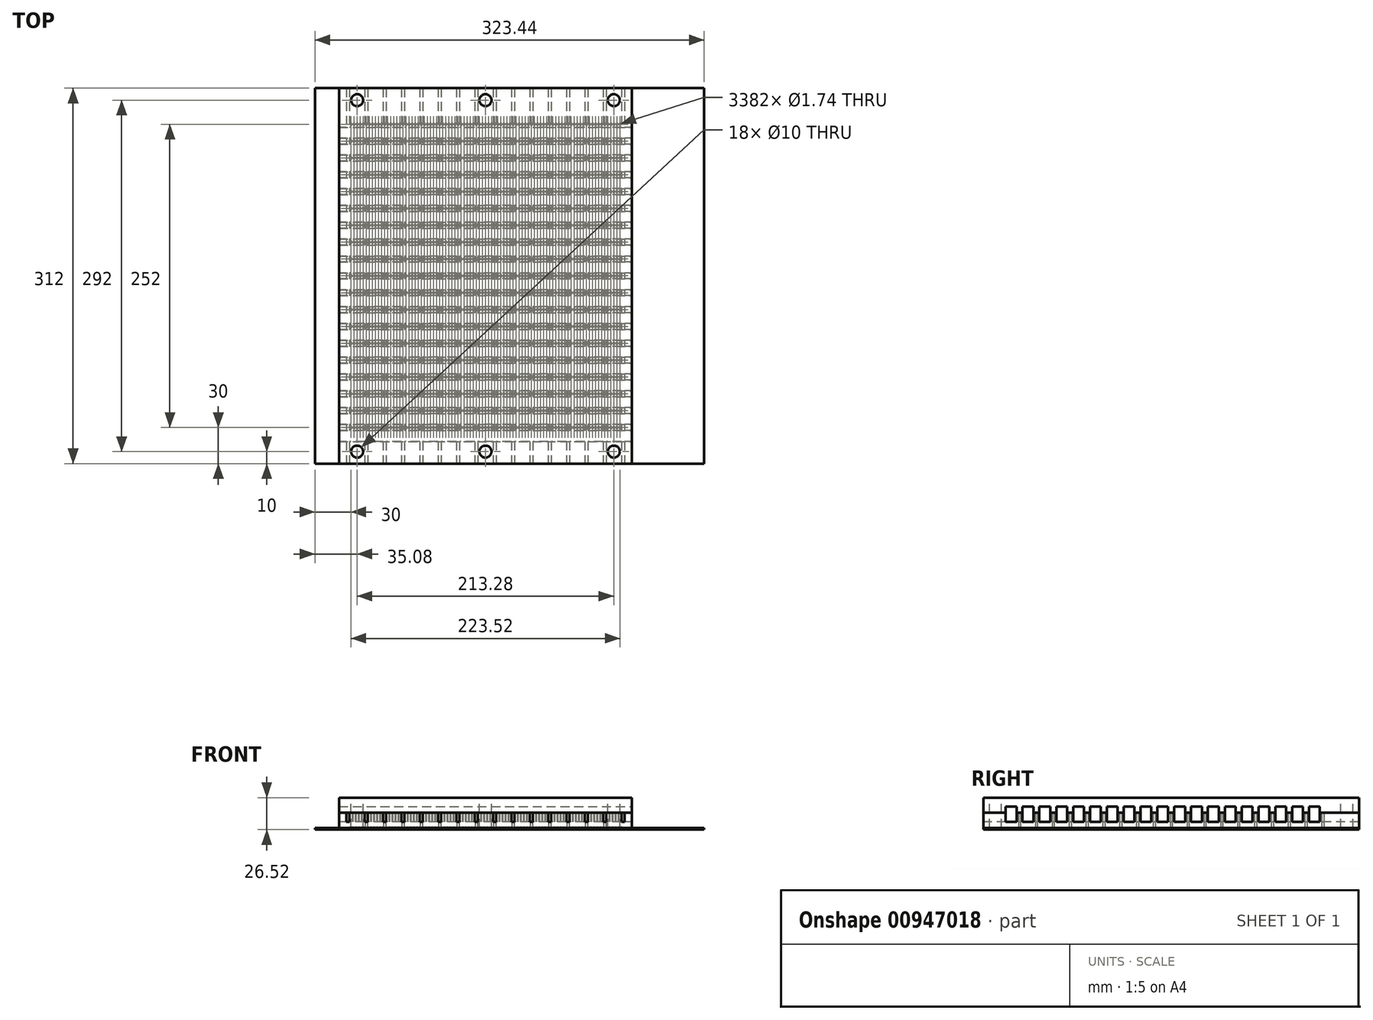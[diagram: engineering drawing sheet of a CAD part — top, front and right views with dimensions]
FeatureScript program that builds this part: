
annotation { "Feature Type Name" : "Feature", "Feature Type Description" : "" }
export const myFeature = defineFeature(function(context is Context, id is Id, definition is map)
    precondition{}
    {
        {
            var Q0;
            Q0=qCreatedBy(makeId("Top.planeOp"),FACE);
            var sketch = newSketch(context, id + "F0", { "sketchPlane" : qUnion([Q0])});
            skCircle(sketch, "E0", {"center": v(0, 0) * mm, "radius": 0.87 * mm});
            skCircle(sketch, "E1.0.1.0", {"center": v(0, -14) * mm, "radius": 0.87 * mm});
            skCircle(sketch, "E1.0.2.0", {"center": v(0, -28) * mm, "radius": 0.87 * mm});
            skCircle(sketch, "E1.0.3.0", {"center": v(0, -42) * mm, "radius": 0.87 * mm});
            skCircle(sketch, "E1.0.4.0", {"center": v(0, -56) * mm, "radius": 0.87 * mm});
            skCircle(sketch, "E1.0.5.0", {"center": v(0, -70) * mm, "radius": 0.87 * mm});
            skCircle(sketch, "E1.0.6.0", {"center": v(0, -84) * mm, "radius": 0.87 * mm});
            skCircle(sketch, "E1.0.7.0", {"center": v(0, -98) * mm, "radius": 0.87 * mm});
            skCircle(sketch, "E1.0.8.0", {"center": v(0, -112) * mm, "radius": 0.87 * mm});
            skCircle(sketch, "E1.0.9.0", {"center": v(0, -126) * mm, "radius": 0.87 * mm});
            skCircle(sketch, "E1.0.10.0", {"center": v(0, -140) * mm, "radius": 0.87 * mm});
            skCircle(sketch, "E1.0.11.0", {"center": v(0, -154) * mm, "radius": 0.87 * mm});
            skCircle(sketch, "E1.0.12.0", {"center": v(0, -168) * mm, "radius": 0.87 * mm});
            skCircle(sketch, "E1.0.13.0", {"center": v(0, -182) * mm, "radius": 0.87 * mm});
            skCircle(sketch, "E1.0.14.0", {"center": v(0, -196) * mm, "radius": 0.87 * mm});
            skCircle(sketch, "E1.0.15.0", {"center": v(0, -210) * mm, "radius": 0.87 * mm});
            skCircle(sketch, "E1.0.16.0", {"center": v(0, -224) * mm, "radius": 0.87 * mm});
            skCircle(sketch, "E1.0.17.0", {"center": v(0, -238) * mm, "radius": 0.87 * mm});
            skCircle(sketch, "E1.0.18.0", {"center": v(0, -252) * mm, "radius": 0.87 * mm});
            skCircle(sketch, "E1.1.0.0", {"center": v(2.54, 0) * mm, "radius": 0.87 * mm});
            skCircle(sketch, "E1.1.1.0", {"center": v(2.54, -14) * mm, "radius": 0.87 * mm});
            skCircle(sketch, "E1.1.2.0", {"center": v(2.54, -28) * mm, "radius": 0.87 * mm});
            skCircle(sketch, "E1.1.3.0", {"center": v(2.54, -42) * mm, "radius": 0.87 * mm});
            skCircle(sketch, "E1.1.4.0", {"center": v(2.54, -56) * mm, "radius": 0.87 * mm});
            skCircle(sketch, "E1.1.5.0", {"center": v(2.54, -70) * mm, "radius": 0.87 * mm});
            skCircle(sketch, "E1.1.6.0", {"center": v(2.54, -84) * mm, "radius": 0.87 * mm});
            skCircle(sketch, "E1.1.7.0", {"center": v(2.54, -98) * mm, "radius": 0.87 * mm});
            skCircle(sketch, "E1.1.8.0", {"center": v(2.54, -112) * mm, "radius": 0.87 * mm});
            skCircle(sketch, "E1.1.9.0", {"center": v(2.54, -126) * mm, "radius": 0.87 * mm});
            skCircle(sketch, "E1.1.10.0", {"center": v(2.54, -140) * mm, "radius": 0.87 * mm});
            skCircle(sketch, "E1.1.11.0", {"center": v(2.54, -154) * mm, "radius": 0.87 * mm});
            skCircle(sketch, "E1.1.12.0", {"center": v(2.54, -168) * mm, "radius": 0.87 * mm});
            skCircle(sketch, "E1.1.13.0", {"center": v(2.54, -182) * mm, "radius": 0.87 * mm});
            skCircle(sketch, "E1.1.14.0", {"center": v(2.54, -196) * mm, "radius": 0.87 * mm});
            skCircle(sketch, "E1.1.15.0", {"center": v(2.54, -210) * mm, "radius": 0.87 * mm});
            skCircle(sketch, "E1.1.16.0", {"center": v(2.54, -224) * mm, "radius": 0.87 * mm});
            skCircle(sketch, "E1.1.17.0", {"center": v(2.54, -238) * mm, "radius": 0.87 * mm});
            skCircle(sketch, "E1.1.18.0", {"center": v(2.54, -252) * mm, "radius": 0.87 * mm});
            skCircle(sketch, "E1.2.0.0", {"center": v(5.08, 0) * mm, "radius": 0.87 * mm});
            skCircle(sketch, "E1.2.1.0", {"center": v(5.08, -14) * mm, "radius": 0.87 * mm});
            skCircle(sketch, "E1.2.2.0", {"center": v(5.08, -28) * mm, "radius": 0.87 * mm});
            skCircle(sketch, "E1.2.3.0", {"center": v(5.08, -42) * mm, "radius": 0.87 * mm});
            skCircle(sketch, "E1.2.4.0", {"center": v(5.08, -56) * mm, "radius": 0.87 * mm});
            skCircle(sketch, "E1.2.5.0", {"center": v(5.08, -70) * mm, "radius": 0.87 * mm});
            skCircle(sketch, "E1.2.6.0", {"center": v(5.08, -84) * mm, "radius": 0.87 * mm});
            skCircle(sketch, "E1.2.7.0", {"center": v(5.08, -98) * mm, "radius": 0.87 * mm});
            skCircle(sketch, "E1.2.8.0", {"center": v(5.08, -112) * mm, "radius": 0.87 * mm});
            skCircle(sketch, "E1.2.9.0", {"center": v(5.08, -126) * mm, "radius": 0.87 * mm});
            skCircle(sketch, "E1.2.10.0", {"center": v(5.08, -140) * mm, "radius": 0.87 * mm});
            skCircle(sketch, "E1.2.11.0", {"center": v(5.08, -154) * mm, "radius": 0.87 * mm});
            skCircle(sketch, "E1.2.12.0", {"center": v(5.08, -168) * mm, "radius": 0.87 * mm});
            skCircle(sketch, "E1.2.13.0", {"center": v(5.08, -182) * mm, "radius": 0.87 * mm});
            skCircle(sketch, "E1.2.14.0", {"center": v(5.08, -196) * mm, "radius": 0.87 * mm});
            skCircle(sketch, "E1.2.15.0", {"center": v(5.08, -210) * mm, "radius": 0.87 * mm});
            skCircle(sketch, "E1.2.16.0", {"center": v(5.08, -224) * mm, "radius": 0.87 * mm});
            skCircle(sketch, "E1.2.17.0", {"center": v(5.08, -238) * mm, "radius": 0.87 * mm});
            skCircle(sketch, "E1.2.18.0", {"center": v(5.08, -252) * mm, "radius": 0.87 * mm});
            skCircle(sketch, "E1.3.0.0", {"center": v(7.62, 0) * mm, "radius": 0.87 * mm});
            skCircle(sketch, "E1.3.1.0", {"center": v(7.62, -14) * mm, "radius": 0.87 * mm});
            skCircle(sketch, "E1.3.2.0", {"center": v(7.62, -28) * mm, "radius": 0.87 * mm});
            skCircle(sketch, "E1.3.3.0", {"center": v(7.62, -42) * mm, "radius": 0.87 * mm});
            skCircle(sketch, "E1.3.4.0", {"center": v(7.62, -56) * mm, "radius": 0.87 * mm});
            skCircle(sketch, "E1.3.5.0", {"center": v(7.62, -70) * mm, "radius": 0.87 * mm});
            skCircle(sketch, "E1.3.6.0", {"center": v(7.62, -84) * mm, "radius": 0.87 * mm});
            skCircle(sketch, "E1.3.7.0", {"center": v(7.62, -98) * mm, "radius": 0.87 * mm});
            skCircle(sketch, "E1.3.8.0", {"center": v(7.62, -112) * mm, "radius": 0.87 * mm});
            skCircle(sketch, "E1.3.9.0", {"center": v(7.62, -126) * mm, "radius": 0.87 * mm});
            skCircle(sketch, "E1.3.10.0", {"center": v(7.62, -140) * mm, "radius": 0.87 * mm});
            skCircle(sketch, "E1.3.11.0", {"center": v(7.62, -154) * mm, "radius": 0.87 * mm});
            skCircle(sketch, "E1.3.12.0", {"center": v(7.62, -168) * mm, "radius": 0.87 * mm});
            skCircle(sketch, "E1.3.13.0", {"center": v(7.62, -182) * mm, "radius": 0.87 * mm});
            skCircle(sketch, "E1.3.14.0", {"center": v(7.62, -196) * mm, "radius": 0.87 * mm});
            skCircle(sketch, "E1.3.15.0", {"center": v(7.62, -210) * mm, "radius": 0.87 * mm});
            skCircle(sketch, "E1.3.16.0", {"center": v(7.62, -224) * mm, "radius": 0.87 * mm});
            skCircle(sketch, "E1.3.17.0", {"center": v(7.62, -238) * mm, "radius": 0.87 * mm});
            skCircle(sketch, "E1.3.18.0", {"center": v(7.62, -252) * mm, "radius": 0.87 * mm});
            skCircle(sketch, "E1.4.0.0", {"center": v(10.16, 0) * mm, "radius": 0.87 * mm});
            skCircle(sketch, "E1.4.1.0", {"center": v(10.16, -14) * mm, "radius": 0.87 * mm});
            skCircle(sketch, "E1.4.2.0", {"center": v(10.16, -28) * mm, "radius": 0.87 * mm});
            skCircle(sketch, "E1.4.3.0", {"center": v(10.16, -42) * mm, "radius": 0.87 * mm});
            skCircle(sketch, "E1.4.4.0", {"center": v(10.16, -56) * mm, "radius": 0.87 * mm});
            skCircle(sketch, "E1.4.5.0", {"center": v(10.16, -70) * mm, "radius": 0.87 * mm});
            skCircle(sketch, "E1.4.6.0", {"center": v(10.16, -84) * mm, "radius": 0.87 * mm});
            skCircle(sketch, "E1.4.7.0", {"center": v(10.16, -98) * mm, "radius": 0.87 * mm});
            skCircle(sketch, "E1.4.8.0", {"center": v(10.16, -112) * mm, "radius": 0.87 * mm});
            skCircle(sketch, "E1.4.9.0", {"center": v(10.16, -126) * mm, "radius": 0.87 * mm});
            skCircle(sketch, "E1.4.10.0", {"center": v(10.16, -140) * mm, "radius": 0.87 * mm});
            skCircle(sketch, "E1.4.11.0", {"center": v(10.16, -154) * mm, "radius": 0.87 * mm});
            skCircle(sketch, "E1.4.12.0", {"center": v(10.16, -168) * mm, "radius": 0.87 * mm});
            skCircle(sketch, "E1.4.13.0", {"center": v(10.16, -182) * mm, "radius": 0.87 * mm});
            skCircle(sketch, "E1.4.14.0", {"center": v(10.16, -196) * mm, "radius": 0.87 * mm});
            skCircle(sketch, "E1.4.15.0", {"center": v(10.16, -210) * mm, "radius": 0.87 * mm});
            skCircle(sketch, "E1.4.16.0", {"center": v(10.16, -224) * mm, "radius": 0.87 * mm});
            skCircle(sketch, "E1.4.17.0", {"center": v(10.16, -238) * mm, "radius": 0.87 * mm});
            skCircle(sketch, "E1.4.18.0", {"center": v(10.16, -252) * mm, "radius": 0.87 * mm});
            skCircle(sketch, "E1.5.0.0", {"center": v(12.7, 0) * mm, "radius": 0.87 * mm});
            skCircle(sketch, "E1.5.1.0", {"center": v(12.7, -14) * mm, "radius": 0.87 * mm});
            skCircle(sketch, "E1.5.2.0", {"center": v(12.7, -28) * mm, "radius": 0.87 * mm});
            skCircle(sketch, "E1.5.3.0", {"center": v(12.7, -42) * mm, "radius": 0.87 * mm});
            skCircle(sketch, "E1.5.4.0", {"center": v(12.7, -56) * mm, "radius": 0.87 * mm});
            skCircle(sketch, "E1.5.5.0", {"center": v(12.7, -70) * mm, "radius": 0.87 * mm});
            skCircle(sketch, "E1.5.6.0", {"center": v(12.7, -84) * mm, "radius": 0.87 * mm});
            skCircle(sketch, "E1.5.7.0", {"center": v(12.7, -98) * mm, "radius": 0.87 * mm});
            skCircle(sketch, "E1.5.8.0", {"center": v(12.7, -112) * mm, "radius": 0.87 * mm});
            skCircle(sketch, "E1.5.9.0", {"center": v(12.7, -126) * mm, "radius": 0.87 * mm});
            skCircle(sketch, "E1.5.10.0", {"center": v(12.7, -140) * mm, "radius": 0.87 * mm});
            skCircle(sketch, "E1.5.11.0", {"center": v(12.7, -154) * mm, "radius": 0.87 * mm});
            skCircle(sketch, "E1.5.12.0", {"center": v(12.7, -168) * mm, "radius": 0.87 * mm});
            skCircle(sketch, "E1.5.13.0", {"center": v(12.7, -182) * mm, "radius": 0.87 * mm});
            skCircle(sketch, "E1.5.14.0", {"center": v(12.7, -196) * mm, "radius": 0.87 * mm});
            skCircle(sketch, "E1.5.15.0", {"center": v(12.7, -210) * mm, "radius": 0.87 * mm});
            skCircle(sketch, "E1.5.16.0", {"center": v(12.7, -224) * mm, "radius": 0.87 * mm});
            skCircle(sketch, "E1.5.17.0", {"center": v(12.7, -238) * mm, "radius": 0.87 * mm});
            skCircle(sketch, "E1.5.18.0", {"center": v(12.7, -252) * mm, "radius": 0.87 * mm});
            skCircle(sketch, "E1.6.0.0", {"center": v(15.24, 0) * mm, "radius": 0.87 * mm});
            skCircle(sketch, "E1.6.1.0", {"center": v(15.24, -14) * mm, "radius": 0.87 * mm});
            skCircle(sketch, "E1.6.2.0", {"center": v(15.24, -28) * mm, "radius": 0.87 * mm});
            skCircle(sketch, "E1.6.3.0", {"center": v(15.24, -42) * mm, "radius": 0.87 * mm});
            skCircle(sketch, "E1.6.4.0", {"center": v(15.24, -56) * mm, "radius": 0.87 * mm});
            skCircle(sketch, "E1.6.5.0", {"center": v(15.24, -70) * mm, "radius": 0.87 * mm});
            skCircle(sketch, "E1.6.6.0", {"center": v(15.24, -84) * mm, "radius": 0.87 * mm});
            skCircle(sketch, "E1.6.7.0", {"center": v(15.24, -98) * mm, "radius": 0.87 * mm});
            skCircle(sketch, "E1.6.8.0", {"center": v(15.24, -112) * mm, "radius": 0.87 * mm});
            skCircle(sketch, "E1.6.9.0", {"center": v(15.24, -126) * mm, "radius": 0.87 * mm});
            skCircle(sketch, "E1.6.10.0", {"center": v(15.24, -140) * mm, "radius": 0.87 * mm});
            skCircle(sketch, "E1.6.11.0", {"center": v(15.24, -154) * mm, "radius": 0.87 * mm});
            skCircle(sketch, "E1.6.12.0", {"center": v(15.24, -168) * mm, "radius": 0.87 * mm});
            skCircle(sketch, "E1.6.13.0", {"center": v(15.24, -182) * mm, "radius": 0.87 * mm});
            skCircle(sketch, "E1.6.14.0", {"center": v(15.24, -196) * mm, "radius": 0.87 * mm});
            skCircle(sketch, "E1.6.15.0", {"center": v(15.24, -210) * mm, "radius": 0.87 * mm});
            skCircle(sketch, "E1.6.16.0", {"center": v(15.24, -224) * mm, "radius": 0.87 * mm});
            skCircle(sketch, "E1.6.17.0", {"center": v(15.24, -238) * mm, "radius": 0.87 * mm});
            skCircle(sketch, "E1.6.18.0", {"center": v(15.24, -252) * mm, "radius": 0.87 * mm});
            skCircle(sketch, "E1.7.0.0", {"center": v(17.78, 0) * mm, "radius": 0.87 * mm});
            skCircle(sketch, "E1.7.1.0", {"center": v(17.78, -14) * mm, "radius": 0.87 * mm});
            skCircle(sketch, "E1.7.2.0", {"center": v(17.78, -28) * mm, "radius": 0.87 * mm});
            skCircle(sketch, "E1.7.3.0", {"center": v(17.78, -42) * mm, "radius": 0.87 * mm});
            skCircle(sketch, "E1.7.4.0", {"center": v(17.78, -56) * mm, "radius": 0.87 * mm});
            skCircle(sketch, "E1.7.5.0", {"center": v(17.78, -70) * mm, "radius": 0.87 * mm});
            skCircle(sketch, "E1.7.6.0", {"center": v(17.78, -84) * mm, "radius": 0.87 * mm});
            skCircle(sketch, "E1.7.7.0", {"center": v(17.78, -98) * mm, "radius": 0.87 * mm});
            skCircle(sketch, "E1.7.8.0", {"center": v(17.78, -112) * mm, "radius": 0.87 * mm});
            skCircle(sketch, "E1.7.9.0", {"center": v(17.78, -126) * mm, "radius": 0.87 * mm});
            skCircle(sketch, "E1.7.10.0", {"center": v(17.78, -140) * mm, "radius": 0.87 * mm});
            skCircle(sketch, "E1.7.11.0", {"center": v(17.78, -154) * mm, "radius": 0.87 * mm});
            skCircle(sketch, "E1.7.12.0", {"center": v(17.78, -168) * mm, "radius": 0.87 * mm});
            skCircle(sketch, "E1.7.13.0", {"center": v(17.78, -182) * mm, "radius": 0.87 * mm});
            skCircle(sketch, "E1.7.14.0", {"center": v(17.78, -196) * mm, "radius": 0.87 * mm});
            skCircle(sketch, "E1.7.15.0", {"center": v(17.78, -210) * mm, "radius": 0.87 * mm});
            skCircle(sketch, "E1.7.16.0", {"center": v(17.78, -224) * mm, "radius": 0.87 * mm});
            skCircle(sketch, "E1.7.17.0", {"center": v(17.78, -238) * mm, "radius": 0.87 * mm});
            skCircle(sketch, "E1.7.18.0", {"center": v(17.78, -252) * mm, "radius": 0.87 * mm});
            skCircle(sketch, "E1.8.0.0", {"center": v(20.32, 0) * mm, "radius": 0.87 * mm});
            skCircle(sketch, "E1.8.1.0", {"center": v(20.32, -14) * mm, "radius": 0.87 * mm});
            skCircle(sketch, "E1.8.2.0", {"center": v(20.32, -28) * mm, "radius": 0.87 * mm});
            skCircle(sketch, "E1.8.3.0", {"center": v(20.32, -42) * mm, "radius": 0.87 * mm});
            skCircle(sketch, "E1.8.4.0", {"center": v(20.32, -56) * mm, "radius": 0.87 * mm});
            skCircle(sketch, "E1.8.5.0", {"center": v(20.32, -70) * mm, "radius": 0.87 * mm});
            skCircle(sketch, "E1.8.6.0", {"center": v(20.32, -84) * mm, "radius": 0.87 * mm});
            skCircle(sketch, "E1.8.7.0", {"center": v(20.32, -98) * mm, "radius": 0.87 * mm});
            skCircle(sketch, "E1.8.8.0", {"center": v(20.32, -112) * mm, "radius": 0.87 * mm});
            skCircle(sketch, "E1.8.9.0", {"center": v(20.32, -126) * mm, "radius": 0.87 * mm});
            skCircle(sketch, "E1.8.10.0", {"center": v(20.32, -140) * mm, "radius": 0.87 * mm});
            skCircle(sketch, "E1.8.11.0", {"center": v(20.32, -154) * mm, "radius": 0.87 * mm});
            skCircle(sketch, "E1.8.12.0", {"center": v(20.32, -168) * mm, "radius": 0.87 * mm});
            skCircle(sketch, "E1.8.13.0", {"center": v(20.32, -182) * mm, "radius": 0.87 * mm});
            skCircle(sketch, "E1.8.14.0", {"center": v(20.32, -196) * mm, "radius": 0.87 * mm});
            skCircle(sketch, "E1.8.15.0", {"center": v(20.32, -210) * mm, "radius": 0.87 * mm});
            skCircle(sketch, "E1.8.16.0", {"center": v(20.32, -224) * mm, "radius": 0.87 * mm});
            skCircle(sketch, "E1.8.17.0", {"center": v(20.32, -238) * mm, "radius": 0.87 * mm});
            skCircle(sketch, "E1.8.18.0", {"center": v(20.32, -252) * mm, "radius": 0.87 * mm});
            skCircle(sketch, "E1.9.0.0", {"center": v(22.86, 0) * mm, "radius": 0.87 * mm});
            skCircle(sketch, "E1.9.1.0", {"center": v(22.86, -14) * mm, "radius": 0.87 * mm});
            skCircle(sketch, "E1.9.2.0", {"center": v(22.86, -28) * mm, "radius": 0.87 * mm});
            skCircle(sketch, "E1.9.3.0", {"center": v(22.86, -42) * mm, "radius": 0.87 * mm});
            skCircle(sketch, "E1.9.4.0", {"center": v(22.86, -56) * mm, "radius": 0.87 * mm});
            skCircle(sketch, "E1.9.5.0", {"center": v(22.86, -70) * mm, "radius": 0.87 * mm});
            skCircle(sketch, "E1.9.6.0", {"center": v(22.86, -84) * mm, "radius": 0.87 * mm});
            skCircle(sketch, "E1.9.7.0", {"center": v(22.86, -98) * mm, "radius": 0.87 * mm});
            skCircle(sketch, "E1.9.8.0", {"center": v(22.86, -112) * mm, "radius": 0.87 * mm});
            skCircle(sketch, "E1.9.9.0", {"center": v(22.86, -126) * mm, "radius": 0.87 * mm});
            skCircle(sketch, "E1.9.10.0", {"center": v(22.86, -140) * mm, "radius": 0.87 * mm});
            skCircle(sketch, "E1.9.11.0", {"center": v(22.86, -154) * mm, "radius": 0.87 * mm});
            skCircle(sketch, "E1.9.12.0", {"center": v(22.86, -168) * mm, "radius": 0.87 * mm});
            skCircle(sketch, "E1.9.13.0", {"center": v(22.86, -182) * mm, "radius": 0.87 * mm});
            skCircle(sketch, "E1.9.14.0", {"center": v(22.86, -196) * mm, "radius": 0.87 * mm});
            skCircle(sketch, "E1.9.15.0", {"center": v(22.86, -210) * mm, "radius": 0.87 * mm});
            skCircle(sketch, "E1.9.16.0", {"center": v(22.86, -224) * mm, "radius": 0.87 * mm});
            skCircle(sketch, "E1.9.17.0", {"center": v(22.86, -238) * mm, "radius": 0.87 * mm});
            skCircle(sketch, "E1.9.18.0", {"center": v(22.86, -252) * mm, "radius": 0.87 * mm});
            skCircle(sketch, "E1.10.0.0", {"center": v(25.4, 0) * mm, "radius": 0.87 * mm});
            skCircle(sketch, "E1.10.1.0", {"center": v(25.4, -14) * mm, "radius": 0.87 * mm});
            skCircle(sketch, "E1.10.2.0", {"center": v(25.4, -28) * mm, "radius": 0.87 * mm});
            skCircle(sketch, "E1.10.3.0", {"center": v(25.4, -42) * mm, "radius": 0.87 * mm});
            skCircle(sketch, "E1.10.4.0", {"center": v(25.4, -56) * mm, "radius": 0.87 * mm});
            skCircle(sketch, "E1.10.5.0", {"center": v(25.4, -70) * mm, "radius": 0.87 * mm});
            skCircle(sketch, "E1.10.6.0", {"center": v(25.4, -84) * mm, "radius": 0.87 * mm});
            skCircle(sketch, "E1.10.7.0", {"center": v(25.4, -98) * mm, "radius": 0.87 * mm});
            skCircle(sketch, "E1.10.8.0", {"center": v(25.4, -112) * mm, "radius": 0.87 * mm});
            skCircle(sketch, "E1.10.9.0", {"center": v(25.4, -126) * mm, "radius": 0.87 * mm});
            skCircle(sketch, "E1.10.10.0", {"center": v(25.4, -140) * mm, "radius": 0.87 * mm});
            skCircle(sketch, "E1.10.11.0", {"center": v(25.4, -154) * mm, "radius": 0.87 * mm});
            skCircle(sketch, "E1.10.12.0", {"center": v(25.4, -168) * mm, "radius": 0.87 * mm});
            skCircle(sketch, "E1.10.13.0", {"center": v(25.4, -182) * mm, "radius": 0.87 * mm});
            skCircle(sketch, "E1.10.14.0", {"center": v(25.4, -196) * mm, "radius": 0.87 * mm});
            skCircle(sketch, "E1.10.15.0", {"center": v(25.4, -210) * mm, "radius": 0.87 * mm});
            skCircle(sketch, "E1.10.16.0", {"center": v(25.4, -224) * mm, "radius": 0.87 * mm});
            skCircle(sketch, "E1.10.17.0", {"center": v(25.4, -238) * mm, "radius": 0.87 * mm});
            skCircle(sketch, "E1.10.18.0", {"center": v(25.4, -252) * mm, "radius": 0.87 * mm});
            skCircle(sketch, "E1.11.0.0", {"center": v(27.94, 0) * mm, "radius": 0.87 * mm});
            skCircle(sketch, "E1.11.1.0", {"center": v(27.94, -14) * mm, "radius": 0.87 * mm});
            skCircle(sketch, "E1.11.2.0", {"center": v(27.94, -28) * mm, "radius": 0.87 * mm});
            skCircle(sketch, "E1.11.3.0", {"center": v(27.94, -42) * mm, "radius": 0.87 * mm});
            skCircle(sketch, "E1.11.4.0", {"center": v(27.94, -56) * mm, "radius": 0.87 * mm});
            skCircle(sketch, "E1.11.5.0", {"center": v(27.94, -70) * mm, "radius": 0.87 * mm});
            skCircle(sketch, "E1.11.6.0", {"center": v(27.94, -84) * mm, "radius": 0.87 * mm});
            skCircle(sketch, "E1.11.7.0", {"center": v(27.94, -98) * mm, "radius": 0.87 * mm});
            skCircle(sketch, "E1.11.8.0", {"center": v(27.94, -112) * mm, "radius": 0.87 * mm});
            skCircle(sketch, "E1.11.9.0", {"center": v(27.94, -126) * mm, "radius": 0.87 * mm});
            skCircle(sketch, "E1.11.10.0", {"center": v(27.94, -140) * mm, "radius": 0.87 * mm});
            skCircle(sketch, "E1.11.11.0", {"center": v(27.94, -154) * mm, "radius": 0.87 * mm});
            skCircle(sketch, "E1.11.12.0", {"center": v(27.94, -168) * mm, "radius": 0.87 * mm});
            skCircle(sketch, "E1.11.13.0", {"center": v(27.94, -182) * mm, "radius": 0.87 * mm});
            skCircle(sketch, "E1.11.14.0", {"center": v(27.94, -196) * mm, "radius": 0.87 * mm});
            skCircle(sketch, "E1.11.15.0", {"center": v(27.94, -210) * mm, "radius": 0.87 * mm});
            skCircle(sketch, "E1.11.16.0", {"center": v(27.94, -224) * mm, "radius": 0.87 * mm});
            skCircle(sketch, "E1.11.17.0", {"center": v(27.94, -238) * mm, "radius": 0.87 * mm});
            skCircle(sketch, "E1.11.18.0", {"center": v(27.94, -252) * mm, "radius": 0.87 * mm});
            skCircle(sketch, "E1.12.0.0", {"center": v(30.48, 0) * mm, "radius": 0.87 * mm});
            skCircle(sketch, "E1.12.1.0", {"center": v(30.48, -14) * mm, "radius": 0.87 * mm});
            skCircle(sketch, "E1.12.2.0", {"center": v(30.48, -28) * mm, "radius": 0.87 * mm});
            skCircle(sketch, "E1.12.3.0", {"center": v(30.48, -42) * mm, "radius": 0.87 * mm});
            skCircle(sketch, "E1.12.4.0", {"center": v(30.48, -56) * mm, "radius": 0.87 * mm});
            skCircle(sketch, "E1.12.5.0", {"center": v(30.48, -70) * mm, "radius": 0.87 * mm});
            skCircle(sketch, "E1.12.6.0", {"center": v(30.48, -84) * mm, "radius": 0.87 * mm});
            skCircle(sketch, "E1.12.7.0", {"center": v(30.48, -98) * mm, "radius": 0.87 * mm});
            skCircle(sketch, "E1.12.8.0", {"center": v(30.48, -112) * mm, "radius": 0.87 * mm});
            skCircle(sketch, "E1.12.9.0", {"center": v(30.48, -126) * mm, "radius": 0.87 * mm});
            skCircle(sketch, "E1.12.10.0", {"center": v(30.48, -140) * mm, "radius": 0.87 * mm});
            skCircle(sketch, "E1.12.11.0", {"center": v(30.48, -154) * mm, "radius": 0.87 * mm});
            skCircle(sketch, "E1.12.12.0", {"center": v(30.48, -168) * mm, "radius": 0.87 * mm});
            skCircle(sketch, "E1.12.13.0", {"center": v(30.48, -182) * mm, "radius": 0.87 * mm});
            skCircle(sketch, "E1.12.14.0", {"center": v(30.48, -196) * mm, "radius": 0.87 * mm});
            skCircle(sketch, "E1.12.15.0", {"center": v(30.48, -210) * mm, "radius": 0.87 * mm});
            skCircle(sketch, "E1.12.16.0", {"center": v(30.48, -224) * mm, "radius": 0.87 * mm});
            skCircle(sketch, "E1.12.17.0", {"center": v(30.48, -238) * mm, "radius": 0.87 * mm});
            skCircle(sketch, "E1.12.18.0", {"center": v(30.48, -252) * mm, "radius": 0.87 * mm});
            skCircle(sketch, "E1.13.0.0", {"center": v(33.02, 0) * mm, "radius": 0.87 * mm});
            skCircle(sketch, "E1.13.1.0", {"center": v(33.02, -14) * mm, "radius": 0.87 * mm});
            skCircle(sketch, "E1.13.2.0", {"center": v(33.02, -28) * mm, "radius": 0.87 * mm});
            skCircle(sketch, "E1.13.3.0", {"center": v(33.02, -42) * mm, "radius": 0.87 * mm});
            skCircle(sketch, "E1.13.4.0", {"center": v(33.02, -56) * mm, "radius": 0.87 * mm});
            skCircle(sketch, "E1.13.5.0", {"center": v(33.02, -70) * mm, "radius": 0.87 * mm});
            skCircle(sketch, "E1.13.6.0", {"center": v(33.02, -84) * mm, "radius": 0.87 * mm});
            skCircle(sketch, "E1.13.7.0", {"center": v(33.02, -98) * mm, "radius": 0.87 * mm});
            skCircle(sketch, "E1.13.8.0", {"center": v(33.02, -112) * mm, "radius": 0.87 * mm});
            skCircle(sketch, "E1.13.9.0", {"center": v(33.02, -126) * mm, "radius": 0.87 * mm});
            skCircle(sketch, "E1.13.10.0", {"center": v(33.02, -140) * mm, "radius": 0.87 * mm});
            skCircle(sketch, "E1.13.11.0", {"center": v(33.02, -154) * mm, "radius": 0.87 * mm});
            skCircle(sketch, "E1.13.12.0", {"center": v(33.02, -168) * mm, "radius": 0.87 * mm});
            skCircle(sketch, "E1.13.13.0", {"center": v(33.02, -182) * mm, "radius": 0.87 * mm});
            skCircle(sketch, "E1.13.14.0", {"center": v(33.02, -196) * mm, "radius": 0.87 * mm});
            skCircle(sketch, "E1.13.15.0", {"center": v(33.02, -210) * mm, "radius": 0.87 * mm});
            skCircle(sketch, "E1.13.16.0", {"center": v(33.02, -224) * mm, "radius": 0.87 * mm});
            skCircle(sketch, "E1.13.17.0", {"center": v(33.02, -238) * mm, "radius": 0.87 * mm});
            skCircle(sketch, "E1.13.18.0", {"center": v(33.02, -252) * mm, "radius": 0.87 * mm});
            skCircle(sketch, "E1.14.0.0", {"center": v(35.56, 0) * mm, "radius": 0.87 * mm});
            skCircle(sketch, "E1.14.1.0", {"center": v(35.56, -14) * mm, "radius": 0.87 * mm});
            skCircle(sketch, "E1.14.2.0", {"center": v(35.56, -28) * mm, "radius": 0.87 * mm});
            skCircle(sketch, "E1.14.3.0", {"center": v(35.56, -42) * mm, "radius": 0.87 * mm});
            skCircle(sketch, "E1.14.4.0", {"center": v(35.56, -56) * mm, "radius": 0.87 * mm});
            skCircle(sketch, "E1.14.5.0", {"center": v(35.56, -70) * mm, "radius": 0.87 * mm});
            skCircle(sketch, "E1.14.6.0", {"center": v(35.56, -84) * mm, "radius": 0.87 * mm});
            skCircle(sketch, "E1.14.7.0", {"center": v(35.56, -98) * mm, "radius": 0.87 * mm});
            skCircle(sketch, "E1.14.8.0", {"center": v(35.56, -112) * mm, "radius": 0.87 * mm});
            skCircle(sketch, "E1.14.9.0", {"center": v(35.56, -126) * mm, "radius": 0.87 * mm});
            skCircle(sketch, "E1.14.10.0", {"center": v(35.56, -140) * mm, "radius": 0.87 * mm});
            skCircle(sketch, "E1.14.11.0", {"center": v(35.56, -154) * mm, "radius": 0.87 * mm});
            skCircle(sketch, "E1.14.12.0", {"center": v(35.56, -168) * mm, "radius": 0.87 * mm});
            skCircle(sketch, "E1.14.13.0", {"center": v(35.56, -182) * mm, "radius": 0.87 * mm});
            skCircle(sketch, "E1.14.14.0", {"center": v(35.56, -196) * mm, "radius": 0.87 * mm});
            skCircle(sketch, "E1.14.15.0", {"center": v(35.56, -210) * mm, "radius": 0.87 * mm});
            skCircle(sketch, "E1.14.16.0", {"center": v(35.56, -224) * mm, "radius": 0.87 * mm});
            skCircle(sketch, "E1.14.17.0", {"center": v(35.56, -238) * mm, "radius": 0.87 * mm});
            skCircle(sketch, "E1.14.18.0", {"center": v(35.56, -252) * mm, "radius": 0.87 * mm});
            skCircle(sketch, "E1.15.0.0", {"center": v(38.1, 0) * mm, "radius": 0.87 * mm});
            skCircle(sketch, "E1.15.1.0", {"center": v(38.1, -14) * mm, "radius": 0.87 * mm});
            skCircle(sketch, "E1.15.2.0", {"center": v(38.1, -28) * mm, "radius": 0.87 * mm});
            skCircle(sketch, "E1.15.3.0", {"center": v(38.1, -42) * mm, "radius": 0.87 * mm});
            skCircle(sketch, "E1.15.4.0", {"center": v(38.1, -56) * mm, "radius": 0.87 * mm});
            skCircle(sketch, "E1.15.5.0", {"center": v(38.1, -70) * mm, "radius": 0.87 * mm});
            skCircle(sketch, "E1.15.6.0", {"center": v(38.1, -84) * mm, "radius": 0.87 * mm});
            skCircle(sketch, "E1.15.7.0", {"center": v(38.1, -98) * mm, "radius": 0.87 * mm});
            skCircle(sketch, "E1.15.8.0", {"center": v(38.1, -112) * mm, "radius": 0.87 * mm});
            skCircle(sketch, "E1.15.9.0", {"center": v(38.1, -126) * mm, "radius": 0.87 * mm});
            skCircle(sketch, "E1.15.10.0", {"center": v(38.1, -140) * mm, "radius": 0.87 * mm});
            skCircle(sketch, "E1.15.11.0", {"center": v(38.1, -154) * mm, "radius": 0.87 * mm});
            skCircle(sketch, "E1.15.12.0", {"center": v(38.1, -168) * mm, "radius": 0.87 * mm});
            skCircle(sketch, "E1.15.13.0", {"center": v(38.1, -182) * mm, "radius": 0.87 * mm});
            skCircle(sketch, "E1.15.14.0", {"center": v(38.1, -196) * mm, "radius": 0.87 * mm});
            skCircle(sketch, "E1.15.15.0", {"center": v(38.1, -210) * mm, "radius": 0.87 * mm});
            skCircle(sketch, "E1.15.16.0", {"center": v(38.1, -224) * mm, "radius": 0.87 * mm});
            skCircle(sketch, "E1.15.17.0", {"center": v(38.1, -238) * mm, "radius": 0.87 * mm});
            skCircle(sketch, "E1.15.18.0", {"center": v(38.1, -252) * mm, "radius": 0.87 * mm});
            skCircle(sketch, "E1.16.0.0", {"center": v(40.64, 0) * mm, "radius": 0.87 * mm});
            skCircle(sketch, "E1.16.1.0", {"center": v(40.64, -14) * mm, "radius": 0.87 * mm});
            skCircle(sketch, "E1.16.2.0", {"center": v(40.64, -28) * mm, "radius": 0.87 * mm});
            skCircle(sketch, "E1.16.3.0", {"center": v(40.64, -42) * mm, "radius": 0.87 * mm});
            skCircle(sketch, "E1.16.4.0", {"center": v(40.64, -56) * mm, "radius": 0.87 * mm});
            skCircle(sketch, "E1.16.5.0", {"center": v(40.64, -70) * mm, "radius": 0.87 * mm});
            skCircle(sketch, "E1.16.6.0", {"center": v(40.64, -84) * mm, "radius": 0.87 * mm});
            skCircle(sketch, "E1.16.7.0", {"center": v(40.64, -98) * mm, "radius": 0.87 * mm});
            skCircle(sketch, "E1.16.8.0", {"center": v(40.64, -112) * mm, "radius": 0.87 * mm});
            skCircle(sketch, "E1.16.9.0", {"center": v(40.64, -126) * mm, "radius": 0.87 * mm});
            skCircle(sketch, "E1.16.10.0", {"center": v(40.64, -140) * mm, "radius": 0.87 * mm});
            skCircle(sketch, "E1.16.11.0", {"center": v(40.64, -154) * mm, "radius": 0.87 * mm});
            skCircle(sketch, "E1.16.12.0", {"center": v(40.64, -168) * mm, "radius": 0.87 * mm});
            skCircle(sketch, "E1.16.13.0", {"center": v(40.64, -182) * mm, "radius": 0.87 * mm});
            skCircle(sketch, "E1.16.14.0", {"center": v(40.64, -196) * mm, "radius": 0.87 * mm});
            skCircle(sketch, "E1.16.15.0", {"center": v(40.64, -210) * mm, "radius": 0.87 * mm});
            skCircle(sketch, "E1.16.16.0", {"center": v(40.64, -224) * mm, "radius": 0.87 * mm});
            skCircle(sketch, "E1.16.17.0", {"center": v(40.64, -238) * mm, "radius": 0.87 * mm});
            skCircle(sketch, "E1.16.18.0", {"center": v(40.64, -252) * mm, "radius": 0.87 * mm});
            skCircle(sketch, "E1.17.0.0", {"center": v(43.18, 0) * mm, "radius": 0.87 * mm});
            skCircle(sketch, "E1.17.1.0", {"center": v(43.18, -14) * mm, "radius": 0.87 * mm});
            skCircle(sketch, "E1.17.2.0", {"center": v(43.18, -28) * mm, "radius": 0.87 * mm});
            skCircle(sketch, "E1.17.3.0", {"center": v(43.18, -42) * mm, "radius": 0.87 * mm});
            skCircle(sketch, "E1.17.4.0", {"center": v(43.18, -56) * mm, "radius": 0.87 * mm});
            skCircle(sketch, "E1.17.5.0", {"center": v(43.18, -70) * mm, "radius": 0.87 * mm});
            skCircle(sketch, "E1.17.6.0", {"center": v(43.18, -84) * mm, "radius": 0.87 * mm});
            skCircle(sketch, "E1.17.7.0", {"center": v(43.18, -98) * mm, "radius": 0.87 * mm});
            skCircle(sketch, "E1.17.8.0", {"center": v(43.18, -112) * mm, "radius": 0.87 * mm});
            skCircle(sketch, "E1.17.9.0", {"center": v(43.18, -126) * mm, "radius": 0.87 * mm});
            skCircle(sketch, "E1.17.10.0", {"center": v(43.18, -140) * mm, "radius": 0.87 * mm});
            skCircle(sketch, "E1.17.11.0", {"center": v(43.18, -154) * mm, "radius": 0.87 * mm});
            skCircle(sketch, "E1.17.12.0", {"center": v(43.18, -168) * mm, "radius": 0.87 * mm});
            skCircle(sketch, "E1.17.13.0", {"center": v(43.18, -182) * mm, "radius": 0.87 * mm});
            skCircle(sketch, "E1.17.14.0", {"center": v(43.18, -196) * mm, "radius": 0.87 * mm});
            skCircle(sketch, "E1.17.15.0", {"center": v(43.18, -210) * mm, "radius": 0.87 * mm});
            skCircle(sketch, "E1.17.16.0", {"center": v(43.18, -224) * mm, "radius": 0.87 * mm});
            skCircle(sketch, "E1.17.17.0", {"center": v(43.18, -238) * mm, "radius": 0.87 * mm});
            skCircle(sketch, "E1.17.18.0", {"center": v(43.18, -252) * mm, "radius": 0.87 * mm});
            skCircle(sketch, "E1.18.0.0", {"center": v(45.72, 0) * mm, "radius": 0.87 * mm});
            skCircle(sketch, "E1.18.1.0", {"center": v(45.72, -14) * mm, "radius": 0.87 * mm});
            skCircle(sketch, "E1.18.2.0", {"center": v(45.72, -28) * mm, "radius": 0.87 * mm});
            skCircle(sketch, "E1.18.3.0", {"center": v(45.72, -42) * mm, "radius": 0.87 * mm});
            skCircle(sketch, "E1.18.4.0", {"center": v(45.72, -56) * mm, "radius": 0.87 * mm});
            skCircle(sketch, "E1.18.5.0", {"center": v(45.72, -70) * mm, "radius": 0.87 * mm});
            skCircle(sketch, "E1.18.6.0", {"center": v(45.72, -84) * mm, "radius": 0.87 * mm});
            skCircle(sketch, "E1.18.7.0", {"center": v(45.72, -98) * mm, "radius": 0.87 * mm});
            skCircle(sketch, "E1.18.8.0", {"center": v(45.72, -112) * mm, "radius": 0.87 * mm});
            skCircle(sketch, "E1.18.9.0", {"center": v(45.72, -126) * mm, "radius": 0.87 * mm});
            skCircle(sketch, "E1.18.10.0", {"center": v(45.72, -140) * mm, "radius": 0.87 * mm});
            skCircle(sketch, "E1.18.11.0", {"center": v(45.72, -154) * mm, "radius": 0.87 * mm});
            skCircle(sketch, "E1.18.12.0", {"center": v(45.72, -168) * mm, "radius": 0.87 * mm});
            skCircle(sketch, "E1.18.13.0", {"center": v(45.72, -182) * mm, "radius": 0.87 * mm});
            skCircle(sketch, "E1.18.14.0", {"center": v(45.72, -196) * mm, "radius": 0.87 * mm});
            skCircle(sketch, "E1.18.15.0", {"center": v(45.72, -210) * mm, "radius": 0.87 * mm});
            skCircle(sketch, "E1.18.16.0", {"center": v(45.72, -224) * mm, "radius": 0.87 * mm});
            skCircle(sketch, "E1.18.17.0", {"center": v(45.72, -238) * mm, "radius": 0.87 * mm});
            skCircle(sketch, "E1.18.18.0", {"center": v(45.72, -252) * mm, "radius": 0.87 * mm});
            skCircle(sketch, "E1.19.0.0", {"center": v(48.26, 0) * mm, "radius": 0.87 * mm});
            skCircle(sketch, "E1.19.1.0", {"center": v(48.26, -14) * mm, "radius": 0.87 * mm});
            skCircle(sketch, "E1.19.2.0", {"center": v(48.26, -28) * mm, "radius": 0.87 * mm});
            skCircle(sketch, "E1.19.3.0", {"center": v(48.26, -42) * mm, "radius": 0.87 * mm});
            skCircle(sketch, "E1.19.4.0", {"center": v(48.26, -56) * mm, "radius": 0.87 * mm});
            skCircle(sketch, "E1.19.5.0", {"center": v(48.26, -70) * mm, "radius": 0.87 * mm});
            skCircle(sketch, "E1.19.6.0", {"center": v(48.26, -84) * mm, "radius": 0.87 * mm});
            skCircle(sketch, "E1.19.7.0", {"center": v(48.26, -98) * mm, "radius": 0.87 * mm});
            skCircle(sketch, "E1.19.8.0", {"center": v(48.26, -112) * mm, "radius": 0.87 * mm});
            skCircle(sketch, "E1.19.9.0", {"center": v(48.26, -126) * mm, "radius": 0.87 * mm});
            skCircle(sketch, "E1.19.10.0", {"center": v(48.26, -140) * mm, "radius": 0.87 * mm});
            skCircle(sketch, "E1.19.11.0", {"center": v(48.26, -154) * mm, "radius": 0.87 * mm});
            skCircle(sketch, "E1.19.12.0", {"center": v(48.26, -168) * mm, "radius": 0.87 * mm});
            skCircle(sketch, "E1.19.13.0", {"center": v(48.26, -182) * mm, "radius": 0.87 * mm});
            skCircle(sketch, "E1.19.14.0", {"center": v(48.26, -196) * mm, "radius": 0.87 * mm});
            skCircle(sketch, "E1.19.15.0", {"center": v(48.26, -210) * mm, "radius": 0.87 * mm});
            skCircle(sketch, "E1.19.16.0", {"center": v(48.26, -224) * mm, "radius": 0.87 * mm});
            skCircle(sketch, "E1.19.17.0", {"center": v(48.26, -238) * mm, "radius": 0.87 * mm});
            skCircle(sketch, "E1.19.18.0", {"center": v(48.26, -252) * mm, "radius": 0.87 * mm});
            skCircle(sketch, "E1.20.0.0", {"center": v(50.8, 0) * mm, "radius": 0.87 * mm});
            skCircle(sketch, "E1.20.1.0", {"center": v(50.8, -14) * mm, "radius": 0.87 * mm});
            skCircle(sketch, "E1.20.2.0", {"center": v(50.8, -28) * mm, "radius": 0.87 * mm});
            skCircle(sketch, "E1.20.3.0", {"center": v(50.8, -42) * mm, "radius": 0.87 * mm});
            skCircle(sketch, "E1.20.4.0", {"center": v(50.8, -56) * mm, "radius": 0.87 * mm});
            skCircle(sketch, "E1.20.5.0", {"center": v(50.8, -70) * mm, "radius": 0.87 * mm});
            skCircle(sketch, "E1.20.6.0", {"center": v(50.8, -84) * mm, "radius": 0.87 * mm});
            skCircle(sketch, "E1.20.7.0", {"center": v(50.8, -98) * mm, "radius": 0.87 * mm});
            skCircle(sketch, "E1.20.8.0", {"center": v(50.8, -112) * mm, "radius": 0.87 * mm});
            skCircle(sketch, "E1.20.9.0", {"center": v(50.8, -126) * mm, "radius": 0.87 * mm});
            skCircle(sketch, "E1.20.10.0", {"center": v(50.8, -140) * mm, "radius": 0.87 * mm});
            skCircle(sketch, "E1.20.11.0", {"center": v(50.8, -154) * mm, "radius": 0.87 * mm});
            skCircle(sketch, "E1.20.12.0", {"center": v(50.8, -168) * mm, "radius": 0.87 * mm});
            skCircle(sketch, "E1.20.13.0", {"center": v(50.8, -182) * mm, "radius": 0.87 * mm});
            skCircle(sketch, "E1.20.14.0", {"center": v(50.8, -196) * mm, "radius": 0.87 * mm});
            skCircle(sketch, "E1.20.15.0", {"center": v(50.8, -210) * mm, "radius": 0.87 * mm});
            skCircle(sketch, "E1.20.16.0", {"center": v(50.8, -224) * mm, "radius": 0.87 * mm});
            skCircle(sketch, "E1.20.17.0", {"center": v(50.8, -238) * mm, "radius": 0.87 * mm});
            skCircle(sketch, "E1.20.18.0", {"center": v(50.8, -252) * mm, "radius": 0.87 * mm});
            skCircle(sketch, "E1.21.0.0", {"center": v(53.34, 0) * mm, "radius": 0.87 * mm});
            skCircle(sketch, "E1.21.1.0", {"center": v(53.34, -14) * mm, "radius": 0.87 * mm});
            skCircle(sketch, "E1.21.2.0", {"center": v(53.34, -28) * mm, "radius": 0.87 * mm});
            skCircle(sketch, "E1.21.3.0", {"center": v(53.34, -42) * mm, "radius": 0.87 * mm});
            skCircle(sketch, "E1.21.4.0", {"center": v(53.34, -56) * mm, "radius": 0.87 * mm});
            skCircle(sketch, "E1.21.5.0", {"center": v(53.34, -70) * mm, "radius": 0.87 * mm});
            skCircle(sketch, "E1.21.6.0", {"center": v(53.34, -84) * mm, "radius": 0.87 * mm});
            skCircle(sketch, "E1.21.7.0", {"center": v(53.34, -98) * mm, "radius": 0.87 * mm});
            skCircle(sketch, "E1.21.8.0", {"center": v(53.34, -112) * mm, "radius": 0.87 * mm});
            skCircle(sketch, "E1.21.9.0", {"center": v(53.34, -126) * mm, "radius": 0.87 * mm});
            skCircle(sketch, "E1.21.10.0", {"center": v(53.34, -140) * mm, "radius": 0.87 * mm});
            skCircle(sketch, "E1.21.11.0", {"center": v(53.34, -154) * mm, "radius": 0.87 * mm});
            skCircle(sketch, "E1.21.12.0", {"center": v(53.34, -168) * mm, "radius": 0.87 * mm});
            skCircle(sketch, "E1.21.13.0", {"center": v(53.34, -182) * mm, "radius": 0.87 * mm});
            skCircle(sketch, "E1.21.14.0", {"center": v(53.34, -196) * mm, "radius": 0.87 * mm});
            skCircle(sketch, "E1.21.15.0", {"center": v(53.34, -210) * mm, "radius": 0.87 * mm});
            skCircle(sketch, "E1.21.16.0", {"center": v(53.34, -224) * mm, "radius": 0.87 * mm});
            skCircle(sketch, "E1.21.17.0", {"center": v(53.34, -238) * mm, "radius": 0.87 * mm});
            skCircle(sketch, "E1.21.18.0", {"center": v(53.34, -252) * mm, "radius": 0.87 * mm});
            skCircle(sketch, "E1.22.0.0", {"center": v(55.88, 0) * mm, "radius": 0.87 * mm});
            skCircle(sketch, "E1.22.1.0", {"center": v(55.88, -14) * mm, "radius": 0.87 * mm});
            skCircle(sketch, "E1.22.2.0", {"center": v(55.88, -28) * mm, "radius": 0.87 * mm});
            skCircle(sketch, "E1.22.3.0", {"center": v(55.88, -42) * mm, "radius": 0.87 * mm});
            skCircle(sketch, "E1.22.4.0", {"center": v(55.88, -56) * mm, "radius": 0.87 * mm});
            skCircle(sketch, "E1.22.5.0", {"center": v(55.88, -70) * mm, "radius": 0.87 * mm});
            skCircle(sketch, "E1.22.6.0", {"center": v(55.88, -84) * mm, "radius": 0.87 * mm});
            skCircle(sketch, "E1.22.7.0", {"center": v(55.88, -98) * mm, "radius": 0.87 * mm});
            skCircle(sketch, "E1.22.8.0", {"center": v(55.88, -112) * mm, "radius": 0.87 * mm});
            skCircle(sketch, "E1.22.9.0", {"center": v(55.88, -126) * mm, "radius": 0.87 * mm});
            skCircle(sketch, "E1.22.10.0", {"center": v(55.88, -140) * mm, "radius": 0.87 * mm});
            skCircle(sketch, "E1.22.11.0", {"center": v(55.88, -154) * mm, "radius": 0.87 * mm});
            skCircle(sketch, "E1.22.12.0", {"center": v(55.88, -168) * mm, "radius": 0.87 * mm});
            skCircle(sketch, "E1.22.13.0", {"center": v(55.88, -182) * mm, "radius": 0.87 * mm});
            skCircle(sketch, "E1.22.14.0", {"center": v(55.88, -196) * mm, "radius": 0.87 * mm});
            skCircle(sketch, "E1.22.15.0", {"center": v(55.88, -210) * mm, "radius": 0.87 * mm});
            skCircle(sketch, "E1.22.16.0", {"center": v(55.88, -224) * mm, "radius": 0.87 * mm});
            skCircle(sketch, "E1.22.17.0", {"center": v(55.88, -238) * mm, "radius": 0.87 * mm});
            skCircle(sketch, "E1.22.18.0", {"center": v(55.88, -252) * mm, "radius": 0.87 * mm});
            skCircle(sketch, "E1.23.0.0", {"center": v(58.42, 0) * mm, "radius": 0.87 * mm});
            skCircle(sketch, "E1.23.1.0", {"center": v(58.42, -14) * mm, "radius": 0.87 * mm});
            skCircle(sketch, "E1.23.2.0", {"center": v(58.42, -28) * mm, "radius": 0.87 * mm});
            skCircle(sketch, "E1.23.3.0", {"center": v(58.42, -42) * mm, "radius": 0.87 * mm});
            skCircle(sketch, "E1.23.4.0", {"center": v(58.42, -56) * mm, "radius": 0.87 * mm});
            skCircle(sketch, "E1.23.5.0", {"center": v(58.42, -70) * mm, "radius": 0.87 * mm});
            skCircle(sketch, "E1.23.6.0", {"center": v(58.42, -84) * mm, "radius": 0.87 * mm});
            skCircle(sketch, "E1.23.7.0", {"center": v(58.42, -98) * mm, "radius": 0.87 * mm});
            skCircle(sketch, "E1.23.8.0", {"center": v(58.42, -112) * mm, "radius": 0.87 * mm});
            skCircle(sketch, "E1.23.9.0", {"center": v(58.42, -126) * mm, "radius": 0.87 * mm});
            skCircle(sketch, "E1.23.10.0", {"center": v(58.42, -140) * mm, "radius": 0.87 * mm});
            skCircle(sketch, "E1.23.11.0", {"center": v(58.42, -154) * mm, "radius": 0.87 * mm});
            skCircle(sketch, "E1.23.12.0", {"center": v(58.42, -168) * mm, "radius": 0.87 * mm});
            skCircle(sketch, "E1.23.13.0", {"center": v(58.42, -182) * mm, "radius": 0.87 * mm});
            skCircle(sketch, "E1.23.14.0", {"center": v(58.42, -196) * mm, "radius": 0.87 * mm});
            skCircle(sketch, "E1.23.15.0", {"center": v(58.42, -210) * mm, "radius": 0.87 * mm});
            skCircle(sketch, "E1.23.16.0", {"center": v(58.42, -224) * mm, "radius": 0.87 * mm});
            skCircle(sketch, "E1.23.17.0", {"center": v(58.42, -238) * mm, "radius": 0.87 * mm});
            skCircle(sketch, "E1.23.18.0", {"center": v(58.42, -252) * mm, "radius": 0.87 * mm});
            skCircle(sketch, "E1.24.0.0", {"center": v(60.96, 0) * mm, "radius": 0.87 * mm});
            skCircle(sketch, "E1.24.1.0", {"center": v(60.96, -14) * mm, "radius": 0.87 * mm});
            skCircle(sketch, "E1.24.2.0", {"center": v(60.96, -28) * mm, "radius": 0.87 * mm});
            skCircle(sketch, "E1.24.3.0", {"center": v(60.96, -42) * mm, "radius": 0.87 * mm});
            skCircle(sketch, "E1.24.4.0", {"center": v(60.96, -56) * mm, "radius": 0.87 * mm});
            skCircle(sketch, "E1.24.5.0", {"center": v(60.96, -70) * mm, "radius": 0.87 * mm});
            skCircle(sketch, "E1.24.6.0", {"center": v(60.96, -84) * mm, "radius": 0.87 * mm});
            skCircle(sketch, "E1.24.7.0", {"center": v(60.96, -98) * mm, "radius": 0.87 * mm});
            skCircle(sketch, "E1.24.8.0", {"center": v(60.96, -112) * mm, "radius": 0.87 * mm});
            skCircle(sketch, "E1.24.9.0", {"center": v(60.96, -126) * mm, "radius": 0.87 * mm});
            skCircle(sketch, "E1.24.10.0", {"center": v(60.96, -140) * mm, "radius": 0.87 * mm});
            skCircle(sketch, "E1.24.11.0", {"center": v(60.96, -154) * mm, "radius": 0.87 * mm});
            skCircle(sketch, "E1.24.12.0", {"center": v(60.96, -168) * mm, "radius": 0.87 * mm});
            skCircle(sketch, "E1.24.13.0", {"center": v(60.96, -182) * mm, "radius": 0.87 * mm});
            skCircle(sketch, "E1.24.14.0", {"center": v(60.96, -196) * mm, "radius": 0.87 * mm});
            skCircle(sketch, "E1.24.15.0", {"center": v(60.96, -210) * mm, "radius": 0.87 * mm});
            skCircle(sketch, "E1.24.16.0", {"center": v(60.96, -224) * mm, "radius": 0.87 * mm});
            skCircle(sketch, "E1.24.17.0", {"center": v(60.96, -238) * mm, "radius": 0.87 * mm});
            skCircle(sketch, "E1.24.18.0", {"center": v(60.96, -252) * mm, "radius": 0.87 * mm});
            skCircle(sketch, "E1.25.0.0", {"center": v(63.5, 0) * mm, "radius": 0.87 * mm});
            skCircle(sketch, "E1.25.1.0", {"center": v(63.5, -14) * mm, "radius": 0.87 * mm});
            skCircle(sketch, "E1.25.2.0", {"center": v(63.5, -28) * mm, "radius": 0.87 * mm});
            skCircle(sketch, "E1.25.3.0", {"center": v(63.5, -42) * mm, "radius": 0.87 * mm});
            skCircle(sketch, "E1.25.4.0", {"center": v(63.5, -56) * mm, "radius": 0.87 * mm});
            skCircle(sketch, "E1.25.5.0", {"center": v(63.5, -70) * mm, "radius": 0.87 * mm});
            skCircle(sketch, "E1.25.6.0", {"center": v(63.5, -84) * mm, "radius": 0.87 * mm});
            skCircle(sketch, "E1.25.7.0", {"center": v(63.5, -98) * mm, "radius": 0.87 * mm});
            skCircle(sketch, "E1.25.8.0", {"center": v(63.5, -112) * mm, "radius": 0.87 * mm});
            skCircle(sketch, "E1.25.9.0", {"center": v(63.5, -126) * mm, "radius": 0.87 * mm});
            skCircle(sketch, "E1.25.10.0", {"center": v(63.5, -140) * mm, "radius": 0.87 * mm});
            skCircle(sketch, "E1.25.11.0", {"center": v(63.5, -154) * mm, "radius": 0.87 * mm});
            skCircle(sketch, "E1.25.12.0", {"center": v(63.5, -168) * mm, "radius": 0.87 * mm});
            skCircle(sketch, "E1.25.13.0", {"center": v(63.5, -182) * mm, "radius": 0.87 * mm});
            skCircle(sketch, "E1.25.14.0", {"center": v(63.5, -196) * mm, "radius": 0.87 * mm});
            skCircle(sketch, "E1.25.15.0", {"center": v(63.5, -210) * mm, "radius": 0.87 * mm});
            skCircle(sketch, "E1.25.16.0", {"center": v(63.5, -224) * mm, "radius": 0.87 * mm});
            skCircle(sketch, "E1.25.17.0", {"center": v(63.5, -238) * mm, "radius": 0.87 * mm});
            skCircle(sketch, "E1.25.18.0", {"center": v(63.5, -252) * mm, "radius": 0.87 * mm});
            skCircle(sketch, "E1.26.0.0", {"center": v(66.04, 0) * mm, "radius": 0.87 * mm});
            skCircle(sketch, "E1.26.1.0", {"center": v(66.04, -14) * mm, "radius": 0.87 * mm});
            skCircle(sketch, "E1.26.2.0", {"center": v(66.04, -28) * mm, "radius": 0.87 * mm});
            skCircle(sketch, "E1.26.3.0", {"center": v(66.04, -42) * mm, "radius": 0.87 * mm});
            skCircle(sketch, "E1.26.4.0", {"center": v(66.04, -56) * mm, "radius": 0.87 * mm});
            skCircle(sketch, "E1.26.5.0", {"center": v(66.04, -70) * mm, "radius": 0.87 * mm});
            skCircle(sketch, "E1.26.6.0", {"center": v(66.04, -84) * mm, "radius": 0.87 * mm});
            skCircle(sketch, "E1.26.7.0", {"center": v(66.04, -98) * mm, "radius": 0.87 * mm});
            skCircle(sketch, "E1.26.8.0", {"center": v(66.04, -112) * mm, "radius": 0.87 * mm});
            skCircle(sketch, "E1.26.9.0", {"center": v(66.04, -126) * mm, "radius": 0.87 * mm});
            skCircle(sketch, "E1.26.10.0", {"center": v(66.04, -140) * mm, "radius": 0.87 * mm});
            skCircle(sketch, "E1.26.11.0", {"center": v(66.04, -154) * mm, "radius": 0.87 * mm});
            skCircle(sketch, "E1.26.12.0", {"center": v(66.04, -168) * mm, "radius": 0.87 * mm});
            skCircle(sketch, "E1.26.13.0", {"center": v(66.04, -182) * mm, "radius": 0.87 * mm});
            skCircle(sketch, "E1.26.14.0", {"center": v(66.04, -196) * mm, "radius": 0.87 * mm});
            skCircle(sketch, "E1.26.15.0", {"center": v(66.04, -210) * mm, "radius": 0.87 * mm});
            skCircle(sketch, "E1.26.16.0", {"center": v(66.04, -224) * mm, "radius": 0.87 * mm});
            skCircle(sketch, "E1.26.17.0", {"center": v(66.04, -238) * mm, "radius": 0.87 * mm});
            skCircle(sketch, "E1.26.18.0", {"center": v(66.04, -252) * mm, "radius": 0.87 * mm});
            skCircle(sketch, "E1.27.0.0", {"center": v(68.58, 0) * mm, "radius": 0.87 * mm});
            skCircle(sketch, "E1.27.1.0", {"center": v(68.58, -14) * mm, "radius": 0.87 * mm});
            skCircle(sketch, "E1.27.2.0", {"center": v(68.58, -28) * mm, "radius": 0.87 * mm});
            skCircle(sketch, "E1.27.3.0", {"center": v(68.58, -42) * mm, "radius": 0.87 * mm});
            skCircle(sketch, "E1.27.4.0", {"center": v(68.58, -56) * mm, "radius": 0.87 * mm});
            skCircle(sketch, "E1.27.5.0", {"center": v(68.58, -70) * mm, "radius": 0.87 * mm});
            skCircle(sketch, "E1.27.6.0", {"center": v(68.58, -84) * mm, "radius": 0.87 * mm});
            skCircle(sketch, "E1.27.7.0", {"center": v(68.58, -98) * mm, "radius": 0.87 * mm});
            skCircle(sketch, "E1.27.8.0", {"center": v(68.58, -112) * mm, "radius": 0.87 * mm});
            skCircle(sketch, "E1.27.9.0", {"center": v(68.58, -126) * mm, "radius": 0.87 * mm});
            skCircle(sketch, "E1.27.10.0", {"center": v(68.58, -140) * mm, "radius": 0.87 * mm});
            skCircle(sketch, "E1.27.11.0", {"center": v(68.58, -154) * mm, "radius": 0.87 * mm});
            skCircle(sketch, "E1.27.12.0", {"center": v(68.58, -168) * mm, "radius": 0.87 * mm});
            skCircle(sketch, "E1.27.13.0", {"center": v(68.58, -182) * mm, "radius": 0.87 * mm});
            skCircle(sketch, "E1.27.14.0", {"center": v(68.58, -196) * mm, "radius": 0.87 * mm});
            skCircle(sketch, "E1.27.15.0", {"center": v(68.58, -210) * mm, "radius": 0.87 * mm});
            skCircle(sketch, "E1.27.16.0", {"center": v(68.58, -224) * mm, "radius": 0.87 * mm});
            skCircle(sketch, "E1.27.17.0", {"center": v(68.58, -238) * mm, "radius": 0.87 * mm});
            skCircle(sketch, "E1.27.18.0", {"center": v(68.58, -252) * mm, "radius": 0.87 * mm});
            skCircle(sketch, "E1.28.0.0", {"center": v(71.12, 0) * mm, "radius": 0.87 * mm});
            skCircle(sketch, "E1.28.1.0", {"center": v(71.12, -14) * mm, "radius": 0.87 * mm});
            skCircle(sketch, "E1.28.2.0", {"center": v(71.12, -28) * mm, "radius": 0.87 * mm});
            skCircle(sketch, "E1.28.3.0", {"center": v(71.12, -42) * mm, "radius": 0.87 * mm});
            skCircle(sketch, "E1.28.4.0", {"center": v(71.12, -56) * mm, "radius": 0.87 * mm});
            skCircle(sketch, "E1.28.5.0", {"center": v(71.12, -70) * mm, "radius": 0.87 * mm});
            skCircle(sketch, "E1.28.6.0", {"center": v(71.12, -84) * mm, "radius": 0.87 * mm});
            skCircle(sketch, "E1.28.7.0", {"center": v(71.12, -98) * mm, "radius": 0.87 * mm});
            skCircle(sketch, "E1.28.8.0", {"center": v(71.12, -112) * mm, "radius": 0.87 * mm});
            skCircle(sketch, "E1.28.9.0", {"center": v(71.12, -126) * mm, "radius": 0.87 * mm});
            skCircle(sketch, "E1.28.10.0", {"center": v(71.12, -140) * mm, "radius": 0.87 * mm});
            skCircle(sketch, "E1.28.11.0", {"center": v(71.12, -154) * mm, "radius": 0.87 * mm});
            skCircle(sketch, "E1.28.12.0", {"center": v(71.12, -168) * mm, "radius": 0.87 * mm});
            skCircle(sketch, "E1.28.13.0", {"center": v(71.12, -182) * mm, "radius": 0.87 * mm});
            skCircle(sketch, "E1.28.14.0", {"center": v(71.12, -196) * mm, "radius": 0.87 * mm});
            skCircle(sketch, "E1.28.15.0", {"center": v(71.12, -210) * mm, "radius": 0.87 * mm});
            skCircle(sketch, "E1.28.16.0", {"center": v(71.12, -224) * mm, "radius": 0.87 * mm});
            skCircle(sketch, "E1.28.17.0", {"center": v(71.12, -238) * mm, "radius": 0.87 * mm});
            skCircle(sketch, "E1.28.18.0", {"center": v(71.12, -252) * mm, "radius": 0.87 * mm});
            skCircle(sketch, "E1.29.0.0", {"center": v(73.66, 0) * mm, "radius": 0.87 * mm});
            skCircle(sketch, "E1.29.1.0", {"center": v(73.66, -14) * mm, "radius": 0.87 * mm});
            skCircle(sketch, "E1.29.2.0", {"center": v(73.66, -28) * mm, "radius": 0.87 * mm});
            skCircle(sketch, "E1.29.3.0", {"center": v(73.66, -42) * mm, "radius": 0.87 * mm});
            skCircle(sketch, "E1.29.4.0", {"center": v(73.66, -56) * mm, "radius": 0.87 * mm});
            skCircle(sketch, "E1.29.5.0", {"center": v(73.66, -70) * mm, "radius": 0.87 * mm});
            skCircle(sketch, "E1.29.6.0", {"center": v(73.66, -84) * mm, "radius": 0.87 * mm});
            skCircle(sketch, "E1.29.7.0", {"center": v(73.66, -98) * mm, "radius": 0.87 * mm});
            skCircle(sketch, "E1.29.8.0", {"center": v(73.66, -112) * mm, "radius": 0.87 * mm});
            skCircle(sketch, "E1.29.9.0", {"center": v(73.66, -126) * mm, "radius": 0.87 * mm});
            skCircle(sketch, "E1.29.10.0", {"center": v(73.66, -140) * mm, "radius": 0.87 * mm});
            skCircle(sketch, "E1.29.11.0", {"center": v(73.66, -154) * mm, "radius": 0.87 * mm});
            skCircle(sketch, "E1.29.12.0", {"center": v(73.66, -168) * mm, "radius": 0.87 * mm});
            skCircle(sketch, "E1.29.13.0", {"center": v(73.66, -182) * mm, "radius": 0.87 * mm});
            skCircle(sketch, "E1.29.14.0", {"center": v(73.66, -196) * mm, "radius": 0.87 * mm});
            skCircle(sketch, "E1.29.15.0", {"center": v(73.66, -210) * mm, "radius": 0.87 * mm});
            skCircle(sketch, "E1.29.16.0", {"center": v(73.66, -224) * mm, "radius": 0.87 * mm});
            skCircle(sketch, "E1.29.17.0", {"center": v(73.66, -238) * mm, "radius": 0.87 * mm});
            skCircle(sketch, "E1.29.18.0", {"center": v(73.66, -252) * mm, "radius": 0.87 * mm});
            skCircle(sketch, "E1.30.0.0", {"center": v(76.2, 0) * mm, "radius": 0.87 * mm});
            skCircle(sketch, "E1.30.1.0", {"center": v(76.2, -14) * mm, "radius": 0.87 * mm});
            skCircle(sketch, "E1.30.2.0", {"center": v(76.2, -28) * mm, "radius": 0.87 * mm});
            skCircle(sketch, "E1.30.3.0", {"center": v(76.2, -42) * mm, "radius": 0.87 * mm});
            skCircle(sketch, "E1.30.4.0", {"center": v(76.2, -56) * mm, "radius": 0.87 * mm});
            skCircle(sketch, "E1.30.5.0", {"center": v(76.2, -70) * mm, "radius": 0.87 * mm});
            skCircle(sketch, "E1.30.6.0", {"center": v(76.2, -84) * mm, "radius": 0.87 * mm});
            skCircle(sketch, "E1.30.7.0", {"center": v(76.2, -98) * mm, "radius": 0.87 * mm});
            skCircle(sketch, "E1.30.8.0", {"center": v(76.2, -112) * mm, "radius": 0.87 * mm});
            skCircle(sketch, "E1.30.9.0", {"center": v(76.2, -126) * mm, "radius": 0.87 * mm});
            skCircle(sketch, "E1.30.10.0", {"center": v(76.2, -140) * mm, "radius": 0.87 * mm});
            skCircle(sketch, "E1.30.11.0", {"center": v(76.2, -154) * mm, "radius": 0.87 * mm});
            skCircle(sketch, "E1.30.12.0", {"center": v(76.2, -168) * mm, "radius": 0.87 * mm});
            skCircle(sketch, "E1.30.13.0", {"center": v(76.2, -182) * mm, "radius": 0.87 * mm});
            skCircle(sketch, "E1.30.14.0", {"center": v(76.2, -196) * mm, "radius": 0.87 * mm});
            skCircle(sketch, "E1.30.15.0", {"center": v(76.2, -210) * mm, "radius": 0.87 * mm});
            skCircle(sketch, "E1.30.16.0", {"center": v(76.2, -224) * mm, "radius": 0.87 * mm});
            skCircle(sketch, "E1.30.17.0", {"center": v(76.2, -238) * mm, "radius": 0.87 * mm});
            skCircle(sketch, "E1.30.18.0", {"center": v(76.2, -252) * mm, "radius": 0.87 * mm});
            skCircle(sketch, "E1.31.0.0", {"center": v(78.74, 0) * mm, "radius": 0.87 * mm});
            skCircle(sketch, "E1.31.1.0", {"center": v(78.74, -14) * mm, "radius": 0.87 * mm});
            skCircle(sketch, "E1.31.2.0", {"center": v(78.74, -28) * mm, "radius": 0.87 * mm});
            skCircle(sketch, "E1.31.3.0", {"center": v(78.74, -42) * mm, "radius": 0.87 * mm});
            skCircle(sketch, "E1.31.4.0", {"center": v(78.74, -56) * mm, "radius": 0.87 * mm});
            skCircle(sketch, "E1.31.5.0", {"center": v(78.74, -70) * mm, "radius": 0.87 * mm});
            skCircle(sketch, "E1.31.6.0", {"center": v(78.74, -84) * mm, "radius": 0.87 * mm});
            skCircle(sketch, "E1.31.7.0", {"center": v(78.74, -98) * mm, "radius": 0.87 * mm});
            skCircle(sketch, "E1.31.8.0", {"center": v(78.74, -112) * mm, "radius": 0.87 * mm});
            skCircle(sketch, "E1.31.9.0", {"center": v(78.74, -126) * mm, "radius": 0.87 * mm});
            skCircle(sketch, "E1.31.10.0", {"center": v(78.74, -140) * mm, "radius": 0.87 * mm});
            skCircle(sketch, "E1.31.11.0", {"center": v(78.74, -154) * mm, "radius": 0.87 * mm});
            skCircle(sketch, "E1.31.12.0", {"center": v(78.74, -168) * mm, "radius": 0.87 * mm});
            skCircle(sketch, "E1.31.13.0", {"center": v(78.74, -182) * mm, "radius": 0.87 * mm});
            skCircle(sketch, "E1.31.14.0", {"center": v(78.74, -196) * mm, "radius": 0.87 * mm});
            skCircle(sketch, "E1.31.15.0", {"center": v(78.74, -210) * mm, "radius": 0.87 * mm});
            skCircle(sketch, "E1.31.16.0", {"center": v(78.74, -224) * mm, "radius": 0.87 * mm});
            skCircle(sketch, "E1.31.17.0", {"center": v(78.74, -238) * mm, "radius": 0.87 * mm});
            skCircle(sketch, "E1.31.18.0", {"center": v(78.74, -252) * mm, "radius": 0.87 * mm});
            skCircle(sketch, "E1.32.0.0", {"center": v(81.28, 0) * mm, "radius": 0.87 * mm});
            skCircle(sketch, "E1.32.1.0", {"center": v(81.28, -14) * mm, "radius": 0.87 * mm});
            skCircle(sketch, "E1.32.2.0", {"center": v(81.28, -28) * mm, "radius": 0.87 * mm});
            skCircle(sketch, "E1.32.3.0", {"center": v(81.28, -42) * mm, "radius": 0.87 * mm});
            skCircle(sketch, "E1.32.4.0", {"center": v(81.28, -56) * mm, "radius": 0.87 * mm});
            skCircle(sketch, "E1.32.5.0", {"center": v(81.28, -70) * mm, "radius": 0.87 * mm});
            skCircle(sketch, "E1.32.6.0", {"center": v(81.28, -84) * mm, "radius": 0.87 * mm});
            skCircle(sketch, "E1.32.7.0", {"center": v(81.28, -98) * mm, "radius": 0.87 * mm});
            skCircle(sketch, "E1.32.8.0", {"center": v(81.28, -112) * mm, "radius": 0.87 * mm});
            skCircle(sketch, "E1.32.9.0", {"center": v(81.28, -126) * mm, "radius": 0.87 * mm});
            skCircle(sketch, "E1.32.10.0", {"center": v(81.28, -140) * mm, "radius": 0.87 * mm});
            skCircle(sketch, "E1.32.11.0", {"center": v(81.28, -154) * mm, "radius": 0.87 * mm});
            skCircle(sketch, "E1.32.12.0", {"center": v(81.28, -168) * mm, "radius": 0.87 * mm});
            skCircle(sketch, "E1.32.13.0", {"center": v(81.28, -182) * mm, "radius": 0.87 * mm});
            skCircle(sketch, "E1.32.14.0", {"center": v(81.28, -196) * mm, "radius": 0.87 * mm});
            skCircle(sketch, "E1.32.15.0", {"center": v(81.28, -210) * mm, "radius": 0.87 * mm});
            skCircle(sketch, "E1.32.16.0", {"center": v(81.28, -224) * mm, "radius": 0.87 * mm});
            skCircle(sketch, "E1.32.17.0", {"center": v(81.28, -238) * mm, "radius": 0.87 * mm});
            skCircle(sketch, "E1.32.18.0", {"center": v(81.28, -252) * mm, "radius": 0.87 * mm});
            skCircle(sketch, "E1.33.0.0", {"center": v(83.82, 0) * mm, "radius": 0.87 * mm});
            skCircle(sketch, "E1.33.1.0", {"center": v(83.82, -14) * mm, "radius": 0.87 * mm});
            skCircle(sketch, "E1.33.2.0", {"center": v(83.82, -28) * mm, "radius": 0.87 * mm});
            skCircle(sketch, "E1.33.3.0", {"center": v(83.82, -42) * mm, "radius": 0.87 * mm});
            skCircle(sketch, "E1.33.4.0", {"center": v(83.82, -56) * mm, "radius": 0.87 * mm});
            skCircle(sketch, "E1.33.5.0", {"center": v(83.82, -70) * mm, "radius": 0.87 * mm});
            skCircle(sketch, "E1.33.6.0", {"center": v(83.82, -84) * mm, "radius": 0.87 * mm});
            skCircle(sketch, "E1.33.7.0", {"center": v(83.82, -98) * mm, "radius": 0.87 * mm});
            skCircle(sketch, "E1.33.8.0", {"center": v(83.82, -112) * mm, "radius": 0.87 * mm});
            skCircle(sketch, "E1.33.9.0", {"center": v(83.82, -126) * mm, "radius": 0.87 * mm});
            skCircle(sketch, "E1.33.10.0", {"center": v(83.82, -140) * mm, "radius": 0.87 * mm});
            skCircle(sketch, "E1.33.11.0", {"center": v(83.82, -154) * mm, "radius": 0.87 * mm});
            skCircle(sketch, "E1.33.12.0", {"center": v(83.82, -168) * mm, "radius": 0.87 * mm});
            skCircle(sketch, "E1.33.13.0", {"center": v(83.82, -182) * mm, "radius": 0.87 * mm});
            skCircle(sketch, "E1.33.14.0", {"center": v(83.82, -196) * mm, "radius": 0.87 * mm});
            skCircle(sketch, "E1.33.15.0", {"center": v(83.82, -210) * mm, "radius": 0.87 * mm});
            skCircle(sketch, "E1.33.16.0", {"center": v(83.82, -224) * mm, "radius": 0.87 * mm});
            skCircle(sketch, "E1.33.17.0", {"center": v(83.82, -238) * mm, "radius": 0.87 * mm});
            skCircle(sketch, "E1.33.18.0", {"center": v(83.82, -252) * mm, "radius": 0.87 * mm});
            skCircle(sketch, "E1.34.0.0", {"center": v(86.36, 0) * mm, "radius": 0.87 * mm});
            skCircle(sketch, "E1.34.1.0", {"center": v(86.36, -14) * mm, "radius": 0.87 * mm});
            skCircle(sketch, "E1.34.2.0", {"center": v(86.36, -28) * mm, "radius": 0.87 * mm});
            skCircle(sketch, "E1.34.3.0", {"center": v(86.36, -42) * mm, "radius": 0.87 * mm});
            skCircle(sketch, "E1.34.4.0", {"center": v(86.36, -56) * mm, "radius": 0.87 * mm});
            skCircle(sketch, "E1.34.5.0", {"center": v(86.36, -70) * mm, "radius": 0.87 * mm});
            skCircle(sketch, "E1.34.6.0", {"center": v(86.36, -84) * mm, "radius": 0.87 * mm});
            skCircle(sketch, "E1.34.7.0", {"center": v(86.36, -98) * mm, "radius": 0.87 * mm});
            skCircle(sketch, "E1.34.8.0", {"center": v(86.36, -112) * mm, "radius": 0.87 * mm});
            skCircle(sketch, "E1.34.9.0", {"center": v(86.36, -126) * mm, "radius": 0.87 * mm});
            skCircle(sketch, "E1.34.10.0", {"center": v(86.36, -140) * mm, "radius": 0.87 * mm});
            skCircle(sketch, "E1.34.11.0", {"center": v(86.36, -154) * mm, "radius": 0.87 * mm});
            skCircle(sketch, "E1.34.12.0", {"center": v(86.36, -168) * mm, "radius": 0.87 * mm});
            skCircle(sketch, "E1.34.13.0", {"center": v(86.36, -182) * mm, "radius": 0.87 * mm});
            skCircle(sketch, "E1.34.14.0", {"center": v(86.36, -196) * mm, "radius": 0.87 * mm});
            skCircle(sketch, "E1.34.15.0", {"center": v(86.36, -210) * mm, "radius": 0.87 * mm});
            skCircle(sketch, "E1.34.16.0", {"center": v(86.36, -224) * mm, "radius": 0.87 * mm});
            skCircle(sketch, "E1.34.17.0", {"center": v(86.36, -238) * mm, "radius": 0.87 * mm});
            skCircle(sketch, "E1.34.18.0", {"center": v(86.36, -252) * mm, "radius": 0.87 * mm});
            skCircle(sketch, "E1.35.0.0", {"center": v(88.9, 0) * mm, "radius": 0.87 * mm});
            skCircle(sketch, "E1.35.1.0", {"center": v(88.9, -14) * mm, "radius": 0.87 * mm});
            skCircle(sketch, "E1.35.2.0", {"center": v(88.9, -28) * mm, "radius": 0.87 * mm});
            skCircle(sketch, "E1.35.3.0", {"center": v(88.9, -42) * mm, "radius": 0.87 * mm});
            skCircle(sketch, "E1.35.4.0", {"center": v(88.9, -56) * mm, "radius": 0.87 * mm});
            skCircle(sketch, "E1.35.5.0", {"center": v(88.9, -70) * mm, "radius": 0.87 * mm});
            skCircle(sketch, "E1.35.6.0", {"center": v(88.9, -84) * mm, "radius": 0.87 * mm});
            skCircle(sketch, "E1.35.7.0", {"center": v(88.9, -98) * mm, "radius": 0.87 * mm});
            skCircle(sketch, "E1.35.8.0", {"center": v(88.9, -112) * mm, "radius": 0.87 * mm});
            skCircle(sketch, "E1.35.9.0", {"center": v(88.9, -126) * mm, "radius": 0.87 * mm});
            skCircle(sketch, "E1.35.10.0", {"center": v(88.9, -140) * mm, "radius": 0.87 * mm});
            skCircle(sketch, "E1.35.11.0", {"center": v(88.9, -154) * mm, "radius": 0.87 * mm});
            skCircle(sketch, "E1.35.12.0", {"center": v(88.9, -168) * mm, "radius": 0.87 * mm});
            skCircle(sketch, "E1.35.13.0", {"center": v(88.9, -182) * mm, "radius": 0.87 * mm});
            skCircle(sketch, "E1.35.14.0", {"center": v(88.9, -196) * mm, "radius": 0.87 * mm});
            skCircle(sketch, "E1.35.15.0", {"center": v(88.9, -210) * mm, "radius": 0.87 * mm});
            skCircle(sketch, "E1.35.16.0", {"center": v(88.9, -224) * mm, "radius": 0.87 * mm});
            skCircle(sketch, "E1.35.17.0", {"center": v(88.9, -238) * mm, "radius": 0.87 * mm});
            skCircle(sketch, "E1.35.18.0", {"center": v(88.9, -252) * mm, "radius": 0.87 * mm});
            skCircle(sketch, "E1.36.0.0", {"center": v(91.44, 0) * mm, "radius": 0.87 * mm});
            skCircle(sketch, "E1.36.1.0", {"center": v(91.44, -14) * mm, "radius": 0.87 * mm});
            skCircle(sketch, "E1.36.2.0", {"center": v(91.44, -28) * mm, "radius": 0.87 * mm});
            skCircle(sketch, "E1.36.3.0", {"center": v(91.44, -42) * mm, "radius": 0.87 * mm});
            skCircle(sketch, "E1.36.4.0", {"center": v(91.44, -56) * mm, "radius": 0.87 * mm});
            skCircle(sketch, "E1.36.5.0", {"center": v(91.44, -70) * mm, "radius": 0.87 * mm});
            skCircle(sketch, "E1.36.6.0", {"center": v(91.44, -84) * mm, "radius": 0.87 * mm});
            skCircle(sketch, "E1.36.7.0", {"center": v(91.44, -98) * mm, "radius": 0.87 * mm});
            skCircle(sketch, "E1.36.8.0", {"center": v(91.44, -112) * mm, "radius": 0.87 * mm});
            skCircle(sketch, "E1.36.9.0", {"center": v(91.44, -126) * mm, "radius": 0.87 * mm});
            skCircle(sketch, "E1.36.10.0", {"center": v(91.44, -140) * mm, "radius": 0.87 * mm});
            skCircle(sketch, "E1.36.11.0", {"center": v(91.44, -154) * mm, "radius": 0.87 * mm});
            skCircle(sketch, "E1.36.12.0", {"center": v(91.44, -168) * mm, "radius": 0.87 * mm});
            skCircle(sketch, "E1.36.13.0", {"center": v(91.44, -182) * mm, "radius": 0.87 * mm});
            skCircle(sketch, "E1.36.14.0", {"center": v(91.44, -196) * mm, "radius": 0.87 * mm});
            skCircle(sketch, "E1.36.15.0", {"center": v(91.44, -210) * mm, "radius": 0.87 * mm});
            skCircle(sketch, "E1.36.16.0", {"center": v(91.44, -224) * mm, "radius": 0.87 * mm});
            skCircle(sketch, "E1.36.17.0", {"center": v(91.44, -238) * mm, "radius": 0.87 * mm});
            skCircle(sketch, "E1.36.18.0", {"center": v(91.44, -252) * mm, "radius": 0.87 * mm});
            skCircle(sketch, "E1.37.0.0", {"center": v(93.98, 0) * mm, "radius": 0.87 * mm});
            skCircle(sketch, "E1.37.1.0", {"center": v(93.98, -14) * mm, "radius": 0.87 * mm});
            skCircle(sketch, "E1.37.2.0", {"center": v(93.98, -28) * mm, "radius": 0.87 * mm});
            skCircle(sketch, "E1.37.3.0", {"center": v(93.98, -42) * mm, "radius": 0.87 * mm});
            skCircle(sketch, "E1.37.4.0", {"center": v(93.98, -56) * mm, "radius": 0.87 * mm});
            skCircle(sketch, "E1.37.5.0", {"center": v(93.98, -70) * mm, "radius": 0.87 * mm});
            skCircle(sketch, "E1.37.6.0", {"center": v(93.98, -84) * mm, "radius": 0.87 * mm});
            skCircle(sketch, "E1.37.7.0", {"center": v(93.98, -98) * mm, "radius": 0.87 * mm});
            skCircle(sketch, "E1.37.8.0", {"center": v(93.98, -112) * mm, "radius": 0.87 * mm});
            skCircle(sketch, "E1.37.9.0", {"center": v(93.98, -126) * mm, "radius": 0.87 * mm});
            skCircle(sketch, "E1.37.10.0", {"center": v(93.98, -140) * mm, "radius": 0.87 * mm});
            skCircle(sketch, "E1.37.11.0", {"center": v(93.98, -154) * mm, "radius": 0.87 * mm});
            skCircle(sketch, "E1.37.12.0", {"center": v(93.98, -168) * mm, "radius": 0.87 * mm});
            skCircle(sketch, "E1.37.13.0", {"center": v(93.98, -182) * mm, "radius": 0.87 * mm});
            skCircle(sketch, "E1.37.14.0", {"center": v(93.98, -196) * mm, "radius": 0.87 * mm});
            skCircle(sketch, "E1.37.15.0", {"center": v(93.98, -210) * mm, "radius": 0.87 * mm});
            skCircle(sketch, "E1.37.16.0", {"center": v(93.98, -224) * mm, "radius": 0.87 * mm});
            skCircle(sketch, "E1.37.17.0", {"center": v(93.98, -238) * mm, "radius": 0.87 * mm});
            skCircle(sketch, "E1.37.18.0", {"center": v(93.98, -252) * mm, "radius": 0.87 * mm});
            skCircle(sketch, "E1.38.0.0", {"center": v(96.52, 0) * mm, "radius": 0.87 * mm});
            skCircle(sketch, "E1.38.1.0", {"center": v(96.52, -14) * mm, "radius": 0.87 * mm});
            skCircle(sketch, "E1.38.2.0", {"center": v(96.52, -28) * mm, "radius": 0.87 * mm});
            skCircle(sketch, "E1.38.3.0", {"center": v(96.52, -42) * mm, "radius": 0.87 * mm});
            skCircle(sketch, "E1.38.4.0", {"center": v(96.52, -56) * mm, "radius": 0.87 * mm});
            skCircle(sketch, "E1.38.5.0", {"center": v(96.52, -70) * mm, "radius": 0.87 * mm});
            skCircle(sketch, "E1.38.6.0", {"center": v(96.52, -84) * mm, "radius": 0.87 * mm});
            skCircle(sketch, "E1.38.7.0", {"center": v(96.52, -98) * mm, "radius": 0.87 * mm});
            skCircle(sketch, "E1.38.8.0", {"center": v(96.52, -112) * mm, "radius": 0.87 * mm});
            skCircle(sketch, "E1.38.9.0", {"center": v(96.52, -126) * mm, "radius": 0.87 * mm});
            skCircle(sketch, "E1.38.10.0", {"center": v(96.52, -140) * mm, "radius": 0.87 * mm});
            skCircle(sketch, "E1.38.11.0", {"center": v(96.52, -154) * mm, "radius": 0.87 * mm});
            skCircle(sketch, "E1.38.12.0", {"center": v(96.52, -168) * mm, "radius": 0.87 * mm});
            skCircle(sketch, "E1.38.13.0", {"center": v(96.52, -182) * mm, "radius": 0.87 * mm});
            skCircle(sketch, "E1.38.14.0", {"center": v(96.52, -196) * mm, "radius": 0.87 * mm});
            skCircle(sketch, "E1.38.15.0", {"center": v(96.52, -210) * mm, "radius": 0.87 * mm});
            skCircle(sketch, "E1.38.16.0", {"center": v(96.52, -224) * mm, "radius": 0.87 * mm});
            skCircle(sketch, "E1.38.17.0", {"center": v(96.52, -238) * mm, "radius": 0.87 * mm});
            skCircle(sketch, "E1.38.18.0", {"center": v(96.52, -252) * mm, "radius": 0.87 * mm});
            skCircle(sketch, "E1.39.0.0", {"center": v(99.06, 0) * mm, "radius": 0.87 * mm});
            skCircle(sketch, "E1.39.1.0", {"center": v(99.06, -14) * mm, "radius": 0.87 * mm});
            skCircle(sketch, "E1.39.2.0", {"center": v(99.06, -28) * mm, "radius": 0.87 * mm});
            skCircle(sketch, "E1.39.3.0", {"center": v(99.06, -42) * mm, "radius": 0.87 * mm});
            skCircle(sketch, "E1.39.4.0", {"center": v(99.06, -56) * mm, "radius": 0.87 * mm});
            skCircle(sketch, "E1.39.5.0", {"center": v(99.06, -70) * mm, "radius": 0.87 * mm});
            skCircle(sketch, "E1.39.6.0", {"center": v(99.06, -84) * mm, "radius": 0.87 * mm});
            skCircle(sketch, "E1.39.7.0", {"center": v(99.06, -98) * mm, "radius": 0.87 * mm});
            skCircle(sketch, "E1.39.8.0", {"center": v(99.06, -112) * mm, "radius": 0.87 * mm});
            skCircle(sketch, "E1.39.9.0", {"center": v(99.06, -126) * mm, "radius": 0.87 * mm});
            skCircle(sketch, "E1.39.10.0", {"center": v(99.06, -140) * mm, "radius": 0.87 * mm});
            skCircle(sketch, "E1.39.11.0", {"center": v(99.06, -154) * mm, "radius": 0.87 * mm});
            skCircle(sketch, "E1.39.12.0", {"center": v(99.06, -168) * mm, "radius": 0.87 * mm});
            skCircle(sketch, "E1.39.13.0", {"center": v(99.06, -182) * mm, "radius": 0.87 * mm});
            skCircle(sketch, "E1.39.14.0", {"center": v(99.06, -196) * mm, "radius": 0.87 * mm});
            skCircle(sketch, "E1.39.15.0", {"center": v(99.06, -210) * mm, "radius": 0.87 * mm});
            skCircle(sketch, "E1.39.16.0", {"center": v(99.06, -224) * mm, "radius": 0.87 * mm});
            skCircle(sketch, "E1.39.17.0", {"center": v(99.06, -238) * mm, "radius": 0.87 * mm});
            skCircle(sketch, "E1.39.18.0", {"center": v(99.06, -252) * mm, "radius": 0.87 * mm});
            skCircle(sketch, "E1.40.0.0", {"center": v(101.6, 0) * mm, "radius": 0.87 * mm});
            skCircle(sketch, "E1.40.1.0", {"center": v(101.6, -14) * mm, "radius": 0.87 * mm});
            skCircle(sketch, "E1.40.2.0", {"center": v(101.6, -28) * mm, "radius": 0.87 * mm});
            skCircle(sketch, "E1.40.3.0", {"center": v(101.6, -42) * mm, "radius": 0.87 * mm});
            skCircle(sketch, "E1.40.4.0", {"center": v(101.6, -56) * mm, "radius": 0.87 * mm});
            skCircle(sketch, "E1.40.5.0", {"center": v(101.6, -70) * mm, "radius": 0.87 * mm});
            skCircle(sketch, "E1.40.6.0", {"center": v(101.6, -84) * mm, "radius": 0.87 * mm});
            skCircle(sketch, "E1.40.7.0", {"center": v(101.6, -98) * mm, "radius": 0.87 * mm});
            skCircle(sketch, "E1.40.8.0", {"center": v(101.6, -112) * mm, "radius": 0.87 * mm});
            skCircle(sketch, "E1.40.9.0", {"center": v(101.6, -126) * mm, "radius": 0.87 * mm});
            skCircle(sketch, "E1.40.10.0", {"center": v(101.6, -140) * mm, "radius": 0.87 * mm});
            skCircle(sketch, "E1.40.11.0", {"center": v(101.6, -154) * mm, "radius": 0.87 * mm});
            skCircle(sketch, "E1.40.12.0", {"center": v(101.6, -168) * mm, "radius": 0.87 * mm});
            skCircle(sketch, "E1.40.13.0", {"center": v(101.6, -182) * mm, "radius": 0.87 * mm});
            skCircle(sketch, "E1.40.14.0", {"center": v(101.6, -196) * mm, "radius": 0.87 * mm});
            skCircle(sketch, "E1.40.15.0", {"center": v(101.6, -210) * mm, "radius": 0.87 * mm});
            skCircle(sketch, "E1.40.16.0", {"center": v(101.6, -224) * mm, "radius": 0.87 * mm});
            skCircle(sketch, "E1.40.17.0", {"center": v(101.6, -238) * mm, "radius": 0.87 * mm});
            skCircle(sketch, "E1.40.18.0", {"center": v(101.6, -252) * mm, "radius": 0.87 * mm});
            skCircle(sketch, "E1.41.0.0", {"center": v(104.14, 0) * mm, "radius": 0.87 * mm});
            skCircle(sketch, "E1.41.1.0", {"center": v(104.14, -14) * mm, "radius": 0.87 * mm});
            skCircle(sketch, "E1.41.2.0", {"center": v(104.14, -28) * mm, "radius": 0.87 * mm});
            skCircle(sketch, "E1.41.3.0", {"center": v(104.14, -42) * mm, "radius": 0.87 * mm});
            skCircle(sketch, "E1.41.4.0", {"center": v(104.14, -56) * mm, "radius": 0.87 * mm});
            skCircle(sketch, "E1.41.5.0", {"center": v(104.14, -70) * mm, "radius": 0.87 * mm});
            skCircle(sketch, "E1.41.6.0", {"center": v(104.14, -84) * mm, "radius": 0.87 * mm});
            skCircle(sketch, "E1.41.7.0", {"center": v(104.14, -98) * mm, "radius": 0.87 * mm});
            skCircle(sketch, "E1.41.8.0", {"center": v(104.14, -112) * mm, "radius": 0.87 * mm});
            skCircle(sketch, "E1.41.9.0", {"center": v(104.14, -126) * mm, "radius": 0.87 * mm});
            skCircle(sketch, "E1.41.10.0", {"center": v(104.14, -140) * mm, "radius": 0.87 * mm});
            skCircle(sketch, "E1.41.11.0", {"center": v(104.14, -154) * mm, "radius": 0.87 * mm});
            skCircle(sketch, "E1.41.12.0", {"center": v(104.14, -168) * mm, "radius": 0.87 * mm});
            skCircle(sketch, "E1.41.13.0", {"center": v(104.14, -182) * mm, "radius": 0.87 * mm});
            skCircle(sketch, "E1.41.14.0", {"center": v(104.14, -196) * mm, "radius": 0.87 * mm});
            skCircle(sketch, "E1.41.15.0", {"center": v(104.14, -210) * mm, "radius": 0.87 * mm});
            skCircle(sketch, "E1.41.16.0", {"center": v(104.14, -224) * mm, "radius": 0.87 * mm});
            skCircle(sketch, "E1.41.17.0", {"center": v(104.14, -238) * mm, "radius": 0.87 * mm});
            skCircle(sketch, "E1.41.18.0", {"center": v(104.14, -252) * mm, "radius": 0.87 * mm});
            skCircle(sketch, "E1.42.0.0", {"center": v(106.68, 0) * mm, "radius": 0.87 * mm});
            skCircle(sketch, "E1.42.1.0", {"center": v(106.68, -14) * mm, "radius": 0.87 * mm});
            skCircle(sketch, "E1.42.2.0", {"center": v(106.68, -28) * mm, "radius": 0.87 * mm});
            skCircle(sketch, "E1.42.3.0", {"center": v(106.68, -42) * mm, "radius": 0.87 * mm});
            skCircle(sketch, "E1.42.4.0", {"center": v(106.68, -56) * mm, "radius": 0.87 * mm});
            skCircle(sketch, "E1.42.5.0", {"center": v(106.68, -70) * mm, "radius": 0.87 * mm});
            skCircle(sketch, "E1.42.6.0", {"center": v(106.68, -84) * mm, "radius": 0.87 * mm});
            skCircle(sketch, "E1.42.7.0", {"center": v(106.68, -98) * mm, "radius": 0.87 * mm});
            skCircle(sketch, "E1.42.8.0", {"center": v(106.68, -112) * mm, "radius": 0.87 * mm});
            skCircle(sketch, "E1.42.9.0", {"center": v(106.68, -126) * mm, "radius": 0.87 * mm});
            skCircle(sketch, "E1.42.10.0", {"center": v(106.68, -140) * mm, "radius": 0.87 * mm});
            skCircle(sketch, "E1.42.11.0", {"center": v(106.68, -154) * mm, "radius": 0.87 * mm});
            skCircle(sketch, "E1.42.12.0", {"center": v(106.68, -168) * mm, "radius": 0.87 * mm});
            skCircle(sketch, "E1.42.13.0", {"center": v(106.68, -182) * mm, "radius": 0.87 * mm});
            skCircle(sketch, "E1.42.14.0", {"center": v(106.68, -196) * mm, "radius": 0.87 * mm});
            skCircle(sketch, "E1.42.15.0", {"center": v(106.68, -210) * mm, "radius": 0.87 * mm});
            skCircle(sketch, "E1.42.16.0", {"center": v(106.68, -224) * mm, "radius": 0.87 * mm});
            skCircle(sketch, "E1.42.17.0", {"center": v(106.68, -238) * mm, "radius": 0.87 * mm});
            skCircle(sketch, "E1.42.18.0", {"center": v(106.68, -252) * mm, "radius": 0.87 * mm});
            skCircle(sketch, "E1.43.0.0", {"center": v(109.22, 0) * mm, "radius": 0.87 * mm});
            skCircle(sketch, "E1.43.1.0", {"center": v(109.22, -14) * mm, "radius": 0.87 * mm});
            skCircle(sketch, "E1.43.2.0", {"center": v(109.22, -28) * mm, "radius": 0.87 * mm});
            skCircle(sketch, "E1.43.3.0", {"center": v(109.22, -42) * mm, "radius": 0.87 * mm});
            skCircle(sketch, "E1.43.4.0", {"center": v(109.22, -56) * mm, "radius": 0.87 * mm});
            skCircle(sketch, "E1.43.5.0", {"center": v(109.22, -70) * mm, "radius": 0.87 * mm});
            skCircle(sketch, "E1.43.6.0", {"center": v(109.22, -84) * mm, "radius": 0.87 * mm});
            skCircle(sketch, "E1.43.7.0", {"center": v(109.22, -98) * mm, "radius": 0.87 * mm});
            skCircle(sketch, "E1.43.8.0", {"center": v(109.22, -112) * mm, "radius": 0.87 * mm});
            skCircle(sketch, "E1.43.9.0", {"center": v(109.22, -126) * mm, "radius": 0.87 * mm});
            skCircle(sketch, "E1.43.10.0", {"center": v(109.22, -140) * mm, "radius": 0.87 * mm});
            skCircle(sketch, "E1.43.11.0", {"center": v(109.22, -154) * mm, "radius": 0.87 * mm});
            skCircle(sketch, "E1.43.12.0", {"center": v(109.22, -168) * mm, "radius": 0.87 * mm});
            skCircle(sketch, "E1.43.13.0", {"center": v(109.22, -182) * mm, "radius": 0.87 * mm});
            skCircle(sketch, "E1.43.14.0", {"center": v(109.22, -196) * mm, "radius": 0.87 * mm});
            skCircle(sketch, "E1.43.15.0", {"center": v(109.22, -210) * mm, "radius": 0.87 * mm});
            skCircle(sketch, "E1.43.16.0", {"center": v(109.22, -224) * mm, "radius": 0.87 * mm});
            skCircle(sketch, "E1.43.17.0", {"center": v(109.22, -238) * mm, "radius": 0.87 * mm});
            skCircle(sketch, "E1.43.18.0", {"center": v(109.22, -252) * mm, "radius": 0.87 * mm});
            skCircle(sketch, "E1.44.0.0", {"center": v(111.76, 0) * mm, "radius": 0.87 * mm});
            skCircle(sketch, "E1.44.1.0", {"center": v(111.76, -14) * mm, "radius": 0.87 * mm});
            skCircle(sketch, "E1.44.2.0", {"center": v(111.76, -28) * mm, "radius": 0.87 * mm});
            skCircle(sketch, "E1.44.3.0", {"center": v(111.76, -42) * mm, "radius": 0.87 * mm});
            skCircle(sketch, "E1.44.4.0", {"center": v(111.76, -56) * mm, "radius": 0.87 * mm});
            skCircle(sketch, "E1.44.5.0", {"center": v(111.76, -70) * mm, "radius": 0.87 * mm});
            skCircle(sketch, "E1.44.6.0", {"center": v(111.76, -84) * mm, "radius": 0.87 * mm});
            skCircle(sketch, "E1.44.7.0", {"center": v(111.76, -98) * mm, "radius": 0.87 * mm});
            skCircle(sketch, "E1.44.8.0", {"center": v(111.76, -112) * mm, "radius": 0.87 * mm});
            skCircle(sketch, "E1.44.9.0", {"center": v(111.76, -126) * mm, "radius": 0.87 * mm});
            skCircle(sketch, "E1.44.10.0", {"center": v(111.76, -140) * mm, "radius": 0.87 * mm});
            skCircle(sketch, "E1.44.11.0", {"center": v(111.76, -154) * mm, "radius": 0.87 * mm});
            skCircle(sketch, "E1.44.12.0", {"center": v(111.76, -168) * mm, "radius": 0.87 * mm});
            skCircle(sketch, "E1.44.13.0", {"center": v(111.76, -182) * mm, "radius": 0.87 * mm});
            skCircle(sketch, "E1.44.14.0", {"center": v(111.76, -196) * mm, "radius": 0.87 * mm});
            skCircle(sketch, "E1.44.15.0", {"center": v(111.76, -210) * mm, "radius": 0.87 * mm});
            skCircle(sketch, "E1.44.16.0", {"center": v(111.76, -224) * mm, "radius": 0.87 * mm});
            skCircle(sketch, "E1.44.17.0", {"center": v(111.76, -238) * mm, "radius": 0.87 * mm});
            skCircle(sketch, "E1.44.18.0", {"center": v(111.76, -252) * mm, "radius": 0.87 * mm});
            skCircle(sketch, "E1.45.0.0", {"center": v(114.3, 0) * mm, "radius": 0.87 * mm});
            skCircle(sketch, "E1.45.1.0", {"center": v(114.3, -14) * mm, "radius": 0.87 * mm});
            skCircle(sketch, "E1.45.2.0", {"center": v(114.3, -28) * mm, "radius": 0.87 * mm});
            skCircle(sketch, "E1.45.3.0", {"center": v(114.3, -42) * mm, "radius": 0.87 * mm});
            skCircle(sketch, "E1.45.4.0", {"center": v(114.3, -56) * mm, "radius": 0.87 * mm});
            skCircle(sketch, "E1.45.5.0", {"center": v(114.3, -70) * mm, "radius": 0.87 * mm});
            skCircle(sketch, "E1.45.6.0", {"center": v(114.3, -84) * mm, "radius": 0.87 * mm});
            skCircle(sketch, "E1.45.7.0", {"center": v(114.3, -98) * mm, "radius": 0.87 * mm});
            skCircle(sketch, "E1.45.8.0", {"center": v(114.3, -112) * mm, "radius": 0.87 * mm});
            skCircle(sketch, "E1.45.9.0", {"center": v(114.3, -126) * mm, "radius": 0.87 * mm});
            skCircle(sketch, "E1.45.10.0", {"center": v(114.3, -140) * mm, "radius": 0.87 * mm});
            skCircle(sketch, "E1.45.11.0", {"center": v(114.3, -154) * mm, "radius": 0.87 * mm});
            skCircle(sketch, "E1.45.12.0", {"center": v(114.3, -168) * mm, "radius": 0.87 * mm});
            skCircle(sketch, "E1.45.13.0", {"center": v(114.3, -182) * mm, "radius": 0.87 * mm});
            skCircle(sketch, "E1.45.14.0", {"center": v(114.3, -196) * mm, "radius": 0.87 * mm});
            skCircle(sketch, "E1.45.15.0", {"center": v(114.3, -210) * mm, "radius": 0.87 * mm});
            skCircle(sketch, "E1.45.16.0", {"center": v(114.3, -224) * mm, "radius": 0.87 * mm});
            skCircle(sketch, "E1.45.17.0", {"center": v(114.3, -238) * mm, "radius": 0.87 * mm});
            skCircle(sketch, "E1.45.18.0", {"center": v(114.3, -252) * mm, "radius": 0.87 * mm});
            skCircle(sketch, "E1.46.0.0", {"center": v(116.84, 0) * mm, "radius": 0.87 * mm});
            skCircle(sketch, "E1.46.1.0", {"center": v(116.84, -14) * mm, "radius": 0.87 * mm});
            skCircle(sketch, "E1.46.2.0", {"center": v(116.84, -28) * mm, "radius": 0.87 * mm});
            skCircle(sketch, "E1.46.3.0", {"center": v(116.84, -42) * mm, "radius": 0.87 * mm});
            skCircle(sketch, "E1.46.4.0", {"center": v(116.84, -56) * mm, "radius": 0.87 * mm});
            skCircle(sketch, "E1.46.5.0", {"center": v(116.84, -70) * mm, "radius": 0.87 * mm});
            skCircle(sketch, "E1.46.6.0", {"center": v(116.84, -84) * mm, "radius": 0.87 * mm});
            skCircle(sketch, "E1.46.7.0", {"center": v(116.84, -98) * mm, "radius": 0.87 * mm});
            skCircle(sketch, "E1.46.8.0", {"center": v(116.84, -112) * mm, "radius": 0.87 * mm});
            skCircle(sketch, "E1.46.9.0", {"center": v(116.84, -126) * mm, "radius": 0.87 * mm});
            skCircle(sketch, "E1.46.10.0", {"center": v(116.84, -140) * mm, "radius": 0.87 * mm});
            skCircle(sketch, "E1.46.11.0", {"center": v(116.84, -154) * mm, "radius": 0.87 * mm});
            skCircle(sketch, "E1.46.12.0", {"center": v(116.84, -168) * mm, "radius": 0.87 * mm});
            skCircle(sketch, "E1.46.13.0", {"center": v(116.84, -182) * mm, "radius": 0.87 * mm});
            skCircle(sketch, "E1.46.14.0", {"center": v(116.84, -196) * mm, "radius": 0.87 * mm});
            skCircle(sketch, "E1.46.15.0", {"center": v(116.84, -210) * mm, "radius": 0.87 * mm});
            skCircle(sketch, "E1.46.16.0", {"center": v(116.84, -224) * mm, "radius": 0.87 * mm});
            skCircle(sketch, "E1.46.17.0", {"center": v(116.84, -238) * mm, "radius": 0.87 * mm});
            skCircle(sketch, "E1.46.18.0", {"center": v(116.84, -252) * mm, "radius": 0.87 * mm});
            skCircle(sketch, "E1.47.0.0", {"center": v(119.38, 0) * mm, "radius": 0.87 * mm});
            skCircle(sketch, "E1.47.1.0", {"center": v(119.38, -14) * mm, "radius": 0.87 * mm});
            skCircle(sketch, "E1.47.2.0", {"center": v(119.38, -28) * mm, "radius": 0.87 * mm});
            skCircle(sketch, "E1.47.3.0", {"center": v(119.38, -42) * mm, "radius": 0.87 * mm});
            skCircle(sketch, "E1.47.4.0", {"center": v(119.38, -56) * mm, "radius": 0.87 * mm});
            skCircle(sketch, "E1.47.5.0", {"center": v(119.38, -70) * mm, "radius": 0.87 * mm});
            skCircle(sketch, "E1.47.6.0", {"center": v(119.38, -84) * mm, "radius": 0.87 * mm});
            skCircle(sketch, "E1.47.7.0", {"center": v(119.38, -98) * mm, "radius": 0.87 * mm});
            skCircle(sketch, "E1.47.8.0", {"center": v(119.38, -112) * mm, "radius": 0.87 * mm});
            skCircle(sketch, "E1.47.9.0", {"center": v(119.38, -126) * mm, "radius": 0.87 * mm});
            skCircle(sketch, "E1.47.10.0", {"center": v(119.38, -140) * mm, "radius": 0.87 * mm});
            skCircle(sketch, "E1.47.11.0", {"center": v(119.38, -154) * mm, "radius": 0.87 * mm});
            skCircle(sketch, "E1.47.12.0", {"center": v(119.38, -168) * mm, "radius": 0.87 * mm});
            skCircle(sketch, "E1.47.13.0", {"center": v(119.38, -182) * mm, "radius": 0.87 * mm});
            skCircle(sketch, "E1.47.14.0", {"center": v(119.38, -196) * mm, "radius": 0.87 * mm});
            skCircle(sketch, "E1.47.15.0", {"center": v(119.38, -210) * mm, "radius": 0.87 * mm});
            skCircle(sketch, "E1.47.16.0", {"center": v(119.38, -224) * mm, "radius": 0.87 * mm});
            skCircle(sketch, "E1.47.17.0", {"center": v(119.38, -238) * mm, "radius": 0.87 * mm});
            skCircle(sketch, "E1.47.18.0", {"center": v(119.38, -252) * mm, "radius": 0.87 * mm});
            skCircle(sketch, "E1.48.0.0", {"center": v(121.92, 0) * mm, "radius": 0.87 * mm});
            skCircle(sketch, "E1.48.1.0", {"center": v(121.92, -14) * mm, "radius": 0.87 * mm});
            skCircle(sketch, "E1.48.2.0", {"center": v(121.92, -28) * mm, "radius": 0.87 * mm});
            skCircle(sketch, "E1.48.3.0", {"center": v(121.92, -42) * mm, "radius": 0.87 * mm});
            skCircle(sketch, "E1.48.4.0", {"center": v(121.92, -56) * mm, "radius": 0.87 * mm});
            skCircle(sketch, "E1.48.5.0", {"center": v(121.92, -70) * mm, "radius": 0.87 * mm});
            skCircle(sketch, "E1.48.6.0", {"center": v(121.92, -84) * mm, "radius": 0.87 * mm});
            skCircle(sketch, "E1.48.7.0", {"center": v(121.92, -98) * mm, "radius": 0.87 * mm});
            skCircle(sketch, "E1.48.8.0", {"center": v(121.92, -112) * mm, "radius": 0.87 * mm});
            skCircle(sketch, "E1.48.9.0", {"center": v(121.92, -126) * mm, "radius": 0.87 * mm});
            skCircle(sketch, "E1.48.10.0", {"center": v(121.92, -140) * mm, "radius": 0.87 * mm});
            skCircle(sketch, "E1.48.11.0", {"center": v(121.92, -154) * mm, "radius": 0.87 * mm});
            skCircle(sketch, "E1.48.12.0", {"center": v(121.92, -168) * mm, "radius": 0.87 * mm});
            skCircle(sketch, "E1.48.13.0", {"center": v(121.92, -182) * mm, "radius": 0.87 * mm});
            skCircle(sketch, "E1.48.14.0", {"center": v(121.92, -196) * mm, "radius": 0.87 * mm});
            skCircle(sketch, "E1.48.15.0", {"center": v(121.92, -210) * mm, "radius": 0.87 * mm});
            skCircle(sketch, "E1.48.16.0", {"center": v(121.92, -224) * mm, "radius": 0.87 * mm});
            skCircle(sketch, "E1.48.17.0", {"center": v(121.92, -238) * mm, "radius": 0.87 * mm});
            skCircle(sketch, "E1.48.18.0", {"center": v(121.92, -252) * mm, "radius": 0.87 * mm});
            skCircle(sketch, "E1.49.0.0", {"center": v(124.46, 0) * mm, "radius": 0.87 * mm});
            skCircle(sketch, "E1.49.1.0", {"center": v(124.46, -14) * mm, "radius": 0.87 * mm});
            skCircle(sketch, "E1.49.2.0", {"center": v(124.46, -28) * mm, "radius": 0.87 * mm});
            skCircle(sketch, "E1.49.3.0", {"center": v(124.46, -42) * mm, "radius": 0.87 * mm});
            skCircle(sketch, "E1.49.4.0", {"center": v(124.46, -56) * mm, "radius": 0.87 * mm});
            skCircle(sketch, "E1.49.5.0", {"center": v(124.46, -70) * mm, "radius": 0.87 * mm});
            skCircle(sketch, "E1.49.6.0", {"center": v(124.46, -84) * mm, "radius": 0.87 * mm});
            skCircle(sketch, "E1.49.7.0", {"center": v(124.46, -98) * mm, "radius": 0.87 * mm});
            skCircle(sketch, "E1.49.8.0", {"center": v(124.46, -112) * mm, "radius": 0.87 * mm});
            skCircle(sketch, "E1.49.9.0", {"center": v(124.46, -126) * mm, "radius": 0.87 * mm});
            skCircle(sketch, "E1.49.10.0", {"center": v(124.46, -140) * mm, "radius": 0.87 * mm});
            skCircle(sketch, "E1.49.11.0", {"center": v(124.46, -154) * mm, "radius": 0.87 * mm});
            skCircle(sketch, "E1.49.12.0", {"center": v(124.46, -168) * mm, "radius": 0.87 * mm});
            skCircle(sketch, "E1.49.13.0", {"center": v(124.46, -182) * mm, "radius": 0.87 * mm});
            skCircle(sketch, "E1.49.14.0", {"center": v(124.46, -196) * mm, "radius": 0.87 * mm});
            skCircle(sketch, "E1.49.15.0", {"center": v(124.46, -210) * mm, "radius": 0.87 * mm});
            skCircle(sketch, "E1.49.16.0", {"center": v(124.46, -224) * mm, "radius": 0.87 * mm});
            skCircle(sketch, "E1.49.17.0", {"center": v(124.46, -238) * mm, "radius": 0.87 * mm});
            skCircle(sketch, "E1.49.18.0", {"center": v(124.46, -252) * mm, "radius": 0.87 * mm});
            skCircle(sketch, "E1.50.0.0", {"center": v(127, 0) * mm, "radius": 0.87 * mm});
            skCircle(sketch, "E1.50.1.0", {"center": v(127, -14) * mm, "radius": 0.87 * mm});
            skCircle(sketch, "E1.50.2.0", {"center": v(127, -28) * mm, "radius": 0.87 * mm});
            skCircle(sketch, "E1.50.3.0", {"center": v(127, -42) * mm, "radius": 0.87 * mm});
            skCircle(sketch, "E1.50.4.0", {"center": v(127, -56) * mm, "radius": 0.87 * mm});
            skCircle(sketch, "E1.50.5.0", {"center": v(127, -70) * mm, "radius": 0.87 * mm});
            skCircle(sketch, "E1.50.6.0", {"center": v(127, -84) * mm, "radius": 0.87 * mm});
            skCircle(sketch, "E1.50.7.0", {"center": v(127, -98) * mm, "radius": 0.87 * mm});
            skCircle(sketch, "E1.50.8.0", {"center": v(127, -112) * mm, "radius": 0.87 * mm});
            skCircle(sketch, "E1.50.9.0", {"center": v(127, -126) * mm, "radius": 0.87 * mm});
            skCircle(sketch, "E1.50.10.0", {"center": v(127, -140) * mm, "radius": 0.87 * mm});
            skCircle(sketch, "E1.50.11.0", {"center": v(127, -154) * mm, "radius": 0.87 * mm});
            skCircle(sketch, "E1.50.12.0", {"center": v(127, -168) * mm, "radius": 0.87 * mm});
            skCircle(sketch, "E1.50.13.0", {"center": v(127, -182) * mm, "radius": 0.87 * mm});
            skCircle(sketch, "E1.50.14.0", {"center": v(127, -196) * mm, "radius": 0.87 * mm});
            skCircle(sketch, "E1.50.15.0", {"center": v(127, -210) * mm, "radius": 0.87 * mm});
            skCircle(sketch, "E1.50.16.0", {"center": v(127, -224) * mm, "radius": 0.87 * mm});
            skCircle(sketch, "E1.50.17.0", {"center": v(127, -238) * mm, "radius": 0.87 * mm});
            skCircle(sketch, "E1.50.18.0", {"center": v(127, -252) * mm, "radius": 0.87 * mm});
            skCircle(sketch, "E1.51.0.0", {"center": v(129.54, 0) * mm, "radius": 0.87 * mm});
            skCircle(sketch, "E1.51.1.0", {"center": v(129.54, -14) * mm, "radius": 0.87 * mm});
            skCircle(sketch, "E1.51.2.0", {"center": v(129.54, -28) * mm, "radius": 0.87 * mm});
            skCircle(sketch, "E1.51.3.0", {"center": v(129.54, -42) * mm, "radius": 0.87 * mm});
            skCircle(sketch, "E1.51.4.0", {"center": v(129.54, -56) * mm, "radius": 0.87 * mm});
            skCircle(sketch, "E1.51.5.0", {"center": v(129.54, -70) * mm, "radius": 0.87 * mm});
            skCircle(sketch, "E1.51.6.0", {"center": v(129.54, -84) * mm, "radius": 0.87 * mm});
            skCircle(sketch, "E1.51.7.0", {"center": v(129.54, -98) * mm, "radius": 0.87 * mm});
            skCircle(sketch, "E1.51.8.0", {"center": v(129.54, -112) * mm, "radius": 0.87 * mm});
            skCircle(sketch, "E1.51.9.0", {"center": v(129.54, -126) * mm, "radius": 0.87 * mm});
            skCircle(sketch, "E1.51.10.0", {"center": v(129.54, -140) * mm, "radius": 0.87 * mm});
            skCircle(sketch, "E1.51.11.0", {"center": v(129.54, -154) * mm, "radius": 0.87 * mm});
            skCircle(sketch, "E1.51.12.0", {"center": v(129.54, -168) * mm, "radius": 0.87 * mm});
            skCircle(sketch, "E1.51.13.0", {"center": v(129.54, -182) * mm, "radius": 0.87 * mm});
            skCircle(sketch, "E1.51.14.0", {"center": v(129.54, -196) * mm, "radius": 0.87 * mm});
            skCircle(sketch, "E1.51.15.0", {"center": v(129.54, -210) * mm, "radius": 0.87 * mm});
            skCircle(sketch, "E1.51.16.0", {"center": v(129.54, -224) * mm, "radius": 0.87 * mm});
            skCircle(sketch, "E1.51.17.0", {"center": v(129.54, -238) * mm, "radius": 0.87 * mm});
            skCircle(sketch, "E1.51.18.0", {"center": v(129.54, -252) * mm, "radius": 0.87 * mm});
            skCircle(sketch, "E1.52.0.0", {"center": v(132.08, 0) * mm, "radius": 0.87 * mm});
            skCircle(sketch, "E1.52.1.0", {"center": v(132.08, -14) * mm, "radius": 0.87 * mm});
            skCircle(sketch, "E1.52.2.0", {"center": v(132.08, -28) * mm, "radius": 0.87 * mm});
            skCircle(sketch, "E1.52.3.0", {"center": v(132.08, -42) * mm, "radius": 0.87 * mm});
            skCircle(sketch, "E1.52.4.0", {"center": v(132.08, -56) * mm, "radius": 0.87 * mm});
            skCircle(sketch, "E1.52.5.0", {"center": v(132.08, -70) * mm, "radius": 0.87 * mm});
            skCircle(sketch, "E1.52.6.0", {"center": v(132.08, -84) * mm, "radius": 0.87 * mm});
            skCircle(sketch, "E1.52.7.0", {"center": v(132.08, -98) * mm, "radius": 0.87 * mm});
            skCircle(sketch, "E1.52.8.0", {"center": v(132.08, -112) * mm, "radius": 0.87 * mm});
            skCircle(sketch, "E1.52.9.0", {"center": v(132.08, -126) * mm, "radius": 0.87 * mm});
            skCircle(sketch, "E1.52.10.0", {"center": v(132.08, -140) * mm, "radius": 0.87 * mm});
            skCircle(sketch, "E1.52.11.0", {"center": v(132.08, -154) * mm, "radius": 0.87 * mm});
            skCircle(sketch, "E1.52.12.0", {"center": v(132.08, -168) * mm, "radius": 0.87 * mm});
            skCircle(sketch, "E1.52.13.0", {"center": v(132.08, -182) * mm, "radius": 0.87 * mm});
            skCircle(sketch, "E1.52.14.0", {"center": v(132.08, -196) * mm, "radius": 0.87 * mm});
            skCircle(sketch, "E1.52.15.0", {"center": v(132.08, -210) * mm, "radius": 0.87 * mm});
            skCircle(sketch, "E1.52.16.0", {"center": v(132.08, -224) * mm, "radius": 0.87 * mm});
            skCircle(sketch, "E1.52.17.0", {"center": v(132.08, -238) * mm, "radius": 0.87 * mm});
            skCircle(sketch, "E1.52.18.0", {"center": v(132.08, -252) * mm, "radius": 0.87 * mm});
            skCircle(sketch, "E1.53.0.0", {"center": v(134.62, 0) * mm, "radius": 0.87 * mm});
            skCircle(sketch, "E1.53.1.0", {"center": v(134.62, -14) * mm, "radius": 0.87 * mm});
            skCircle(sketch, "E1.53.2.0", {"center": v(134.62, -28) * mm, "radius": 0.87 * mm});
            skCircle(sketch, "E1.53.3.0", {"center": v(134.62, -42) * mm, "radius": 0.87 * mm});
            skCircle(sketch, "E1.53.4.0", {"center": v(134.62, -56) * mm, "radius": 0.87 * mm});
            skCircle(sketch, "E1.53.5.0", {"center": v(134.62, -70) * mm, "radius": 0.87 * mm});
            skCircle(sketch, "E1.53.6.0", {"center": v(134.62, -84) * mm, "radius": 0.87 * mm});
            skCircle(sketch, "E1.53.7.0", {"center": v(134.62, -98) * mm, "radius": 0.87 * mm});
            skCircle(sketch, "E1.53.8.0", {"center": v(134.62, -112) * mm, "radius": 0.87 * mm});
            skCircle(sketch, "E1.53.9.0", {"center": v(134.62, -126) * mm, "radius": 0.87 * mm});
            skCircle(sketch, "E1.53.10.0", {"center": v(134.62, -140) * mm, "radius": 0.87 * mm});
            skCircle(sketch, "E1.53.11.0", {"center": v(134.62, -154) * mm, "radius": 0.87 * mm});
            skCircle(sketch, "E1.53.12.0", {"center": v(134.62, -168) * mm, "radius": 0.87 * mm});
            skCircle(sketch, "E1.53.13.0", {"center": v(134.62, -182) * mm, "radius": 0.87 * mm});
            skCircle(sketch, "E1.53.14.0", {"center": v(134.62, -196) * mm, "radius": 0.87 * mm});
            skCircle(sketch, "E1.53.15.0", {"center": v(134.62, -210) * mm, "radius": 0.87 * mm});
            skCircle(sketch, "E1.53.16.0", {"center": v(134.62, -224) * mm, "radius": 0.87 * mm});
            skCircle(sketch, "E1.53.17.0", {"center": v(134.62, -238) * mm, "radius": 0.87 * mm});
            skCircle(sketch, "E1.53.18.0", {"center": v(134.62, -252) * mm, "radius": 0.87 * mm});
            skCircle(sketch, "E1.54.0.0", {"center": v(137.16, 0) * mm, "radius": 0.87 * mm});
            skCircle(sketch, "E1.54.1.0", {"center": v(137.16, -14) * mm, "radius": 0.87 * mm});
            skCircle(sketch, "E1.54.2.0", {"center": v(137.16, -28) * mm, "radius": 0.87 * mm});
            skCircle(sketch, "E1.54.3.0", {"center": v(137.16, -42) * mm, "radius": 0.87 * mm});
            skCircle(sketch, "E1.54.4.0", {"center": v(137.16, -56) * mm, "radius": 0.87 * mm});
            skCircle(sketch, "E1.54.5.0", {"center": v(137.16, -70) * mm, "radius": 0.87 * mm});
            skCircle(sketch, "E1.54.6.0", {"center": v(137.16, -84) * mm, "radius": 0.87 * mm});
            skCircle(sketch, "E1.54.7.0", {"center": v(137.16, -98) * mm, "radius": 0.87 * mm});
            skCircle(sketch, "E1.54.8.0", {"center": v(137.16, -112) * mm, "radius": 0.87 * mm});
            skCircle(sketch, "E1.54.9.0", {"center": v(137.16, -126) * mm, "radius": 0.87 * mm});
            skCircle(sketch, "E1.54.10.0", {"center": v(137.16, -140) * mm, "radius": 0.87 * mm});
            skCircle(sketch, "E1.54.11.0", {"center": v(137.16, -154) * mm, "radius": 0.87 * mm});
            skCircle(sketch, "E1.54.12.0", {"center": v(137.16, -168) * mm, "radius": 0.87 * mm});
            skCircle(sketch, "E1.54.13.0", {"center": v(137.16, -182) * mm, "radius": 0.87 * mm});
            skCircle(sketch, "E1.54.14.0", {"center": v(137.16, -196) * mm, "radius": 0.87 * mm});
            skCircle(sketch, "E1.54.15.0", {"center": v(137.16, -210) * mm, "radius": 0.87 * mm});
            skCircle(sketch, "E1.54.16.0", {"center": v(137.16, -224) * mm, "radius": 0.87 * mm});
            skCircle(sketch, "E1.54.17.0", {"center": v(137.16, -238) * mm, "radius": 0.87 * mm});
            skCircle(sketch, "E1.54.18.0", {"center": v(137.16, -252) * mm, "radius": 0.87 * mm});
            skCircle(sketch, "E1.55.0.0", {"center": v(139.7, 0) * mm, "radius": 0.87 * mm});
            skCircle(sketch, "E1.55.1.0", {"center": v(139.7, -14) * mm, "radius": 0.87 * mm});
            skCircle(sketch, "E1.55.2.0", {"center": v(139.7, -28) * mm, "radius": 0.87 * mm});
            skCircle(sketch, "E1.55.3.0", {"center": v(139.7, -42) * mm, "radius": 0.87 * mm});
            skCircle(sketch, "E1.55.4.0", {"center": v(139.7, -56) * mm, "radius": 0.87 * mm});
            skCircle(sketch, "E1.55.5.0", {"center": v(139.7, -70) * mm, "radius": 0.87 * mm});
            skCircle(sketch, "E1.55.6.0", {"center": v(139.7, -84) * mm, "radius": 0.87 * mm});
            skCircle(sketch, "E1.55.7.0", {"center": v(139.7, -98) * mm, "radius": 0.87 * mm});
            skCircle(sketch, "E1.55.8.0", {"center": v(139.7, -112) * mm, "radius": 0.87 * mm});
            skCircle(sketch, "E1.55.9.0", {"center": v(139.7, -126) * mm, "radius": 0.87 * mm});
            skCircle(sketch, "E1.55.10.0", {"center": v(139.7, -140) * mm, "radius": 0.87 * mm});
            skCircle(sketch, "E1.55.11.0", {"center": v(139.7, -154) * mm, "radius": 0.87 * mm});
            skCircle(sketch, "E1.55.12.0", {"center": v(139.7, -168) * mm, "radius": 0.87 * mm});
            skCircle(sketch, "E1.55.13.0", {"center": v(139.7, -182) * mm, "radius": 0.87 * mm});
            skCircle(sketch, "E1.55.14.0", {"center": v(139.7, -196) * mm, "radius": 0.87 * mm});
            skCircle(sketch, "E1.55.15.0", {"center": v(139.7, -210) * mm, "radius": 0.87 * mm});
            skCircle(sketch, "E1.55.16.0", {"center": v(139.7, -224) * mm, "radius": 0.87 * mm});
            skCircle(sketch, "E1.55.17.0", {"center": v(139.7, -238) * mm, "radius": 0.87 * mm});
            skCircle(sketch, "E1.55.18.0", {"center": v(139.7, -252) * mm, "radius": 0.87 * mm});
            skCircle(sketch, "E1.56.0.0", {"center": v(142.24, 0) * mm, "radius": 0.87 * mm});
            skCircle(sketch, "E1.56.1.0", {"center": v(142.24, -14) * mm, "radius": 0.87 * mm});
            skCircle(sketch, "E1.56.2.0", {"center": v(142.24, -28) * mm, "radius": 0.87 * mm});
            skCircle(sketch, "E1.56.3.0", {"center": v(142.24, -42) * mm, "radius": 0.87 * mm});
            skCircle(sketch, "E1.56.4.0", {"center": v(142.24, -56) * mm, "radius": 0.87 * mm});
            skCircle(sketch, "E1.56.5.0", {"center": v(142.24, -70) * mm, "radius": 0.87 * mm});
            skCircle(sketch, "E1.56.6.0", {"center": v(142.24, -84) * mm, "radius": 0.87 * mm});
            skCircle(sketch, "E1.56.7.0", {"center": v(142.24, -98) * mm, "radius": 0.87 * mm});
            skCircle(sketch, "E1.56.8.0", {"center": v(142.24, -112) * mm, "radius": 0.87 * mm});
            skCircle(sketch, "E1.56.9.0", {"center": v(142.24, -126) * mm, "radius": 0.87 * mm});
            skCircle(sketch, "E1.56.10.0", {"center": v(142.24, -140) * mm, "radius": 0.87 * mm});
            skCircle(sketch, "E1.56.11.0", {"center": v(142.24, -154) * mm, "radius": 0.87 * mm});
            skCircle(sketch, "E1.56.12.0", {"center": v(142.24, -168) * mm, "radius": 0.87 * mm});
            skCircle(sketch, "E1.56.13.0", {"center": v(142.24, -182) * mm, "radius": 0.87 * mm});
            skCircle(sketch, "E1.56.14.0", {"center": v(142.24, -196) * mm, "radius": 0.87 * mm});
            skCircle(sketch, "E1.56.15.0", {"center": v(142.24, -210) * mm, "radius": 0.87 * mm});
            skCircle(sketch, "E1.56.16.0", {"center": v(142.24, -224) * mm, "radius": 0.87 * mm});
            skCircle(sketch, "E1.56.17.0", {"center": v(142.24, -238) * mm, "radius": 0.87 * mm});
            skCircle(sketch, "E1.56.18.0", {"center": v(142.24, -252) * mm, "radius": 0.87 * mm});
            skCircle(sketch, "E1.57.0.0", {"center": v(144.78, 0) * mm, "radius": 0.87 * mm});
            skCircle(sketch, "E1.57.1.0", {"center": v(144.78, -14) * mm, "radius": 0.87 * mm});
            skCircle(sketch, "E1.57.2.0", {"center": v(144.78, -28) * mm, "radius": 0.87 * mm});
            skCircle(sketch, "E1.57.3.0", {"center": v(144.78, -42) * mm, "radius": 0.87 * mm});
            skCircle(sketch, "E1.57.4.0", {"center": v(144.78, -56) * mm, "radius": 0.87 * mm});
            skCircle(sketch, "E1.57.5.0", {"center": v(144.78, -70) * mm, "radius": 0.87 * mm});
            skCircle(sketch, "E1.57.6.0", {"center": v(144.78, -84) * mm, "radius": 0.87 * mm});
            skCircle(sketch, "E1.57.7.0", {"center": v(144.78, -98) * mm, "radius": 0.87 * mm});
            skCircle(sketch, "E1.57.8.0", {"center": v(144.78, -112) * mm, "radius": 0.87 * mm});
            skCircle(sketch, "E1.57.9.0", {"center": v(144.78, -126) * mm, "radius": 0.87 * mm});
            skCircle(sketch, "E1.57.10.0", {"center": v(144.78, -140) * mm, "radius": 0.87 * mm});
            skCircle(sketch, "E1.57.11.0", {"center": v(144.78, -154) * mm, "radius": 0.87 * mm});
            skCircle(sketch, "E1.57.12.0", {"center": v(144.78, -168) * mm, "radius": 0.87 * mm});
            skCircle(sketch, "E1.57.13.0", {"center": v(144.78, -182) * mm, "radius": 0.87 * mm});
            skCircle(sketch, "E1.57.14.0", {"center": v(144.78, -196) * mm, "radius": 0.87 * mm});
            skCircle(sketch, "E1.57.15.0", {"center": v(144.78, -210) * mm, "radius": 0.87 * mm});
            skCircle(sketch, "E1.57.16.0", {"center": v(144.78, -224) * mm, "radius": 0.87 * mm});
            skCircle(sketch, "E1.57.17.0", {"center": v(144.78, -238) * mm, "radius": 0.87 * mm});
            skCircle(sketch, "E1.57.18.0", {"center": v(144.78, -252) * mm, "radius": 0.87 * mm});
            skCircle(sketch, "E1.58.0.0", {"center": v(147.32, 0) * mm, "radius": 0.87 * mm});
            skCircle(sketch, "E1.58.1.0", {"center": v(147.32, -14) * mm, "radius": 0.87 * mm});
            skCircle(sketch, "E1.58.2.0", {"center": v(147.32, -28) * mm, "radius": 0.87 * mm});
            skCircle(sketch, "E1.58.3.0", {"center": v(147.32, -42) * mm, "radius": 0.87 * mm});
            skCircle(sketch, "E1.58.4.0", {"center": v(147.32, -56) * mm, "radius": 0.87 * mm});
            skCircle(sketch, "E1.58.5.0", {"center": v(147.32, -70) * mm, "radius": 0.87 * mm});
            skCircle(sketch, "E1.58.6.0", {"center": v(147.32, -84) * mm, "radius": 0.87 * mm});
            skCircle(sketch, "E1.58.7.0", {"center": v(147.32, -98) * mm, "radius": 0.87 * mm});
            skCircle(sketch, "E1.58.8.0", {"center": v(147.32, -112) * mm, "radius": 0.87 * mm});
            skCircle(sketch, "E1.58.9.0", {"center": v(147.32, -126) * mm, "radius": 0.87 * mm});
            skCircle(sketch, "E1.58.10.0", {"center": v(147.32, -140) * mm, "radius": 0.87 * mm});
            skCircle(sketch, "E1.58.11.0", {"center": v(147.32, -154) * mm, "radius": 0.87 * mm});
            skCircle(sketch, "E1.58.12.0", {"center": v(147.32, -168) * mm, "radius": 0.87 * mm});
            skCircle(sketch, "E1.58.13.0", {"center": v(147.32, -182) * mm, "radius": 0.87 * mm});
            skCircle(sketch, "E1.58.14.0", {"center": v(147.32, -196) * mm, "radius": 0.87 * mm});
            skCircle(sketch, "E1.58.15.0", {"center": v(147.32, -210) * mm, "radius": 0.87 * mm});
            skCircle(sketch, "E1.58.16.0", {"center": v(147.32, -224) * mm, "radius": 0.87 * mm});
            skCircle(sketch, "E1.58.17.0", {"center": v(147.32, -238) * mm, "radius": 0.87 * mm});
            skCircle(sketch, "E1.58.18.0", {"center": v(147.32, -252) * mm, "radius": 0.87 * mm});
            skCircle(sketch, "E1.59.0.0", {"center": v(149.86, 0) * mm, "radius": 0.87 * mm});
            skCircle(sketch, "E1.59.1.0", {"center": v(149.86, -14) * mm, "radius": 0.87 * mm});
            skCircle(sketch, "E1.59.2.0", {"center": v(149.86, -28) * mm, "radius": 0.87 * mm});
            skCircle(sketch, "E1.59.3.0", {"center": v(149.86, -42) * mm, "radius": 0.87 * mm});
            skCircle(sketch, "E1.59.4.0", {"center": v(149.86, -56) * mm, "radius": 0.87 * mm});
            skCircle(sketch, "E1.59.5.0", {"center": v(149.86, -70) * mm, "radius": 0.87 * mm});
            skCircle(sketch, "E1.59.6.0", {"center": v(149.86, -84) * mm, "radius": 0.87 * mm});
            skCircle(sketch, "E1.59.7.0", {"center": v(149.86, -98) * mm, "radius": 0.87 * mm});
            skCircle(sketch, "E1.59.8.0", {"center": v(149.86, -112) * mm, "radius": 0.87 * mm});
            skCircle(sketch, "E1.59.9.0", {"center": v(149.86, -126) * mm, "radius": 0.87 * mm});
            skCircle(sketch, "E1.59.10.0", {"center": v(149.86, -140) * mm, "radius": 0.87 * mm});
            skCircle(sketch, "E1.59.11.0", {"center": v(149.86, -154) * mm, "radius": 0.87 * mm});
            skCircle(sketch, "E1.59.12.0", {"center": v(149.86, -168) * mm, "radius": 0.87 * mm});
            skCircle(sketch, "E1.59.13.0", {"center": v(149.86, -182) * mm, "radius": 0.87 * mm});
            skCircle(sketch, "E1.59.14.0", {"center": v(149.86, -196) * mm, "radius": 0.87 * mm});
            skCircle(sketch, "E1.59.15.0", {"center": v(149.86, -210) * mm, "radius": 0.87 * mm});
            skCircle(sketch, "E1.59.16.0", {"center": v(149.86, -224) * mm, "radius": 0.87 * mm});
            skCircle(sketch, "E1.59.17.0", {"center": v(149.86, -238) * mm, "radius": 0.87 * mm});
            skCircle(sketch, "E1.59.18.0", {"center": v(149.86, -252) * mm, "radius": 0.87 * mm});
            skCircle(sketch, "E1.60.0.0", {"center": v(152.4, 0) * mm, "radius": 0.87 * mm});
            skCircle(sketch, "E1.60.1.0", {"center": v(152.4, -14) * mm, "radius": 0.87 * mm});
            skCircle(sketch, "E1.60.2.0", {"center": v(152.4, -28) * mm, "radius": 0.87 * mm});
            skCircle(sketch, "E1.60.3.0", {"center": v(152.4, -42) * mm, "radius": 0.87 * mm});
            skCircle(sketch, "E1.60.4.0", {"center": v(152.4, -56) * mm, "radius": 0.87 * mm});
            skCircle(sketch, "E1.60.5.0", {"center": v(152.4, -70) * mm, "radius": 0.87 * mm});
            skCircle(sketch, "E1.60.6.0", {"center": v(152.4, -84) * mm, "radius": 0.87 * mm});
            skCircle(sketch, "E1.60.7.0", {"center": v(152.4, -98) * mm, "radius": 0.87 * mm});
            skCircle(sketch, "E1.60.8.0", {"center": v(152.4, -112) * mm, "radius": 0.87 * mm});
            skCircle(sketch, "E1.60.9.0", {"center": v(152.4, -126) * mm, "radius": 0.87 * mm});
            skCircle(sketch, "E1.60.10.0", {"center": v(152.4, -140) * mm, "radius": 0.87 * mm});
            skCircle(sketch, "E1.60.11.0", {"center": v(152.4, -154) * mm, "radius": 0.87 * mm});
            skCircle(sketch, "E1.60.12.0", {"center": v(152.4, -168) * mm, "radius": 0.87 * mm});
            skCircle(sketch, "E1.60.13.0", {"center": v(152.4, -182) * mm, "radius": 0.87 * mm});
            skCircle(sketch, "E1.60.14.0", {"center": v(152.4, -196) * mm, "radius": 0.87 * mm});
            skCircle(sketch, "E1.60.15.0", {"center": v(152.4, -210) * mm, "radius": 0.87 * mm});
            skCircle(sketch, "E1.60.16.0", {"center": v(152.4, -224) * mm, "radius": 0.87 * mm});
            skCircle(sketch, "E1.60.17.0", {"center": v(152.4, -238) * mm, "radius": 0.87 * mm});
            skCircle(sketch, "E1.60.18.0", {"center": v(152.4, -252) * mm, "radius": 0.87 * mm});
            skCircle(sketch, "E1.61.0.0", {"center": v(154.94, 0) * mm, "radius": 0.87 * mm});
            skCircle(sketch, "E1.61.1.0", {"center": v(154.94, -14) * mm, "radius": 0.87 * mm});
            skCircle(sketch, "E1.61.2.0", {"center": v(154.94, -28) * mm, "radius": 0.87 * mm});
            skCircle(sketch, "E1.61.3.0", {"center": v(154.94, -42) * mm, "radius": 0.87 * mm});
            skCircle(sketch, "E1.61.4.0", {"center": v(154.94, -56) * mm, "radius": 0.87 * mm});
            skCircle(sketch, "E1.61.5.0", {"center": v(154.94, -70) * mm, "radius": 0.87 * mm});
            skCircle(sketch, "E1.61.6.0", {"center": v(154.94, -84) * mm, "radius": 0.87 * mm});
            skCircle(sketch, "E1.61.7.0", {"center": v(154.94, -98) * mm, "radius": 0.87 * mm});
            skCircle(sketch, "E1.61.8.0", {"center": v(154.94, -112) * mm, "radius": 0.87 * mm});
            skCircle(sketch, "E1.61.9.0", {"center": v(154.94, -126) * mm, "radius": 0.87 * mm});
            skCircle(sketch, "E1.61.10.0", {"center": v(154.94, -140) * mm, "radius": 0.87 * mm});
            skCircle(sketch, "E1.61.11.0", {"center": v(154.94, -154) * mm, "radius": 0.87 * mm});
            skCircle(sketch, "E1.61.12.0", {"center": v(154.94, -168) * mm, "radius": 0.87 * mm});
            skCircle(sketch, "E1.61.13.0", {"center": v(154.94, -182) * mm, "radius": 0.87 * mm});
            skCircle(sketch, "E1.61.14.0", {"center": v(154.94, -196) * mm, "radius": 0.87 * mm});
            skCircle(sketch, "E1.61.15.0", {"center": v(154.94, -210) * mm, "radius": 0.87 * mm});
            skCircle(sketch, "E1.61.16.0", {"center": v(154.94, -224) * mm, "radius": 0.87 * mm});
            skCircle(sketch, "E1.61.17.0", {"center": v(154.94, -238) * mm, "radius": 0.87 * mm});
            skCircle(sketch, "E1.61.18.0", {"center": v(154.94, -252) * mm, "radius": 0.87 * mm});
            skCircle(sketch, "E1.62.0.0", {"center": v(157.48, 0) * mm, "radius": 0.87 * mm});
            skCircle(sketch, "E1.62.1.0", {"center": v(157.48, -14) * mm, "radius": 0.87 * mm});
            skCircle(sketch, "E1.62.2.0", {"center": v(157.48, -28) * mm, "radius": 0.87 * mm});
            skCircle(sketch, "E1.62.3.0", {"center": v(157.48, -42) * mm, "radius": 0.87 * mm});
            skCircle(sketch, "E1.62.4.0", {"center": v(157.48, -56) * mm, "radius": 0.87 * mm});
            skCircle(sketch, "E1.62.5.0", {"center": v(157.48, -70) * mm, "radius": 0.87 * mm});
            skCircle(sketch, "E1.62.6.0", {"center": v(157.48, -84) * mm, "radius": 0.87 * mm});
            skCircle(sketch, "E1.62.7.0", {"center": v(157.48, -98) * mm, "radius": 0.87 * mm});
            skCircle(sketch, "E1.62.8.0", {"center": v(157.48, -112) * mm, "radius": 0.87 * mm});
            skCircle(sketch, "E1.62.9.0", {"center": v(157.48, -126) * mm, "radius": 0.87 * mm});
            skCircle(sketch, "E1.62.10.0", {"center": v(157.48, -140) * mm, "radius": 0.87 * mm});
            skCircle(sketch, "E1.62.11.0", {"center": v(157.48, -154) * mm, "radius": 0.87 * mm});
            skCircle(sketch, "E1.62.12.0", {"center": v(157.48, -168) * mm, "radius": 0.87 * mm});
            skCircle(sketch, "E1.62.13.0", {"center": v(157.48, -182) * mm, "radius": 0.87 * mm});
            skCircle(sketch, "E1.62.14.0", {"center": v(157.48, -196) * mm, "radius": 0.87 * mm});
            skCircle(sketch, "E1.62.15.0", {"center": v(157.48, -210) * mm, "radius": 0.87 * mm});
            skCircle(sketch, "E1.62.16.0", {"center": v(157.48, -224) * mm, "radius": 0.87 * mm});
            skCircle(sketch, "E1.62.17.0", {"center": v(157.48, -238) * mm, "radius": 0.87 * mm});
            skCircle(sketch, "E1.62.18.0", {"center": v(157.48, -252) * mm, "radius": 0.87 * mm});
            skCircle(sketch, "E1.63.0.0", {"center": v(160.02, 0) * mm, "radius": 0.87 * mm});
            skCircle(sketch, "E1.63.1.0", {"center": v(160.02, -14) * mm, "radius": 0.87 * mm});
            skCircle(sketch, "E1.63.2.0", {"center": v(160.02, -28) * mm, "radius": 0.87 * mm});
            skCircle(sketch, "E1.63.3.0", {"center": v(160.02, -42) * mm, "radius": 0.87 * mm});
            skCircle(sketch, "E1.63.4.0", {"center": v(160.02, -56) * mm, "radius": 0.87 * mm});
            skCircle(sketch, "E1.63.5.0", {"center": v(160.02, -70) * mm, "radius": 0.87 * mm});
            skCircle(sketch, "E1.63.6.0", {"center": v(160.02, -84) * mm, "radius": 0.87 * mm});
            skCircle(sketch, "E1.63.7.0", {"center": v(160.02, -98) * mm, "radius": 0.87 * mm});
            skCircle(sketch, "E1.63.8.0", {"center": v(160.02, -112) * mm, "radius": 0.87 * mm});
            skCircle(sketch, "E1.63.9.0", {"center": v(160.02, -126) * mm, "radius": 0.87 * mm});
            skCircle(sketch, "E1.63.10.0", {"center": v(160.02, -140) * mm, "radius": 0.87 * mm});
            skCircle(sketch, "E1.63.11.0", {"center": v(160.02, -154) * mm, "radius": 0.87 * mm});
            skCircle(sketch, "E1.63.12.0", {"center": v(160.02, -168) * mm, "radius": 0.87 * mm});
            skCircle(sketch, "E1.63.13.0", {"center": v(160.02, -182) * mm, "radius": 0.87 * mm});
            skCircle(sketch, "E1.63.14.0", {"center": v(160.02, -196) * mm, "radius": 0.87 * mm});
            skCircle(sketch, "E1.63.15.0", {"center": v(160.02, -210) * mm, "radius": 0.87 * mm});
            skCircle(sketch, "E1.63.16.0", {"center": v(160.02, -224) * mm, "radius": 0.87 * mm});
            skCircle(sketch, "E1.63.17.0", {"center": v(160.02, -238) * mm, "radius": 0.87 * mm});
            skCircle(sketch, "E1.63.18.0", {"center": v(160.02, -252) * mm, "radius": 0.87 * mm});
            skCircle(sketch, "E1.64.0.0", {"center": v(162.56, 0) * mm, "radius": 0.87 * mm});
            skCircle(sketch, "E1.64.1.0", {"center": v(162.56, -14) * mm, "radius": 0.87 * mm});
            skCircle(sketch, "E1.64.2.0", {"center": v(162.56, -28) * mm, "radius": 0.87 * mm});
            skCircle(sketch, "E1.64.3.0", {"center": v(162.56, -42) * mm, "radius": 0.87 * mm});
            skCircle(sketch, "E1.64.4.0", {"center": v(162.56, -56) * mm, "radius": 0.87 * mm});
            skCircle(sketch, "E1.64.5.0", {"center": v(162.56, -70) * mm, "radius": 0.87 * mm});
            skCircle(sketch, "E1.64.6.0", {"center": v(162.56, -84) * mm, "radius": 0.87 * mm});
            skCircle(sketch, "E1.64.7.0", {"center": v(162.56, -98) * mm, "radius": 0.87 * mm});
            skCircle(sketch, "E1.64.8.0", {"center": v(162.56, -112) * mm, "radius": 0.87 * mm});
            skCircle(sketch, "E1.64.9.0", {"center": v(162.56, -126) * mm, "radius": 0.87 * mm});
            skCircle(sketch, "E1.64.10.0", {"center": v(162.56, -140) * mm, "radius": 0.87 * mm});
            skCircle(sketch, "E1.64.11.0", {"center": v(162.56, -154) * mm, "radius": 0.87 * mm});
            skCircle(sketch, "E1.64.12.0", {"center": v(162.56, -168) * mm, "radius": 0.87 * mm});
            skCircle(sketch, "E1.64.13.0", {"center": v(162.56, -182) * mm, "radius": 0.87 * mm});
            skCircle(sketch, "E1.64.14.0", {"center": v(162.56, -196) * mm, "radius": 0.87 * mm});
            skCircle(sketch, "E1.64.15.0", {"center": v(162.56, -210) * mm, "radius": 0.87 * mm});
            skCircle(sketch, "E1.64.16.0", {"center": v(162.56, -224) * mm, "radius": 0.87 * mm});
            skCircle(sketch, "E1.64.17.0", {"center": v(162.56, -238) * mm, "radius": 0.87 * mm});
            skCircle(sketch, "E1.64.18.0", {"center": v(162.56, -252) * mm, "radius": 0.87 * mm});
            skCircle(sketch, "E1.65.0.0", {"center": v(165.1, 0) * mm, "radius": 0.87 * mm});
            skCircle(sketch, "E1.65.1.0", {"center": v(165.1, -14) * mm, "radius": 0.87 * mm});
            skCircle(sketch, "E1.65.2.0", {"center": v(165.1, -28) * mm, "radius": 0.87 * mm});
            skCircle(sketch, "E1.65.3.0", {"center": v(165.1, -42) * mm, "radius": 0.87 * mm});
            skCircle(sketch, "E1.65.4.0", {"center": v(165.1, -56) * mm, "radius": 0.87 * mm});
            skCircle(sketch, "E1.65.5.0", {"center": v(165.1, -70) * mm, "radius": 0.87 * mm});
            skCircle(sketch, "E1.65.6.0", {"center": v(165.1, -84) * mm, "radius": 0.87 * mm});
            skCircle(sketch, "E1.65.7.0", {"center": v(165.1, -98) * mm, "radius": 0.87 * mm});
            skCircle(sketch, "E1.65.8.0", {"center": v(165.1, -112) * mm, "radius": 0.87 * mm});
            skCircle(sketch, "E1.65.9.0", {"center": v(165.1, -126) * mm, "radius": 0.87 * mm});
            skCircle(sketch, "E1.65.10.0", {"center": v(165.1, -140) * mm, "radius": 0.87 * mm});
            skCircle(sketch, "E1.65.11.0", {"center": v(165.1, -154) * mm, "radius": 0.87 * mm});
            skCircle(sketch, "E1.65.12.0", {"center": v(165.1, -168) * mm, "radius": 0.87 * mm});
            skCircle(sketch, "E1.65.13.0", {"center": v(165.1, -182) * mm, "radius": 0.87 * mm});
            skCircle(sketch, "E1.65.14.0", {"center": v(165.1, -196) * mm, "radius": 0.87 * mm});
            skCircle(sketch, "E1.65.15.0", {"center": v(165.1, -210) * mm, "radius": 0.87 * mm});
            skCircle(sketch, "E1.65.16.0", {"center": v(165.1, -224) * mm, "radius": 0.87 * mm});
            skCircle(sketch, "E1.65.17.0", {"center": v(165.1, -238) * mm, "radius": 0.87 * mm});
            skCircle(sketch, "E1.65.18.0", {"center": v(165.1, -252) * mm, "radius": 0.87 * mm});
            skCircle(sketch, "E1.66.0.0", {"center": v(167.64, 0) * mm, "radius": 0.87 * mm});
            skCircle(sketch, "E1.66.1.0", {"center": v(167.64, -14) * mm, "radius": 0.87 * mm});
            skCircle(sketch, "E1.66.2.0", {"center": v(167.64, -28) * mm, "radius": 0.87 * mm});
            skCircle(sketch, "E1.66.3.0", {"center": v(167.64, -42) * mm, "radius": 0.87 * mm});
            skCircle(sketch, "E1.66.4.0", {"center": v(167.64, -56) * mm, "radius": 0.87 * mm});
            skCircle(sketch, "E1.66.5.0", {"center": v(167.64, -70) * mm, "radius": 0.87 * mm});
            skCircle(sketch, "E1.66.6.0", {"center": v(167.64, -84) * mm, "radius": 0.87 * mm});
            skCircle(sketch, "E1.66.7.0", {"center": v(167.64, -98) * mm, "radius": 0.87 * mm});
            skCircle(sketch, "E1.66.8.0", {"center": v(167.64, -112) * mm, "radius": 0.87 * mm});
            skCircle(sketch, "E1.66.9.0", {"center": v(167.64, -126) * mm, "radius": 0.87 * mm});
            skCircle(sketch, "E1.66.10.0", {"center": v(167.64, -140) * mm, "radius": 0.87 * mm});
            skCircle(sketch, "E1.66.11.0", {"center": v(167.64, -154) * mm, "radius": 0.87 * mm});
            skCircle(sketch, "E1.66.12.0", {"center": v(167.64, -168) * mm, "radius": 0.87 * mm});
            skCircle(sketch, "E1.66.13.0", {"center": v(167.64, -182) * mm, "radius": 0.87 * mm});
            skCircle(sketch, "E1.66.14.0", {"center": v(167.64, -196) * mm, "radius": 0.87 * mm});
            skCircle(sketch, "E1.66.15.0", {"center": v(167.64, -210) * mm, "radius": 0.87 * mm});
            skCircle(sketch, "E1.66.16.0", {"center": v(167.64, -224) * mm, "radius": 0.87 * mm});
            skCircle(sketch, "E1.66.17.0", {"center": v(167.64, -238) * mm, "radius": 0.87 * mm});
            skCircle(sketch, "E1.66.18.0", {"center": v(167.64, -252) * mm, "radius": 0.87 * mm});
            skCircle(sketch, "E1.67.0.0", {"center": v(170.18, 0) * mm, "radius": 0.87 * mm});
            skCircle(sketch, "E1.67.1.0", {"center": v(170.18, -14) * mm, "radius": 0.87 * mm});
            skCircle(sketch, "E1.67.2.0", {"center": v(170.18, -28) * mm, "radius": 0.87 * mm});
            skCircle(sketch, "E1.67.3.0", {"center": v(170.18, -42) * mm, "radius": 0.87 * mm});
            skCircle(sketch, "E1.67.4.0", {"center": v(170.18, -56) * mm, "radius": 0.87 * mm});
            skCircle(sketch, "E1.67.5.0", {"center": v(170.18, -70) * mm, "radius": 0.87 * mm});
            skCircle(sketch, "E1.67.6.0", {"center": v(170.18, -84) * mm, "radius": 0.87 * mm});
            skCircle(sketch, "E1.67.7.0", {"center": v(170.18, -98) * mm, "radius": 0.87 * mm});
            skCircle(sketch, "E1.67.8.0", {"center": v(170.18, -112) * mm, "radius": 0.87 * mm});
            skCircle(sketch, "E1.67.9.0", {"center": v(170.18, -126) * mm, "radius": 0.87 * mm});
            skCircle(sketch, "E1.67.10.0", {"center": v(170.18, -140) * mm, "radius": 0.87 * mm});
            skCircle(sketch, "E1.67.11.0", {"center": v(170.18, -154) * mm, "radius": 0.87 * mm});
            skCircle(sketch, "E1.67.12.0", {"center": v(170.18, -168) * mm, "radius": 0.87 * mm});
            skCircle(sketch, "E1.67.13.0", {"center": v(170.18, -182) * mm, "radius": 0.87 * mm});
            skCircle(sketch, "E1.67.14.0", {"center": v(170.18, -196) * mm, "radius": 0.87 * mm});
            skCircle(sketch, "E1.67.15.0", {"center": v(170.18, -210) * mm, "radius": 0.87 * mm});
            skCircle(sketch, "E1.67.16.0", {"center": v(170.18, -224) * mm, "radius": 0.87 * mm});
            skCircle(sketch, "E1.67.17.0", {"center": v(170.18, -238) * mm, "radius": 0.87 * mm});
            skCircle(sketch, "E1.67.18.0", {"center": v(170.18, -252) * mm, "radius": 0.87 * mm});
            skCircle(sketch, "E1.68.0.0", {"center": v(172.72, 0) * mm, "radius": 0.87 * mm});
            skCircle(sketch, "E1.68.1.0", {"center": v(172.72, -14) * mm, "radius": 0.87 * mm});
            skCircle(sketch, "E1.68.2.0", {"center": v(172.72, -28) * mm, "radius": 0.87 * mm});
            skCircle(sketch, "E1.68.3.0", {"center": v(172.72, -42) * mm, "radius": 0.87 * mm});
            skCircle(sketch, "E1.68.4.0", {"center": v(172.72, -56) * mm, "radius": 0.87 * mm});
            skCircle(sketch, "E1.68.5.0", {"center": v(172.72, -70) * mm, "radius": 0.87 * mm});
            skCircle(sketch, "E1.68.6.0", {"center": v(172.72, -84) * mm, "radius": 0.87 * mm});
            skCircle(sketch, "E1.68.7.0", {"center": v(172.72, -98) * mm, "radius": 0.87 * mm});
            skCircle(sketch, "E1.68.8.0", {"center": v(172.72, -112) * mm, "radius": 0.87 * mm});
            skCircle(sketch, "E1.68.9.0", {"center": v(172.72, -126) * mm, "radius": 0.87 * mm});
            skCircle(sketch, "E1.68.10.0", {"center": v(172.72, -140) * mm, "radius": 0.87 * mm});
            skCircle(sketch, "E1.68.11.0", {"center": v(172.72, -154) * mm, "radius": 0.87 * mm});
            skCircle(sketch, "E1.68.12.0", {"center": v(172.72, -168) * mm, "radius": 0.87 * mm});
            skCircle(sketch, "E1.68.13.0", {"center": v(172.72, -182) * mm, "radius": 0.87 * mm});
            skCircle(sketch, "E1.68.14.0", {"center": v(172.72, -196) * mm, "radius": 0.87 * mm});
            skCircle(sketch, "E1.68.15.0", {"center": v(172.72, -210) * mm, "radius": 0.87 * mm});
            skCircle(sketch, "E1.68.16.0", {"center": v(172.72, -224) * mm, "radius": 0.87 * mm});
            skCircle(sketch, "E1.68.17.0", {"center": v(172.72, -238) * mm, "radius": 0.87 * mm});
            skCircle(sketch, "E1.68.18.0", {"center": v(172.72, -252) * mm, "radius": 0.87 * mm});
            skCircle(sketch, "E1.69.0.0", {"center": v(175.26, 0) * mm, "radius": 0.87 * mm});
            skCircle(sketch, "E1.69.1.0", {"center": v(175.26, -14) * mm, "radius": 0.87 * mm});
            skCircle(sketch, "E1.69.2.0", {"center": v(175.26, -28) * mm, "radius": 0.87 * mm});
            skCircle(sketch, "E1.69.3.0", {"center": v(175.26, -42) * mm, "radius": 0.87 * mm});
            skCircle(sketch, "E1.69.4.0", {"center": v(175.26, -56) * mm, "radius": 0.87 * mm});
            skCircle(sketch, "E1.69.5.0", {"center": v(175.26, -70) * mm, "radius": 0.87 * mm});
            skCircle(sketch, "E1.69.6.0", {"center": v(175.26, -84) * mm, "radius": 0.87 * mm});
            skCircle(sketch, "E1.69.7.0", {"center": v(175.26, -98) * mm, "radius": 0.87 * mm});
            skCircle(sketch, "E1.69.8.0", {"center": v(175.26, -112) * mm, "radius": 0.87 * mm});
            skCircle(sketch, "E1.69.9.0", {"center": v(175.26, -126) * mm, "radius": 0.87 * mm});
            skCircle(sketch, "E1.69.10.0", {"center": v(175.26, -140) * mm, "radius": 0.87 * mm});
            skCircle(sketch, "E1.69.11.0", {"center": v(175.26, -154) * mm, "radius": 0.87 * mm});
            skCircle(sketch, "E1.69.12.0", {"center": v(175.26, -168) * mm, "radius": 0.87 * mm});
            skCircle(sketch, "E1.69.13.0", {"center": v(175.26, -182) * mm, "radius": 0.87 * mm});
            skCircle(sketch, "E1.69.14.0", {"center": v(175.26, -196) * mm, "radius": 0.87 * mm});
            skCircle(sketch, "E1.69.15.0", {"center": v(175.26, -210) * mm, "radius": 0.87 * mm});
            skCircle(sketch, "E1.69.16.0", {"center": v(175.26, -224) * mm, "radius": 0.87 * mm});
            skCircle(sketch, "E1.69.17.0", {"center": v(175.26, -238) * mm, "radius": 0.87 * mm});
            skCircle(sketch, "E1.69.18.0", {"center": v(175.26, -252) * mm, "radius": 0.87 * mm});
            skCircle(sketch, "E1.70.0.0", {"center": v(177.8, 0) * mm, "radius": 0.87 * mm});
            skCircle(sketch, "E1.70.1.0", {"center": v(177.8, -14) * mm, "radius": 0.87 * mm});
            skCircle(sketch, "E1.70.2.0", {"center": v(177.8, -28) * mm, "radius": 0.87 * mm});
            skCircle(sketch, "E1.70.3.0", {"center": v(177.8, -42) * mm, "radius": 0.87 * mm});
            skCircle(sketch, "E1.70.4.0", {"center": v(177.8, -56) * mm, "radius": 0.87 * mm});
            skCircle(sketch, "E1.70.5.0", {"center": v(177.8, -70) * mm, "radius": 0.87 * mm});
            skCircle(sketch, "E1.70.6.0", {"center": v(177.8, -84) * mm, "radius": 0.87 * mm});
            skCircle(sketch, "E1.70.7.0", {"center": v(177.8, -98) * mm, "radius": 0.87 * mm});
            skCircle(sketch, "E1.70.8.0", {"center": v(177.8, -112) * mm, "radius": 0.87 * mm});
            skCircle(sketch, "E1.70.9.0", {"center": v(177.8, -126) * mm, "radius": 0.87 * mm});
            skCircle(sketch, "E1.70.10.0", {"center": v(177.8, -140) * mm, "radius": 0.87 * mm});
            skCircle(sketch, "E1.70.11.0", {"center": v(177.8, -154) * mm, "radius": 0.87 * mm});
            skCircle(sketch, "E1.70.12.0", {"center": v(177.8, -168) * mm, "radius": 0.87 * mm});
            skCircle(sketch, "E1.70.13.0", {"center": v(177.8, -182) * mm, "radius": 0.87 * mm});
            skCircle(sketch, "E1.70.14.0", {"center": v(177.8, -196) * mm, "radius": 0.87 * mm});
            skCircle(sketch, "E1.70.15.0", {"center": v(177.8, -210) * mm, "radius": 0.87 * mm});
            skCircle(sketch, "E1.70.16.0", {"center": v(177.8, -224) * mm, "radius": 0.87 * mm});
            skCircle(sketch, "E1.70.17.0", {"center": v(177.8, -238) * mm, "radius": 0.87 * mm});
            skCircle(sketch, "E1.70.18.0", {"center": v(177.8, -252) * mm, "radius": 0.87 * mm});
            skCircle(sketch, "E1.71.0.0", {"center": v(180.34, 0) * mm, "radius": 0.87 * mm});
            skCircle(sketch, "E1.71.1.0", {"center": v(180.34, -14) * mm, "radius": 0.87 * mm});
            skCircle(sketch, "E1.71.2.0", {"center": v(180.34, -28) * mm, "radius": 0.87 * mm});
            skCircle(sketch, "E1.71.3.0", {"center": v(180.34, -42) * mm, "radius": 0.87 * mm});
            skCircle(sketch, "E1.71.4.0", {"center": v(180.34, -56) * mm, "radius": 0.87 * mm});
            skCircle(sketch, "E1.71.5.0", {"center": v(180.34, -70) * mm, "radius": 0.87 * mm});
            skCircle(sketch, "E1.71.6.0", {"center": v(180.34, -84) * mm, "radius": 0.87 * mm});
            skCircle(sketch, "E1.71.7.0", {"center": v(180.34, -98) * mm, "radius": 0.87 * mm});
            skCircle(sketch, "E1.71.8.0", {"center": v(180.34, -112) * mm, "radius": 0.87 * mm});
            skCircle(sketch, "E1.71.9.0", {"center": v(180.34, -126) * mm, "radius": 0.87 * mm});
            skCircle(sketch, "E1.71.10.0", {"center": v(180.34, -140) * mm, "radius": 0.87 * mm});
            skCircle(sketch, "E1.71.11.0", {"center": v(180.34, -154) * mm, "radius": 0.87 * mm});
            skCircle(sketch, "E1.71.12.0", {"center": v(180.34, -168) * mm, "radius": 0.87 * mm});
            skCircle(sketch, "E1.71.13.0", {"center": v(180.34, -182) * mm, "radius": 0.87 * mm});
            skCircle(sketch, "E1.71.14.0", {"center": v(180.34, -196) * mm, "radius": 0.87 * mm});
            skCircle(sketch, "E1.71.15.0", {"center": v(180.34, -210) * mm, "radius": 0.87 * mm});
            skCircle(sketch, "E1.71.16.0", {"center": v(180.34, -224) * mm, "radius": 0.87 * mm});
            skCircle(sketch, "E1.71.17.0", {"center": v(180.34, -238) * mm, "radius": 0.87 * mm});
            skCircle(sketch, "E1.71.18.0", {"center": v(180.34, -252) * mm, "radius": 0.87 * mm});
            skCircle(sketch, "E1.72.0.0", {"center": v(182.88, 0) * mm, "radius": 0.87 * mm});
            skCircle(sketch, "E1.72.1.0", {"center": v(182.88, -14) * mm, "radius": 0.87 * mm});
            skCircle(sketch, "E1.72.2.0", {"center": v(182.88, -28) * mm, "radius": 0.87 * mm});
            skCircle(sketch, "E1.72.3.0", {"center": v(182.88, -42) * mm, "radius": 0.87 * mm});
            skCircle(sketch, "E1.72.4.0", {"center": v(182.88, -56) * mm, "radius": 0.87 * mm});
            skCircle(sketch, "E1.72.5.0", {"center": v(182.88, -70) * mm, "radius": 0.87 * mm});
            skCircle(sketch, "E1.72.6.0", {"center": v(182.88, -84) * mm, "radius": 0.87 * mm});
            skCircle(sketch, "E1.72.7.0", {"center": v(182.88, -98) * mm, "radius": 0.87 * mm});
            skCircle(sketch, "E1.72.8.0", {"center": v(182.88, -112) * mm, "radius": 0.87 * mm});
            skCircle(sketch, "E1.72.9.0", {"center": v(182.88, -126) * mm, "radius": 0.87 * mm});
            skCircle(sketch, "E1.72.10.0", {"center": v(182.88, -140) * mm, "radius": 0.87 * mm});
            skCircle(sketch, "E1.72.11.0", {"center": v(182.88, -154) * mm, "radius": 0.87 * mm});
            skCircle(sketch, "E1.72.12.0", {"center": v(182.88, -168) * mm, "radius": 0.87 * mm});
            skCircle(sketch, "E1.72.13.0", {"center": v(182.88, -182) * mm, "radius": 0.87 * mm});
            skCircle(sketch, "E1.72.14.0", {"center": v(182.88, -196) * mm, "radius": 0.87 * mm});
            skCircle(sketch, "E1.72.15.0", {"center": v(182.88, -210) * mm, "radius": 0.87 * mm});
            skCircle(sketch, "E1.72.16.0", {"center": v(182.88, -224) * mm, "radius": 0.87 * mm});
            skCircle(sketch, "E1.72.17.0", {"center": v(182.88, -238) * mm, "radius": 0.87 * mm});
            skCircle(sketch, "E1.72.18.0", {"center": v(182.88, -252) * mm, "radius": 0.87 * mm});
            skCircle(sketch, "E1.73.0.0", {"center": v(185.42, 0) * mm, "radius": 0.87 * mm});
            skCircle(sketch, "E1.73.1.0", {"center": v(185.42, -14) * mm, "radius": 0.87 * mm});
            skCircle(sketch, "E1.73.2.0", {"center": v(185.42, -28) * mm, "radius": 0.87 * mm});
            skCircle(sketch, "E1.73.3.0", {"center": v(185.42, -42) * mm, "radius": 0.87 * mm});
            skCircle(sketch, "E1.73.4.0", {"center": v(185.42, -56) * mm, "radius": 0.87 * mm});
            skCircle(sketch, "E1.73.5.0", {"center": v(185.42, -70) * mm, "radius": 0.87 * mm});
            skCircle(sketch, "E1.73.6.0", {"center": v(185.42, -84) * mm, "radius": 0.87 * mm});
            skCircle(sketch, "E1.73.7.0", {"center": v(185.42, -98) * mm, "radius": 0.87 * mm});
            skCircle(sketch, "E1.73.8.0", {"center": v(185.42, -112) * mm, "radius": 0.87 * mm});
            skCircle(sketch, "E1.73.9.0", {"center": v(185.42, -126) * mm, "radius": 0.87 * mm});
            skCircle(sketch, "E1.73.10.0", {"center": v(185.42, -140) * mm, "radius": 0.87 * mm});
            skCircle(sketch, "E1.73.11.0", {"center": v(185.42, -154) * mm, "radius": 0.87 * mm});
            skCircle(sketch, "E1.73.12.0", {"center": v(185.42, -168) * mm, "radius": 0.87 * mm});
            skCircle(sketch, "E1.73.13.0", {"center": v(185.42, -182) * mm, "radius": 0.87 * mm});
            skCircle(sketch, "E1.73.14.0", {"center": v(185.42, -196) * mm, "radius": 0.87 * mm});
            skCircle(sketch, "E1.73.15.0", {"center": v(185.42, -210) * mm, "radius": 0.87 * mm});
            skCircle(sketch, "E1.73.16.0", {"center": v(185.42, -224) * mm, "radius": 0.87 * mm});
            skCircle(sketch, "E1.73.17.0", {"center": v(185.42, -238) * mm, "radius": 0.87 * mm});
            skCircle(sketch, "E1.73.18.0", {"center": v(185.42, -252) * mm, "radius": 0.87 * mm});
            skCircle(sketch, "E1.74.0.0", {"center": v(187.96, 0) * mm, "radius": 0.87 * mm});
            skCircle(sketch, "E1.74.1.0", {"center": v(187.96, -14) * mm, "radius": 0.87 * mm});
            skCircle(sketch, "E1.74.2.0", {"center": v(187.96, -28) * mm, "radius": 0.87 * mm});
            skCircle(sketch, "E1.74.3.0", {"center": v(187.96, -42) * mm, "radius": 0.87 * mm});
            skCircle(sketch, "E1.74.4.0", {"center": v(187.96, -56) * mm, "radius": 0.87 * mm});
            skCircle(sketch, "E1.74.5.0", {"center": v(187.96, -70) * mm, "radius": 0.87 * mm});
            skCircle(sketch, "E1.74.6.0", {"center": v(187.96, -84) * mm, "radius": 0.87 * mm});
            skCircle(sketch, "E1.74.7.0", {"center": v(187.96, -98) * mm, "radius": 0.87 * mm});
            skCircle(sketch, "E1.74.8.0", {"center": v(187.96, -112) * mm, "radius": 0.87 * mm});
            skCircle(sketch, "E1.74.9.0", {"center": v(187.96, -126) * mm, "radius": 0.87 * mm});
            skCircle(sketch, "E1.74.10.0", {"center": v(187.96, -140) * mm, "radius": 0.87 * mm});
            skCircle(sketch, "E1.74.11.0", {"center": v(187.96, -154) * mm, "radius": 0.87 * mm});
            skCircle(sketch, "E1.74.12.0", {"center": v(187.96, -168) * mm, "radius": 0.87 * mm});
            skCircle(sketch, "E1.74.13.0", {"center": v(187.96, -182) * mm, "radius": 0.87 * mm});
            skCircle(sketch, "E1.74.14.0", {"center": v(187.96, -196) * mm, "radius": 0.87 * mm});
            skCircle(sketch, "E1.74.15.0", {"center": v(187.96, -210) * mm, "radius": 0.87 * mm});
            skCircle(sketch, "E1.74.16.0", {"center": v(187.96, -224) * mm, "radius": 0.87 * mm});
            skCircle(sketch, "E1.74.17.0", {"center": v(187.96, -238) * mm, "radius": 0.87 * mm});
            skCircle(sketch, "E1.74.18.0", {"center": v(187.96, -252) * mm, "radius": 0.87 * mm});
            skCircle(sketch, "E1.75.0.0", {"center": v(190.5, 0) * mm, "radius": 0.87 * mm});
            skCircle(sketch, "E1.75.1.0", {"center": v(190.5, -14) * mm, "radius": 0.87 * mm});
            skCircle(sketch, "E1.75.2.0", {"center": v(190.5, -28) * mm, "radius": 0.87 * mm});
            skCircle(sketch, "E1.75.3.0", {"center": v(190.5, -42) * mm, "radius": 0.87 * mm});
            skCircle(sketch, "E1.75.4.0", {"center": v(190.5, -56) * mm, "radius": 0.87 * mm});
            skCircle(sketch, "E1.75.5.0", {"center": v(190.5, -70) * mm, "radius": 0.87 * mm});
            skCircle(sketch, "E1.75.6.0", {"center": v(190.5, -84) * mm, "radius": 0.87 * mm});
            skCircle(sketch, "E1.75.7.0", {"center": v(190.5, -98) * mm, "radius": 0.87 * mm});
            skCircle(sketch, "E1.75.8.0", {"center": v(190.5, -112) * mm, "radius": 0.87 * mm});
            skCircle(sketch, "E1.75.9.0", {"center": v(190.5, -126) * mm, "radius": 0.87 * mm});
            skCircle(sketch, "E1.75.10.0", {"center": v(190.5, -140) * mm, "radius": 0.87 * mm});
            skCircle(sketch, "E1.75.11.0", {"center": v(190.5, -154) * mm, "radius": 0.87 * mm});
            skCircle(sketch, "E1.75.12.0", {"center": v(190.5, -168) * mm, "radius": 0.87 * mm});
            skCircle(sketch, "E1.75.13.0", {"center": v(190.5, -182) * mm, "radius": 0.87 * mm});
            skCircle(sketch, "E1.75.14.0", {"center": v(190.5, -196) * mm, "radius": 0.87 * mm});
            skCircle(sketch, "E1.75.15.0", {"center": v(190.5, -210) * mm, "radius": 0.87 * mm});
            skCircle(sketch, "E1.75.16.0", {"center": v(190.5, -224) * mm, "radius": 0.87 * mm});
            skCircle(sketch, "E1.75.17.0", {"center": v(190.5, -238) * mm, "radius": 0.87 * mm});
            skCircle(sketch, "E1.75.18.0", {"center": v(190.5, -252) * mm, "radius": 0.87 * mm});
            skCircle(sketch, "E1.76.0.0", {"center": v(193.04, 0) * mm, "radius": 0.87 * mm});
            skCircle(sketch, "E1.76.1.0", {"center": v(193.04, -14) * mm, "radius": 0.87 * mm});
            skCircle(sketch, "E1.76.2.0", {"center": v(193.04, -28) * mm, "radius": 0.87 * mm});
            skCircle(sketch, "E1.76.3.0", {"center": v(193.04, -42) * mm, "radius": 0.87 * mm});
            skCircle(sketch, "E1.76.4.0", {"center": v(193.04, -56) * mm, "radius": 0.87 * mm});
            skCircle(sketch, "E1.76.5.0", {"center": v(193.04, -70) * mm, "radius": 0.87 * mm});
            skCircle(sketch, "E1.76.6.0", {"center": v(193.04, -84) * mm, "radius": 0.87 * mm});
            skCircle(sketch, "E1.76.7.0", {"center": v(193.04, -98) * mm, "radius": 0.87 * mm});
            skCircle(sketch, "E1.76.8.0", {"center": v(193.04, -112) * mm, "radius": 0.87 * mm});
            skCircle(sketch, "E1.76.9.0", {"center": v(193.04, -126) * mm, "radius": 0.87 * mm});
            skCircle(sketch, "E1.76.10.0", {"center": v(193.04, -140) * mm, "radius": 0.87 * mm});
            skCircle(sketch, "E1.76.11.0", {"center": v(193.04, -154) * mm, "radius": 0.87 * mm});
            skCircle(sketch, "E1.76.12.0", {"center": v(193.04, -168) * mm, "radius": 0.87 * mm});
            skCircle(sketch, "E1.76.13.0", {"center": v(193.04, -182) * mm, "radius": 0.87 * mm});
            skCircle(sketch, "E1.76.14.0", {"center": v(193.04, -196) * mm, "radius": 0.87 * mm});
            skCircle(sketch, "E1.76.15.0", {"center": v(193.04, -210) * mm, "radius": 0.87 * mm});
            skCircle(sketch, "E1.76.16.0", {"center": v(193.04, -224) * mm, "radius": 0.87 * mm});
            skCircle(sketch, "E1.76.17.0", {"center": v(193.04, -238) * mm, "radius": 0.87 * mm});
            skCircle(sketch, "E1.76.18.0", {"center": v(193.04, -252) * mm, "radius": 0.87 * mm});
            skCircle(sketch, "E1.77.0.0", {"center": v(195.58, 0) * mm, "radius": 0.87 * mm});
            skCircle(sketch, "E1.77.1.0", {"center": v(195.58, -14) * mm, "radius": 0.87 * mm});
            skCircle(sketch, "E1.77.2.0", {"center": v(195.58, -28) * mm, "radius": 0.87 * mm});
            skCircle(sketch, "E1.77.3.0", {"center": v(195.58, -42) * mm, "radius": 0.87 * mm});
            skCircle(sketch, "E1.77.4.0", {"center": v(195.58, -56) * mm, "radius": 0.87 * mm});
            skCircle(sketch, "E1.77.5.0", {"center": v(195.58, -70) * mm, "radius": 0.87 * mm});
            skCircle(sketch, "E1.77.6.0", {"center": v(195.58, -84) * mm, "radius": 0.87 * mm});
            skCircle(sketch, "E1.77.7.0", {"center": v(195.58, -98) * mm, "radius": 0.87 * mm});
            skCircle(sketch, "E1.77.8.0", {"center": v(195.58, -112) * mm, "radius": 0.87 * mm});
            skCircle(sketch, "E1.77.9.0", {"center": v(195.58, -126) * mm, "radius": 0.87 * mm});
            skCircle(sketch, "E1.77.10.0", {"center": v(195.58, -140) * mm, "radius": 0.87 * mm});
            skCircle(sketch, "E1.77.11.0", {"center": v(195.58, -154) * mm, "radius": 0.87 * mm});
            skCircle(sketch, "E1.77.12.0", {"center": v(195.58, -168) * mm, "radius": 0.87 * mm});
            skCircle(sketch, "E1.77.13.0", {"center": v(195.58, -182) * mm, "radius": 0.87 * mm});
            skCircle(sketch, "E1.77.14.0", {"center": v(195.58, -196) * mm, "radius": 0.87 * mm});
            skCircle(sketch, "E1.77.15.0", {"center": v(195.58, -210) * mm, "radius": 0.87 * mm});
            skCircle(sketch, "E1.77.16.0", {"center": v(195.58, -224) * mm, "radius": 0.87 * mm});
            skCircle(sketch, "E1.77.17.0", {"center": v(195.58, -238) * mm, "radius": 0.87 * mm});
            skCircle(sketch, "E1.77.18.0", {"center": v(195.58, -252) * mm, "radius": 0.87 * mm});
            skCircle(sketch, "E1.78.0.0", {"center": v(198.12, 0) * mm, "radius": 0.87 * mm});
            skCircle(sketch, "E1.78.1.0", {"center": v(198.12, -14) * mm, "radius": 0.87 * mm});
            skCircle(sketch, "E1.78.2.0", {"center": v(198.12, -28) * mm, "radius": 0.87 * mm});
            skCircle(sketch, "E1.78.3.0", {"center": v(198.12, -42) * mm, "radius": 0.87 * mm});
            skCircle(sketch, "E1.78.4.0", {"center": v(198.12, -56) * mm, "radius": 0.87 * mm});
            skCircle(sketch, "E1.78.5.0", {"center": v(198.12, -70) * mm, "radius": 0.87 * mm});
            skCircle(sketch, "E1.78.6.0", {"center": v(198.12, -84) * mm, "radius": 0.87 * mm});
            skCircle(sketch, "E1.78.7.0", {"center": v(198.12, -98) * mm, "radius": 0.87 * mm});
            skCircle(sketch, "E1.78.8.0", {"center": v(198.12, -112) * mm, "radius": 0.87 * mm});
            skCircle(sketch, "E1.78.9.0", {"center": v(198.12, -126) * mm, "radius": 0.87 * mm});
            skCircle(sketch, "E1.78.10.0", {"center": v(198.12, -140) * mm, "radius": 0.87 * mm});
            skCircle(sketch, "E1.78.11.0", {"center": v(198.12, -154) * mm, "radius": 0.87 * mm});
            skCircle(sketch, "E1.78.12.0", {"center": v(198.12, -168) * mm, "radius": 0.87 * mm});
            skCircle(sketch, "E1.78.13.0", {"center": v(198.12, -182) * mm, "radius": 0.87 * mm});
            skCircle(sketch, "E1.78.14.0", {"center": v(198.12, -196) * mm, "radius": 0.87 * mm});
            skCircle(sketch, "E1.78.15.0", {"center": v(198.12, -210) * mm, "radius": 0.87 * mm});
            skCircle(sketch, "E1.78.16.0", {"center": v(198.12, -224) * mm, "radius": 0.87 * mm});
            skCircle(sketch, "E1.78.17.0", {"center": v(198.12, -238) * mm, "radius": 0.87 * mm});
            skCircle(sketch, "E1.78.18.0", {"center": v(198.12, -252) * mm, "radius": 0.87 * mm});
            skCircle(sketch, "E1.79.0.0", {"center": v(200.66, 0) * mm, "radius": 0.87 * mm});
            skCircle(sketch, "E1.79.1.0", {"center": v(200.66, -14) * mm, "radius": 0.87 * mm});
            skCircle(sketch, "E1.79.2.0", {"center": v(200.66, -28) * mm, "radius": 0.87 * mm});
            skCircle(sketch, "E1.79.3.0", {"center": v(200.66, -42) * mm, "radius": 0.87 * mm});
            skCircle(sketch, "E1.79.4.0", {"center": v(200.66, -56) * mm, "radius": 0.87 * mm});
            skCircle(sketch, "E1.79.5.0", {"center": v(200.66, -70) * mm, "radius": 0.87 * mm});
            skCircle(sketch, "E1.79.6.0", {"center": v(200.66, -84) * mm, "radius": 0.87 * mm});
            skCircle(sketch, "E1.79.7.0", {"center": v(200.66, -98) * mm, "radius": 0.87 * mm});
            skCircle(sketch, "E1.79.8.0", {"center": v(200.66, -112) * mm, "radius": 0.87 * mm});
            skCircle(sketch, "E1.79.9.0", {"center": v(200.66, -126) * mm, "radius": 0.87 * mm});
            skCircle(sketch, "E1.79.10.0", {"center": v(200.66, -140) * mm, "radius": 0.87 * mm});
            skCircle(sketch, "E1.79.11.0", {"center": v(200.66, -154) * mm, "radius": 0.87 * mm});
            skCircle(sketch, "E1.79.12.0", {"center": v(200.66, -168) * mm, "radius": 0.87 * mm});
            skCircle(sketch, "E1.79.13.0", {"center": v(200.66, -182) * mm, "radius": 0.87 * mm});
            skCircle(sketch, "E1.79.14.0", {"center": v(200.66, -196) * mm, "radius": 0.87 * mm});
            skCircle(sketch, "E1.79.15.0", {"center": v(200.66, -210) * mm, "radius": 0.87 * mm});
            skCircle(sketch, "E1.79.16.0", {"center": v(200.66, -224) * mm, "radius": 0.87 * mm});
            skCircle(sketch, "E1.79.17.0", {"center": v(200.66, -238) * mm, "radius": 0.87 * mm});
            skCircle(sketch, "E1.79.18.0", {"center": v(200.66, -252) * mm, "radius": 0.87 * mm});
            skCircle(sketch, "E1.80.0.0", {"center": v(203.2, 0) * mm, "radius": 0.87 * mm});
            skCircle(sketch, "E1.80.1.0", {"center": v(203.2, -14) * mm, "radius": 0.87 * mm});
            skCircle(sketch, "E1.80.2.0", {"center": v(203.2, -28) * mm, "radius": 0.87 * mm});
            skCircle(sketch, "E1.80.3.0", {"center": v(203.2, -42) * mm, "radius": 0.87 * mm});
            skCircle(sketch, "E1.80.4.0", {"center": v(203.2, -56) * mm, "radius": 0.87 * mm});
            skCircle(sketch, "E1.80.5.0", {"center": v(203.2, -70) * mm, "radius": 0.87 * mm});
            skCircle(sketch, "E1.80.6.0", {"center": v(203.2, -84) * mm, "radius": 0.87 * mm});
            skCircle(sketch, "E1.80.7.0", {"center": v(203.2, -98) * mm, "radius": 0.87 * mm});
            skCircle(sketch, "E1.80.8.0", {"center": v(203.2, -112) * mm, "radius": 0.87 * mm});
            skCircle(sketch, "E1.80.9.0", {"center": v(203.2, -126) * mm, "radius": 0.87 * mm});
            skCircle(sketch, "E1.80.10.0", {"center": v(203.2, -140) * mm, "radius": 0.87 * mm});
            skCircle(sketch, "E1.80.11.0", {"center": v(203.2, -154) * mm, "radius": 0.87 * mm});
            skCircle(sketch, "E1.80.12.0", {"center": v(203.2, -168) * mm, "radius": 0.87 * mm});
            skCircle(sketch, "E1.80.13.0", {"center": v(203.2, -182) * mm, "radius": 0.87 * mm});
            skCircle(sketch, "E1.80.14.0", {"center": v(203.2, -196) * mm, "radius": 0.87 * mm});
            skCircle(sketch, "E1.80.15.0", {"center": v(203.2, -210) * mm, "radius": 0.87 * mm});
            skCircle(sketch, "E1.80.16.0", {"center": v(203.2, -224) * mm, "radius": 0.87 * mm});
            skCircle(sketch, "E1.80.17.0", {"center": v(203.2, -238) * mm, "radius": 0.87 * mm});
            skCircle(sketch, "E1.80.18.0", {"center": v(203.2, -252) * mm, "radius": 0.87 * mm});
            skCircle(sketch, "E1.81.0.0", {"center": v(205.74, 0) * mm, "radius": 0.87 * mm});
            skCircle(sketch, "E1.81.1.0", {"center": v(205.74, -14) * mm, "radius": 0.87 * mm});
            skCircle(sketch, "E1.81.2.0", {"center": v(205.74, -28) * mm, "radius": 0.87 * mm});
            skCircle(sketch, "E1.81.3.0", {"center": v(205.74, -42) * mm, "radius": 0.87 * mm});
            skCircle(sketch, "E1.81.4.0", {"center": v(205.74, -56) * mm, "radius": 0.87 * mm});
            skCircle(sketch, "E1.81.5.0", {"center": v(205.74, -70) * mm, "radius": 0.87 * mm});
            skCircle(sketch, "E1.81.6.0", {"center": v(205.74, -84) * mm, "radius": 0.87 * mm});
            skCircle(sketch, "E1.81.7.0", {"center": v(205.74, -98) * mm, "radius": 0.87 * mm});
            skCircle(sketch, "E1.81.8.0", {"center": v(205.74, -112) * mm, "radius": 0.87 * mm});
            skCircle(sketch, "E1.81.9.0", {"center": v(205.74, -126) * mm, "radius": 0.87 * mm});
            skCircle(sketch, "E1.81.10.0", {"center": v(205.74, -140) * mm, "radius": 0.87 * mm});
            skCircle(sketch, "E1.81.11.0", {"center": v(205.74, -154) * mm, "radius": 0.87 * mm});
            skCircle(sketch, "E1.81.12.0", {"center": v(205.74, -168) * mm, "radius": 0.87 * mm});
            skCircle(sketch, "E1.81.13.0", {"center": v(205.74, -182) * mm, "radius": 0.87 * mm});
            skCircle(sketch, "E1.81.14.0", {"center": v(205.74, -196) * mm, "radius": 0.87 * mm});
            skCircle(sketch, "E1.81.15.0", {"center": v(205.74, -210) * mm, "radius": 0.87 * mm});
            skCircle(sketch, "E1.81.16.0", {"center": v(205.74, -224) * mm, "radius": 0.87 * mm});
            skCircle(sketch, "E1.81.17.0", {"center": v(205.74, -238) * mm, "radius": 0.87 * mm});
            skCircle(sketch, "E1.81.18.0", {"center": v(205.74, -252) * mm, "radius": 0.87 * mm});
            skCircle(sketch, "E1.82.0.0", {"center": v(208.28, 0) * mm, "radius": 0.87 * mm});
            skCircle(sketch, "E1.82.1.0", {"center": v(208.28, -14) * mm, "radius": 0.87 * mm});
            skCircle(sketch, "E1.82.2.0", {"center": v(208.28, -28) * mm, "radius": 0.87 * mm});
            skCircle(sketch, "E1.82.3.0", {"center": v(208.28, -42) * mm, "radius": 0.87 * mm});
            skCircle(sketch, "E1.82.4.0", {"center": v(208.28, -56) * mm, "radius": 0.87 * mm});
            skCircle(sketch, "E1.82.5.0", {"center": v(208.28, -70) * mm, "radius": 0.87 * mm});
            skCircle(sketch, "E1.82.6.0", {"center": v(208.28, -84) * mm, "radius": 0.87 * mm});
            skCircle(sketch, "E1.82.7.0", {"center": v(208.28, -98) * mm, "radius": 0.87 * mm});
            skCircle(sketch, "E1.82.8.0", {"center": v(208.28, -112) * mm, "radius": 0.87 * mm});
            skCircle(sketch, "E1.82.9.0", {"center": v(208.28, -126) * mm, "radius": 0.87 * mm});
            skCircle(sketch, "E1.82.10.0", {"center": v(208.28, -140) * mm, "radius": 0.87 * mm});
            skCircle(sketch, "E1.82.11.0", {"center": v(208.28, -154) * mm, "radius": 0.87 * mm});
            skCircle(sketch, "E1.82.12.0", {"center": v(208.28, -168) * mm, "radius": 0.87 * mm});
            skCircle(sketch, "E1.82.13.0", {"center": v(208.28, -182) * mm, "radius": 0.87 * mm});
            skCircle(sketch, "E1.82.14.0", {"center": v(208.28, -196) * mm, "radius": 0.87 * mm});
            skCircle(sketch, "E1.82.15.0", {"center": v(208.28, -210) * mm, "radius": 0.87 * mm});
            skCircle(sketch, "E1.82.16.0", {"center": v(208.28, -224) * mm, "radius": 0.87 * mm});
            skCircle(sketch, "E1.82.17.0", {"center": v(208.28, -238) * mm, "radius": 0.87 * mm});
            skCircle(sketch, "E1.82.18.0", {"center": v(208.28, -252) * mm, "radius": 0.87 * mm});
            skCircle(sketch, "E1.83.0.0", {"center": v(210.82, 0) * mm, "radius": 0.87 * mm});
            skCircle(sketch, "E1.83.1.0", {"center": v(210.82, -14) * mm, "radius": 0.87 * mm});
            skCircle(sketch, "E1.83.2.0", {"center": v(210.82, -28) * mm, "radius": 0.87 * mm});
            skCircle(sketch, "E1.83.3.0", {"center": v(210.82, -42) * mm, "radius": 0.87 * mm});
            skCircle(sketch, "E1.83.4.0", {"center": v(210.82, -56) * mm, "radius": 0.87 * mm});
            skCircle(sketch, "E1.83.5.0", {"center": v(210.82, -70) * mm, "radius": 0.87 * mm});
            skCircle(sketch, "E1.83.6.0", {"center": v(210.82, -84) * mm, "radius": 0.87 * mm});
            skCircle(sketch, "E1.83.7.0", {"center": v(210.82, -98) * mm, "radius": 0.87 * mm});
            skCircle(sketch, "E1.83.8.0", {"center": v(210.82, -112) * mm, "radius": 0.87 * mm});
            skCircle(sketch, "E1.83.9.0", {"center": v(210.82, -126) * mm, "radius": 0.87 * mm});
            skCircle(sketch, "E1.83.10.0", {"center": v(210.82, -140) * mm, "radius": 0.87 * mm});
            skCircle(sketch, "E1.83.11.0", {"center": v(210.82, -154) * mm, "radius": 0.87 * mm});
            skCircle(sketch, "E1.83.12.0", {"center": v(210.82, -168) * mm, "radius": 0.87 * mm});
            skCircle(sketch, "E1.83.13.0", {"center": v(210.82, -182) * mm, "radius": 0.87 * mm});
            skCircle(sketch, "E1.83.14.0", {"center": v(210.82, -196) * mm, "radius": 0.87 * mm});
            skCircle(sketch, "E1.83.15.0", {"center": v(210.82, -210) * mm, "radius": 0.87 * mm});
            skCircle(sketch, "E1.83.16.0", {"center": v(210.82, -224) * mm, "radius": 0.87 * mm});
            skCircle(sketch, "E1.83.17.0", {"center": v(210.82, -238) * mm, "radius": 0.87 * mm});
            skCircle(sketch, "E1.83.18.0", {"center": v(210.82, -252) * mm, "radius": 0.87 * mm});
            skCircle(sketch, "E1.84.0.0", {"center": v(213.36, 0) * mm, "radius": 0.87 * mm});
            skCircle(sketch, "E1.84.1.0", {"center": v(213.36, -14) * mm, "radius": 0.87 * mm});
            skCircle(sketch, "E1.84.2.0", {"center": v(213.36, -28) * mm, "radius": 0.87 * mm});
            skCircle(sketch, "E1.84.3.0", {"center": v(213.36, -42) * mm, "radius": 0.87 * mm});
            skCircle(sketch, "E1.84.4.0", {"center": v(213.36, -56) * mm, "radius": 0.87 * mm});
            skCircle(sketch, "E1.84.5.0", {"center": v(213.36, -70) * mm, "radius": 0.87 * mm});
            skCircle(sketch, "E1.84.6.0", {"center": v(213.36, -84) * mm, "radius": 0.87 * mm});
            skCircle(sketch, "E1.84.7.0", {"center": v(213.36, -98) * mm, "radius": 0.87 * mm});
            skCircle(sketch, "E1.84.8.0", {"center": v(213.36, -112) * mm, "radius": 0.87 * mm});
            skCircle(sketch, "E1.84.9.0", {"center": v(213.36, -126) * mm, "radius": 0.87 * mm});
            skCircle(sketch, "E1.84.10.0", {"center": v(213.36, -140) * mm, "radius": 0.87 * mm});
            skCircle(sketch, "E1.84.11.0", {"center": v(213.36, -154) * mm, "radius": 0.87 * mm});
            skCircle(sketch, "E1.84.12.0", {"center": v(213.36, -168) * mm, "radius": 0.87 * mm});
            skCircle(sketch, "E1.84.13.0", {"center": v(213.36, -182) * mm, "radius": 0.87 * mm});
            skCircle(sketch, "E1.84.14.0", {"center": v(213.36, -196) * mm, "radius": 0.87 * mm});
            skCircle(sketch, "E1.84.15.0", {"center": v(213.36, -210) * mm, "radius": 0.87 * mm});
            skCircle(sketch, "E1.84.16.0", {"center": v(213.36, -224) * mm, "radius": 0.87 * mm});
            skCircle(sketch, "E1.84.17.0", {"center": v(213.36, -238) * mm, "radius": 0.87 * mm});
            skCircle(sketch, "E1.84.18.0", {"center": v(213.36, -252) * mm, "radius": 0.87 * mm});
            skCircle(sketch, "E1.85.0.0", {"center": v(215.9, 0) * mm, "radius": 0.87 * mm});
            skCircle(sketch, "E1.85.1.0", {"center": v(215.9, -14) * mm, "radius": 0.87 * mm});
            skCircle(sketch, "E1.85.2.0", {"center": v(215.9, -28) * mm, "radius": 0.87 * mm});
            skCircle(sketch, "E1.85.3.0", {"center": v(215.9, -42) * mm, "radius": 0.87 * mm});
            skCircle(sketch, "E1.85.4.0", {"center": v(215.9, -56) * mm, "radius": 0.87 * mm});
            skCircle(sketch, "E1.85.5.0", {"center": v(215.9, -70) * mm, "radius": 0.87 * mm});
            skCircle(sketch, "E1.85.6.0", {"center": v(215.9, -84) * mm, "radius": 0.87 * mm});
            skCircle(sketch, "E1.85.7.0", {"center": v(215.9, -98) * mm, "radius": 0.87 * mm});
            skCircle(sketch, "E1.85.8.0", {"center": v(215.9, -112) * mm, "radius": 0.87 * mm});
            skCircle(sketch, "E1.85.9.0", {"center": v(215.9, -126) * mm, "radius": 0.87 * mm});
            skCircle(sketch, "E1.85.10.0", {"center": v(215.9, -140) * mm, "radius": 0.87 * mm});
            skCircle(sketch, "E1.85.11.0", {"center": v(215.9, -154) * mm, "radius": 0.87 * mm});
            skCircle(sketch, "E1.85.12.0", {"center": v(215.9, -168) * mm, "radius": 0.87 * mm});
            skCircle(sketch, "E1.85.13.0", {"center": v(215.9, -182) * mm, "radius": 0.87 * mm});
            skCircle(sketch, "E1.85.14.0", {"center": v(215.9, -196) * mm, "radius": 0.87 * mm});
            skCircle(sketch, "E1.85.15.0", {"center": v(215.9, -210) * mm, "radius": 0.87 * mm});
            skCircle(sketch, "E1.85.16.0", {"center": v(215.9, -224) * mm, "radius": 0.87 * mm});
            skCircle(sketch, "E1.85.17.0", {"center": v(215.9, -238) * mm, "radius": 0.87 * mm});
            skCircle(sketch, "E1.85.18.0", {"center": v(215.9, -252) * mm, "radius": 0.87 * mm});
            skLineSegment(sketch, "E1.direction1", {"start": v(0, 0) * mm, "end": v(2.54, 0) * mm, "construction": true});
            skLineSegment(sketch, "E1.direction2", {"start": v(0, 0) * mm, "end": v(0, -14) * mm, "construction": true});
            skLineSegment(sketch, "E2.bottom", {"start": v(-30, -282) * mm, "end": v(293.44, -282) * mm});
            skLineSegment(sketch, "E2.top", {"start": v(-30, 30) * mm, "end": v(293.44, 30) * mm});
            skLineSegment(sketch, "E2.left", {"start": v(-30, -282) * mm, "end": v(-30, 30) * mm});
            skLineSegment(sketch, "E2.right", {"start": v(293.44, -282) * mm, "end": v(293.44, 30) * mm});
            skCircle(sketch, "E3.0.86.0", {"center": v(218.44, 0) * mm, "radius": 0.87 * mm});
            skCircle(sketch, "E3.0.86.1", {"center": v(218.44, -14) * mm, "radius": 0.87 * mm});
            skCircle(sketch, "E3.0.86.2", {"center": v(218.44, -28) * mm, "radius": 0.87 * mm});
            skCircle(sketch, "E3.0.86.3", {"center": v(218.44, -42) * mm, "radius": 0.87 * mm});
            skCircle(sketch, "E3.0.86.4", {"center": v(218.44, -56) * mm, "radius": 0.87 * mm});
            skCircle(sketch, "E3.0.86.5", {"center": v(218.44, -70) * mm, "radius": 0.87 * mm});
            skCircle(sketch, "E3.0.86.6", {"center": v(218.44, -84) * mm, "radius": 0.87 * mm});
            skCircle(sketch, "E3.0.86.7", {"center": v(218.44, -98) * mm, "radius": 0.87 * mm});
            skCircle(sketch, "E3.0.86.8", {"center": v(218.44, -112) * mm, "radius": 0.87 * mm});
            skCircle(sketch, "E3.0.86.9", {"center": v(218.44, -126) * mm, "radius": 0.87 * mm});
            skCircle(sketch, "E3.0.86.10", {"center": v(218.44, -140) * mm, "radius": 0.87 * mm});
            skCircle(sketch, "E3.0.86.11", {"center": v(218.44, -154) * mm, "radius": 0.87 * mm});
            skCircle(sketch, "E3.0.86.12", {"center": v(218.44, -168) * mm, "radius": 0.87 * mm});
            skCircle(sketch, "E3.0.86.13", {"center": v(218.44, -182) * mm, "radius": 0.87 * mm});
            skCircle(sketch, "E3.0.86.14", {"center": v(218.44, -196) * mm, "radius": 0.87 * mm});
            skCircle(sketch, "E3.0.86.15", {"center": v(218.44, -210) * mm, "radius": 0.87 * mm});
            skCircle(sketch, "E3.0.86.16", {"center": v(218.44, -224) * mm, "radius": 0.87 * mm});
            skCircle(sketch, "E3.0.86.17", {"center": v(218.44, -238) * mm, "radius": 0.87 * mm});
            skCircle(sketch, "E3.0.86.18", {"center": v(218.44, -252) * mm, "radius": 0.87 * mm});
            skCircle(sketch, "E3.0.87.0", {"center": v(220.98, 0) * mm, "radius": 0.87 * mm});
            skCircle(sketch, "E3.0.87.1", {"center": v(220.98, -14) * mm, "radius": 0.87 * mm});
            skCircle(sketch, "E3.0.87.2", {"center": v(220.98, -28) * mm, "radius": 0.87 * mm});
            skCircle(sketch, "E3.0.87.3", {"center": v(220.98, -42) * mm, "radius": 0.87 * mm});
            skCircle(sketch, "E3.0.87.4", {"center": v(220.98, -56) * mm, "radius": 0.87 * mm});
            skCircle(sketch, "E3.0.87.5", {"center": v(220.98, -70) * mm, "radius": 0.87 * mm});
            skCircle(sketch, "E3.0.87.6", {"center": v(220.98, -84) * mm, "radius": 0.87 * mm});
            skCircle(sketch, "E3.0.87.7", {"center": v(220.98, -98) * mm, "radius": 0.87 * mm});
            skCircle(sketch, "E3.0.87.8", {"center": v(220.98, -112) * mm, "radius": 0.87 * mm});
            skCircle(sketch, "E3.0.87.9", {"center": v(220.98, -126) * mm, "radius": 0.87 * mm});
            skCircle(sketch, "E3.0.87.10", {"center": v(220.98, -140) * mm, "radius": 0.87 * mm});
            skCircle(sketch, "E3.0.87.11", {"center": v(220.98, -154) * mm, "radius": 0.87 * mm});
            skCircle(sketch, "E3.0.87.12", {"center": v(220.98, -168) * mm, "radius": 0.87 * mm});
            skCircle(sketch, "E3.0.87.13", {"center": v(220.98, -182) * mm, "radius": 0.87 * mm});
            skCircle(sketch, "E3.0.87.14", {"center": v(220.98, -196) * mm, "radius": 0.87 * mm});
            skCircle(sketch, "E3.0.87.15", {"center": v(220.98, -210) * mm, "radius": 0.87 * mm});
            skCircle(sketch, "E3.0.87.16", {"center": v(220.98, -224) * mm, "radius": 0.87 * mm});
            skCircle(sketch, "E3.0.87.17", {"center": v(220.98, -238) * mm, "radius": 0.87 * mm});
            skCircle(sketch, "E3.0.87.18", {"center": v(220.98, -252) * mm, "radius": 0.87 * mm});
            skCircle(sketch, "E3.0.88.0", {"center": v(223.52, 0) * mm, "radius": 0.87 * mm});
            skCircle(sketch, "E3.0.88.1", {"center": v(223.52, -14) * mm, "radius": 0.87 * mm});
            skCircle(sketch, "E3.0.88.2", {"center": v(223.52, -28) * mm, "radius": 0.87 * mm});
            skCircle(sketch, "E3.0.88.3", {"center": v(223.52, -42) * mm, "radius": 0.87 * mm});
            skCircle(sketch, "E3.0.88.4", {"center": v(223.52, -56) * mm, "radius": 0.87 * mm});
            skCircle(sketch, "E3.0.88.5", {"center": v(223.52, -70) * mm, "radius": 0.87 * mm});
            skCircle(sketch, "E3.0.88.6", {"center": v(223.52, -84) * mm, "radius": 0.87 * mm});
            skCircle(sketch, "E3.0.88.7", {"center": v(223.52, -98) * mm, "radius": 0.87 * mm});
            skCircle(sketch, "E3.0.88.8", {"center": v(223.52, -112) * mm, "radius": 0.87 * mm});
            skCircle(sketch, "E3.0.88.9", {"center": v(223.52, -126) * mm, "radius": 0.87 * mm});
            skCircle(sketch, "E3.0.88.10", {"center": v(223.52, -140) * mm, "radius": 0.87 * mm});
            skCircle(sketch, "E3.0.88.11", {"center": v(223.52, -154) * mm, "radius": 0.87 * mm});
            skCircle(sketch, "E3.0.88.12", {"center": v(223.52, -168) * mm, "radius": 0.87 * mm});
            skCircle(sketch, "E3.0.88.13", {"center": v(223.52, -182) * mm, "radius": 0.87 * mm});
            skCircle(sketch, "E3.0.88.14", {"center": v(223.52, -196) * mm, "radius": 0.87 * mm});
            skCircle(sketch, "E3.0.88.15", {"center": v(223.52, -210) * mm, "radius": 0.87 * mm});
            skCircle(sketch, "E3.0.88.16", {"center": v(223.52, -224) * mm, "radius": 0.87 * mm});
            skCircle(sketch, "E3.0.88.17", {"center": v(223.52, -238) * mm, "radius": 0.87 * mm});
            skCircle(sketch, "E3.0.88.18", {"center": v(223.52, -252) * mm, "radius": 0.87 * mm});
            skSolve(sketch);
        }
        {
            var Q0;
            Q0=makeQuery(id+"F0.imprint","IMPRINT",FACE,{"disambiguationData":[TD([[makeQuery(id+"F0.imprint","IMPRINT",EDGE,{"derivedFrom":sQuery(id+"F0.wireOp",EDGE,"E0")}),-1.0]])]});
            extrude(context, id + "F1", {"entities" : qUnion([Q0]), "oppositeDirection" : true, "depth" : 1.52 * mm, "offsetDistance" : 25 * mm});
        }
        {
            var Q0;
            Q0 = qSketchRegion(id + "F0", true);
            extrude(context, id + "F2", {"entities" : qUnion([Q0]), "depth" : 12.5 * mm, "offsetDistance" : 25 * mm});
        }
        {
            var Q0;
            Q0=makeQuery(id+"F2.opExtrude","SWEPT_FACE",FACE,{"disambiguationData":[OSD([sQuery(id+"F0.wireOp",EDGE,"E2.bottom")])]});
            var sketch = newSketch(context, id + "F3", { "sketchPlane" : qUnion([Q0])});
            skLineSegment(sketch, "E4.bottom", {"start": v(-30, 12.5) * mm, "end": v(-10, 12.5) * mm});
            skLineSegment(sketch, "E4.top", {"start": v(-30, 0) * mm, "end": v(-10, 0) * mm});
            skLineSegment(sketch, "E4.left", {"start": v(-30, 12.5) * mm, "end": v(-30, 0) * mm});
            skLineSegment(sketch, "E4.right", {"start": v(-10, 12.5) * mm, "end": v(-10, 0) * mm});
            skSolve(sketch);
        }
        {
            var Q0;
            Q0 = qSketchRegion(id + "F3", true);
            extrude(context, id + "F4", {"entities" : qUnion([Q0]), "operationType" : NewBodyOperationType.REMOVE, "endBound" : BoundingType.THROUGH_ALL, "oppositeDirection" : true, "depth" : 25 * mm, "offsetDistance" : 25 * mm});
        }
        {
            var Q0;
            Q0=makeQuery(id+"F4.boolean.opBoolean","COPY",FACE,{"derivedFrom":makeQuery(id+"F4.opExtrude","SWEPT_FACE",FACE,{"disambiguationData":[OSD([sQuery(id+"F3.wireOp",EDGE,"E4.right")])]})});
            var sketch = newSketch(context, id + "F5", { "sketchPlane" : qUnion([Q0])});
            skLineSegment(sketch, "E5.bottom", {"start": v(2.5, 12.5) * mm, "end": v(11.5, 12.5) * mm});
            skLineSegment(sketch, "E5.top", {"start": v(2.5, 5) * mm, "end": v(11.5, 5) * mm});
            skLineSegment(sketch, "E5.left", {"start": v(2.5, 12.5) * mm, "end": v(2.5, 5) * mm});
            skLineSegment(sketch, "E5.right", {"start": v(11.5, 12.5) * mm, "end": v(11.5, 5) * mm});
            skLineSegment(sketch, "E6.1.0.0", {"start": v(16.5, 12.5) * mm, "end": v(16.5, 5) * mm});
            skLineSegment(sketch, "E6.1.0.1", {"start": v(16.5, 12.5) * mm, "end": v(25.5, 12.5) * mm});
            skLineSegment(sketch, "E6.1.0.2", {"start": v(25.5, 12.5) * mm, "end": v(25.5, 5) * mm});
            skLineSegment(sketch, "E6.1.0.3", {"start": v(16.5, 5) * mm, "end": v(25.5, 5) * mm});
            skLineSegment(sketch, "E6.2.0.0", {"start": v(30.5, 12.5) * mm, "end": v(30.5, 5) * mm});
            skLineSegment(sketch, "E6.2.0.1", {"start": v(30.5, 12.5) * mm, "end": v(39.5, 12.5) * mm});
            skLineSegment(sketch, "E6.2.0.2", {"start": v(39.5, 12.5) * mm, "end": v(39.5, 5) * mm});
            skLineSegment(sketch, "E6.2.0.3", {"start": v(30.5, 5) * mm, "end": v(39.5, 5) * mm});
            skLineSegment(sketch, "E6.3.0.0", {"start": v(44.5, 12.5) * mm, "end": v(44.5, 5) * mm});
            skLineSegment(sketch, "E6.3.0.1", {"start": v(44.5, 12.5) * mm, "end": v(53.5, 12.5) * mm});
            skLineSegment(sketch, "E6.3.0.2", {"start": v(53.5, 12.5) * mm, "end": v(53.5, 5) * mm});
            skLineSegment(sketch, "E6.3.0.3", {"start": v(44.5, 5) * mm, "end": v(53.5, 5) * mm});
            skLineSegment(sketch, "E6.4.0.0", {"start": v(58.5, 12.5) * mm, "end": v(58.5, 5) * mm});
            skLineSegment(sketch, "E6.4.0.1", {"start": v(58.5, 12.5) * mm, "end": v(67.5, 12.5) * mm});
            skLineSegment(sketch, "E6.4.0.2", {"start": v(67.5, 12.5) * mm, "end": v(67.5, 5) * mm});
            skLineSegment(sketch, "E6.4.0.3", {"start": v(58.5, 5) * mm, "end": v(67.5, 5) * mm});
            skLineSegment(sketch, "E6.5.0.0", {"start": v(72.5, 12.5) * mm, "end": v(72.5, 5) * mm});
            skLineSegment(sketch, "E6.5.0.1", {"start": v(72.5, 12.5) * mm, "end": v(81.5, 12.5) * mm});
            skLineSegment(sketch, "E6.5.0.2", {"start": v(81.5, 12.5) * mm, "end": v(81.5, 5) * mm});
            skLineSegment(sketch, "E6.5.0.3", {"start": v(72.5, 5) * mm, "end": v(81.5, 5) * mm});
            skLineSegment(sketch, "E6.6.0.0", {"start": v(86.5, 12.5) * mm, "end": v(86.5, 5) * mm});
            skLineSegment(sketch, "E6.6.0.1", {"start": v(86.5, 12.5) * mm, "end": v(95.5, 12.5) * mm});
            skLineSegment(sketch, "E6.6.0.2", {"start": v(95.5, 12.5) * mm, "end": v(95.5, 5) * mm});
            skLineSegment(sketch, "E6.6.0.3", {"start": v(86.5, 5) * mm, "end": v(95.5, 5) * mm});
            skLineSegment(sketch, "E6.7.0.0", {"start": v(100.5, 12.5) * mm, "end": v(100.5, 5) * mm});
            skLineSegment(sketch, "E6.7.0.1", {"start": v(100.5, 12.5) * mm, "end": v(109.5, 12.5) * mm});
            skLineSegment(sketch, "E6.7.0.2", {"start": v(109.5, 12.5) * mm, "end": v(109.5, 5) * mm});
            skLineSegment(sketch, "E6.7.0.3", {"start": v(100.5, 5) * mm, "end": v(109.5, 5) * mm});
            skLineSegment(sketch, "E6.8.0.0", {"start": v(114.5, 12.5) * mm, "end": v(114.5, 5) * mm});
            skLineSegment(sketch, "E6.8.0.1", {"start": v(114.5, 12.5) * mm, "end": v(123.5, 12.5) * mm});
            skLineSegment(sketch, "E6.8.0.2", {"start": v(123.5, 12.5) * mm, "end": v(123.5, 5) * mm});
            skLineSegment(sketch, "E6.8.0.3", {"start": v(114.5, 5) * mm, "end": v(123.5, 5) * mm});
            skLineSegment(sketch, "E6.9.0.0", {"start": v(128.5, 12.5) * mm, "end": v(128.5, 5) * mm});
            skLineSegment(sketch, "E6.9.0.1", {"start": v(128.5, 12.5) * mm, "end": v(137.5, 12.5) * mm});
            skLineSegment(sketch, "E6.9.0.2", {"start": v(137.5, 12.5) * mm, "end": v(137.5, 5) * mm});
            skLineSegment(sketch, "E6.9.0.3", {"start": v(128.5, 5) * mm, "end": v(137.5, 5) * mm});
            skLineSegment(sketch, "E6.10.0.0", {"start": v(142.5, 12.5) * mm, "end": v(142.5, 5) * mm});
            skLineSegment(sketch, "E6.10.0.1", {"start": v(142.5, 12.5) * mm, "end": v(151.5, 12.5) * mm});
            skLineSegment(sketch, "E6.10.0.2", {"start": v(151.5, 12.5) * mm, "end": v(151.5, 5) * mm});
            skLineSegment(sketch, "E6.10.0.3", {"start": v(142.5, 5) * mm, "end": v(151.5, 5) * mm});
            skLineSegment(sketch, "E6.11.0.0", {"start": v(156.5, 12.5) * mm, "end": v(156.5, 5) * mm});
            skLineSegment(sketch, "E6.11.0.1", {"start": v(156.5, 12.5) * mm, "end": v(165.5, 12.5) * mm});
            skLineSegment(sketch, "E6.11.0.2", {"start": v(165.5, 12.5) * mm, "end": v(165.5, 5) * mm});
            skLineSegment(sketch, "E6.11.0.3", {"start": v(156.5, 5) * mm, "end": v(165.5, 5) * mm});
            skLineSegment(sketch, "E6.12.0.0", {"start": v(170.5, 12.5) * mm, "end": v(170.5, 5) * mm});
            skLineSegment(sketch, "E6.12.0.1", {"start": v(170.5, 12.5) * mm, "end": v(179.5, 12.5) * mm});
            skLineSegment(sketch, "E6.12.0.2", {"start": v(179.5, 12.5) * mm, "end": v(179.5, 5) * mm});
            skLineSegment(sketch, "E6.12.0.3", {"start": v(170.5, 5) * mm, "end": v(179.5, 5) * mm});
            skLineSegment(sketch, "E6.13.0.0", {"start": v(184.5, 12.5) * mm, "end": v(184.5, 5) * mm});
            skLineSegment(sketch, "E6.13.0.1", {"start": v(184.5, 12.5) * mm, "end": v(193.5, 12.5) * mm});
            skLineSegment(sketch, "E6.13.0.2", {"start": v(193.5, 12.5) * mm, "end": v(193.5, 5) * mm});
            skLineSegment(sketch, "E6.13.0.3", {"start": v(184.5, 5) * mm, "end": v(193.5, 5) * mm});
            skLineSegment(sketch, "E6.14.0.0", {"start": v(198.5, 12.5) * mm, "end": v(198.5, 5) * mm});
            skLineSegment(sketch, "E6.14.0.1", {"start": v(198.5, 12.5) * mm, "end": v(207.5, 12.5) * mm});
            skLineSegment(sketch, "E6.14.0.2", {"start": v(207.5, 12.5) * mm, "end": v(207.5, 5) * mm});
            skLineSegment(sketch, "E6.14.0.3", {"start": v(198.5, 5) * mm, "end": v(207.5, 5) * mm});
            skLineSegment(sketch, "E6.15.0.0", {"start": v(212.5, 12.5) * mm, "end": v(212.5, 5) * mm});
            skLineSegment(sketch, "E6.15.0.1", {"start": v(212.5, 12.5) * mm, "end": v(221.5, 12.5) * mm});
            skLineSegment(sketch, "E6.15.0.2", {"start": v(221.5, 12.5) * mm, "end": v(221.5, 5) * mm});
            skLineSegment(sketch, "E6.15.0.3", {"start": v(212.5, 5) * mm, "end": v(221.5, 5) * mm});
            skLineSegment(sketch, "E6.16.0.0", {"start": v(226.5, 12.5) * mm, "end": v(226.5, 5) * mm});
            skLineSegment(sketch, "E6.16.0.1", {"start": v(226.5, 12.5) * mm, "end": v(235.5, 12.5) * mm});
            skLineSegment(sketch, "E6.16.0.2", {"start": v(235.5, 12.5) * mm, "end": v(235.5, 5) * mm});
            skLineSegment(sketch, "E6.16.0.3", {"start": v(226.5, 5) * mm, "end": v(235.5, 5) * mm});
            skLineSegment(sketch, "E6.17.0.0", {"start": v(240.5, 12.5) * mm, "end": v(240.5, 5) * mm});
            skLineSegment(sketch, "E6.17.0.1", {"start": v(240.5, 12.5) * mm, "end": v(249.5, 12.5) * mm});
            skLineSegment(sketch, "E6.17.0.2", {"start": v(249.5, 12.5) * mm, "end": v(249.5, 5) * mm});
            skLineSegment(sketch, "E6.17.0.3", {"start": v(240.5, 5) * mm, "end": v(249.5, 5) * mm});
            skLineSegment(sketch, "E6.18.0.0", {"start": v(254.5, 12.5) * mm, "end": v(254.5, 5) * mm});
            skLineSegment(sketch, "E6.18.0.1", {"start": v(254.5, 12.5) * mm, "end": v(263.5, 12.5) * mm});
            skLineSegment(sketch, "E6.18.0.2", {"start": v(263.5, 12.5) * mm, "end": v(263.5, 5) * mm});
            skLineSegment(sketch, "E6.18.0.3", {"start": v(254.5, 5) * mm, "end": v(263.5, 5) * mm});
            skLineSegment(sketch, "E6.direction1", {"start": v(2.5, 5) * mm, "end": v(16.5, 5) * mm, "construction": true});
            skSolve(sketch);
        }
        {
            var Q0;
            Q0 = qSketchRegion(id + "F5", true);
            extrude(context, id + "F6", {"entities" : qUnion([Q0]), "operationType" : NewBodyOperationType.REMOVE, "endBound" : BoundingType.THROUGH_ALL, "oppositeDirection" : true, "depth" : 25 * mm, "offsetDistance" : 25 * mm});
        }
        {
            var Q0;
            Q0=makeQuery(id+"F2.opExtrude","SWEPT_FACE",FACE,{"disambiguationData":[OSD([sQuery(id+"F0.wireOp",EDGE,"E2.bottom")])]});
            var sketch = newSketch(context, id + "F7", { "sketchPlane" : qUnion([Q0])});
            skLineSegment(sketch, "E7.bottom", {"start": v(-1.27, 12.5) * mm, "end": v(-3.81, 12.5) * mm});
            skLineSegment(sketch, "E7.top", {"start": v(-1.27, 5) * mm, "end": v(-3.8, 5) * mm});
            skLineSegment(sketch, "E7.left", {"start": v(-1.27, 12.5) * mm, "end": v(-1.27, 5) * mm});
            skLineSegment(sketch, "E7.right", {"start": v(-3.81, 12.5) * mm, "end": v(-3.81, 5) * mm});
            skLineSegment(sketch, "E8.1.0.0", {"start": v(11.43, 12.5) * mm, "end": v(11.43, 5) * mm});
            skLineSegment(sketch, "E8.1.0.1", {"start": v(13.97, 12.5) * mm, "end": v(11.43, 12.5) * mm});
            skLineSegment(sketch, "E8.1.0.2", {"start": v(13.97, 12.5) * mm, "end": v(13.97, 5) * mm});
            skLineSegment(sketch, "E8.1.0.3", {"start": v(13.97, 5) * mm, "end": v(11.43, 5) * mm});
            skLineSegment(sketch, "E8.2.0.0", {"start": v(26.67, 12.5) * mm, "end": v(26.67, 5) * mm});
            skLineSegment(sketch, "E8.2.0.1", {"start": v(29.2, 12.5) * mm, "end": v(26.67, 12.5) * mm});
            skLineSegment(sketch, "E8.2.0.2", {"start": v(29.21, 12.5) * mm, "end": v(29.21, 5) * mm});
            skLineSegment(sketch, "E8.2.0.3", {"start": v(29.21, 5) * mm, "end": v(26.67, 5) * mm});
            skLineSegment(sketch, "E8.3.0.0", {"start": v(41.9, 12.5) * mm, "end": v(41.9, 5) * mm});
            skLineSegment(sketch, "E8.3.0.1", {"start": v(44.45, 12.5) * mm, "end": v(41.9, 12.5) * mm});
            skLineSegment(sketch, "E8.3.0.2", {"start": v(44.45, 12.5) * mm, "end": v(44.45, 5) * mm});
            skLineSegment(sketch, "E8.3.0.3", {"start": v(44.45, 5) * mm, "end": v(41.9, 5) * mm});
            skLineSegment(sketch, "E8.4.0.0", {"start": v(57.15, 12.5) * mm, "end": v(57.15, 5) * mm});
            skLineSegment(sketch, "E8.4.0.1", {"start": v(59.69, 12.5) * mm, "end": v(57.15, 12.5) * mm});
            skLineSegment(sketch, "E8.4.0.2", {"start": v(59.69, 12.5) * mm, "end": v(59.69, 5) * mm});
            skLineSegment(sketch, "E8.4.0.3", {"start": v(59.69, 5) * mm, "end": v(57.15, 5) * mm});
            skLineSegment(sketch, "E8.5.0.0", {"start": v(72.39, 12.5) * mm, "end": v(72.39, 5) * mm});
            skLineSegment(sketch, "E8.5.0.1", {"start": v(74.93, 12.5) * mm, "end": v(72.39, 12.5) * mm});
            skLineSegment(sketch, "E8.5.0.2", {"start": v(74.93, 12.5) * mm, "end": v(74.93, 5) * mm});
            skLineSegment(sketch, "E8.5.0.3", {"start": v(74.93, 5) * mm, "end": v(72.4, 5) * mm});
            skLineSegment(sketch, "E8.6.0.0", {"start": v(87.63, 12.5) * mm, "end": v(87.63, 5) * mm});
            skLineSegment(sketch, "E8.6.0.1", {"start": v(90.17, 12.5) * mm, "end": v(87.63, 12.5) * mm});
            skLineSegment(sketch, "E8.6.0.2", {"start": v(90.17, 12.5) * mm, "end": v(90.17, 5) * mm});
            skLineSegment(sketch, "E8.6.0.3", {"start": v(90.17, 5) * mm, "end": v(87.63, 5) * mm});
            skLineSegment(sketch, "E8.7.0.0", {"start": v(102.87, 12.5) * mm, "end": v(102.87, 5) * mm});
            skLineSegment(sketch, "E8.7.0.1", {"start": v(105.4, 12.5) * mm, "end": v(102.87, 12.5) * mm});
            skLineSegment(sketch, "E8.7.0.2", {"start": v(105.4, 12.5) * mm, "end": v(105.4, 5) * mm});
            skLineSegment(sketch, "E8.7.0.3", {"start": v(105.4, 5) * mm, "end": v(102.87, 5) * mm});
            skLineSegment(sketch, "E8.8.0.0", {"start": v(118.11, 12.5) * mm, "end": v(118.11, 5) * mm});
            skLineSegment(sketch, "E8.8.0.1", {"start": v(120.65, 12.5) * mm, "end": v(118.11, 12.5) * mm});
            skLineSegment(sketch, "E8.8.0.2", {"start": v(120.65, 12.5) * mm, "end": v(120.65, 5) * mm});
            skLineSegment(sketch, "E8.8.0.3", {"start": v(120.65, 5) * mm, "end": v(118.11, 5) * mm});
            skLineSegment(sketch, "E8.direction1", {"start": v(-3.8, 5) * mm, "end": v(11.43, 5) * mm, "construction": true});
            skLineSegment(sketch, "E9.0.9.0", {"start": v(133.35, 12.5) * mm, "end": v(133.35, 5) * mm});
            skLineSegment(sketch, "E9.3.9.0", {"start": v(135.9, 12.5) * mm, "end": v(133.35, 12.5) * mm});
            skLineSegment(sketch, "E9.6.9.0", {"start": v(135.9, 12.5) * mm, "end": v(135.9, 5) * mm});
            skLineSegment(sketch, "E9.9.9.0", {"start": v(135.9, 5) * mm, "end": v(133.35, 5) * mm});
            skLineSegment(sketch, "E9.0.10.0", {"start": v(148.6, 12.5) * mm, "end": v(148.6, 5) * mm});
            skLineSegment(sketch, "E9.3.10.0", {"start": v(151.13, 12.5) * mm, "end": v(148.6, 12.5) * mm});
            skLineSegment(sketch, "E9.6.10.0", {"start": v(151.13, 12.5) * mm, "end": v(151.13, 5) * mm});
            skLineSegment(sketch, "E9.9.10.0", {"start": v(151.13, 5) * mm, "end": v(148.6, 5) * mm});
            skLineSegment(sketch, "E9.0.11.0", {"start": v(163.83, 12.5) * mm, "end": v(163.83, 5) * mm});
            skLineSegment(sketch, "E9.3.11.0", {"start": v(166.37, 12.5) * mm, "end": v(163.83, 12.5) * mm});
            skLineSegment(sketch, "E9.6.11.0", {"start": v(166.37, 12.5) * mm, "end": v(166.37, 5) * mm});
            skLineSegment(sketch, "E9.9.11.0", {"start": v(166.37, 5) * mm, "end": v(163.83, 5) * mm});
            skLineSegment(sketch, "E9.0.12.0", {"start": v(179.07, 12.5) * mm, "end": v(179.07, 5) * mm});
            skLineSegment(sketch, "E9.3.12.0", {"start": v(181.6, 12.5) * mm, "end": v(179.07, 12.5) * mm});
            skLineSegment(sketch, "E9.6.12.0", {"start": v(181.6, 12.5) * mm, "end": v(181.6, 5) * mm});
            skLineSegment(sketch, "E9.9.12.0", {"start": v(181.6, 5) * mm, "end": v(179.07, 5) * mm});
            skLineSegment(sketch, "E9.0.13.0", {"start": v(194.3, 12.5) * mm, "end": v(194.3, 5) * mm});
            skLineSegment(sketch, "E9.3.13.0", {"start": v(196.85, 12.5) * mm, "end": v(194.3, 12.5) * mm});
            skLineSegment(sketch, "E9.6.13.0", {"start": v(196.85, 12.5) * mm, "end": v(196.85, 5) * mm});
            skLineSegment(sketch, "E9.9.13.0", {"start": v(196.85, 5) * mm, "end": v(194.3, 5) * mm});
            skLineSegment(sketch, "E9.0.14.0", {"start": v(209.55, 12.5) * mm, "end": v(209.55, 5) * mm});
            skLineSegment(sketch, "E9.3.14.0", {"start": v(212.1, 12.5) * mm, "end": v(209.55, 12.5) * mm});
            skLineSegment(sketch, "E9.6.14.0", {"start": v(212.1, 12.5) * mm, "end": v(212.1, 5) * mm});
            skLineSegment(sketch, "E9.9.14.0", {"start": v(212.1, 5) * mm, "end": v(209.55, 5) * mm});
            skLineSegment(sketch, "E10.0.15.0", {"start": v(224.8, 12.5) * mm, "end": v(224.8, 5) * mm});
            skLineSegment(sketch, "E10.3.15.0", {"start": v(227.33, 12.5) * mm, "end": v(224.8, 12.5) * mm});
            skLineSegment(sketch, "E10.6.15.0", {"start": v(227.33, 12.5) * mm, "end": v(227.33, 5) * mm});
            skLineSegment(sketch, "E10.9.15.0", {"start": v(227.33, 5) * mm, "end": v(224.8, 5) * mm});
            skLineSegment(sketch, "E11.bottom", {"start": v(293.44, 12.5) * mm, "end": v(233.44, 12.5) * mm});
            skLineSegment(sketch, "E11.top", {"start": v(293.44, 0) * mm, "end": v(233.44, 0) * mm});
            skLineSegment(sketch, "E11.left", {"start": v(293.44, 12.5) * mm, "end": v(293.44, 0) * mm});
            skLineSegment(sketch, "E11.right", {"start": v(233.44, 12.5) * mm, "end": v(233.44, 0) * mm});
            skSolve(sketch);
        }
        {
            var Q0;
            Q0 = qSketchRegion(id + "F7", true);
            extrude(context, id + "F8", {"entities" : qUnion([Q0]), "operationType" : NewBodyOperationType.REMOVE, "endBound" : BoundingType.THROUGH_ALL, "oppositeDirection" : true, "depth" : 25 * mm, "offsetDistance" : 25 * mm});
        }
        {
            var Q0;
            {var subQ0=sQuery(id+"F0.wireOp",EDGE,"E2.top");var subQ2=makeQuery(id+"F4.boolean.opBoolean","COPY",FACE,{"derivedFrom":makeQuery(id+"F4.opExtrude","SWEPT_FACE",FACE,{"disambiguationData":[OSD([sQuery(id+"F3.wireOp",EDGE,"E4.right")])]})});var subQ4=sQuery(id+"F0.wireOp",EDGE,"E1.45.0.0");var subQ5=sQuery(id+"F0.wireOp",EDGE,"E1.44.0.0");var subQ6=sQuery(id+"F0.wireOp",EDGE,"E1.43.0.0");var subQ7=sQuery(id+"F0.wireOp",EDGE,"E1.42.0.0");var subQ8=sQuery(id+"F0.wireOp",EDGE,"E1.41.0.0");var subQ9=sQuery(id+"F0.wireOp",EDGE,"E1.40.0.0");var subQ10=sQuery(id+"F0.wireOp",EDGE,"E1.39.0.0");var subQ11=sQuery(id+"F0.wireOp",EDGE,"E1.38.0.0");var subQ12=sQuery(id+"F0.wireOp",EDGE,"E1.36.0.0");var subQ13=sQuery(id+"F0.wireOp",EDGE,"E1.35.0.0");var subQ14=sQuery(id+"F0.wireOp",EDGE,"E1.34.0.0");var subQ15=sQuery(id+"F0.wireOp",EDGE,"E1.33.0.0");var subQ16=sQuery(id+"F0.wireOp",EDGE,"E1.32.0.0");var subQ17=sQuery(id+"F0.wireOp",EDGE,"E1.31.0.0");var subQ18=sQuery(id+"F0.wireOp",EDGE,"E1.30.0.0");var subQ19=sQuery(id+"F0.wireOp",EDGE,"E2.right");var subQ20=sQuery(id+"F0.wireOp",EDGE,"E1.29.0.0");var subQ21=sQuery(id+"F0.wireOp",EDGE,"E1.28.0.0");var subQ22=sQuery(id+"F0.wireOp",EDGE,"E1.27.0.0");var subQ23=sQuery(id+"F0.wireOp",EDGE,"E1.26.0.0");var subQ24=sQuery(id+"F0.wireOp",EDGE,"E1.25.0.0");var subQ25=sQuery(id+"F0.wireOp",EDGE,"E1.24.0.0");var subQ26=sQuery(id+"F0.wireOp",EDGE,"E1.23.0.0");var subQ27=sQuery(id+"F0.wireOp",EDGE,"E1.22.0.0");var subQ28=sQuery(id+"F0.wireOp",EDGE,"E1.9.0.0");var subQ29=sQuery(id+"F0.wireOp",EDGE,"E1.7.0.0");var subQ30=sQuery(id+"F0.wireOp",EDGE,"E1.6.0.0");var subQ31=sQuery(id+"F0.wireOp",EDGE,"E1.5.0.0");var subQ32=sQuery(id+"F0.wireOp",EDGE,"E0");var subQ33=sQuery(id+"F0.wireOp",EDGE,"E1.4.0.0");var subQ34=sQuery(id+"F0.wireOp",EDGE,"E1.8.0.0");var subQ35=sQuery(id+"F0.wireOp",EDGE,"E1.37.0.0");var subQ36=sQuery(id+"F0.wireOp",EDGE,"E1.12.0.0");var subQ37=sQuery(id+"F0.wireOp",EDGE,"E1.2.0.0");var subQ38=sQuery(id+"F0.wireOp",EDGE,"E1.1.0.0");var subQ39=sQuery(id+"F0.wireOp",EDGE,"E1.3.0.0");var subQ40=sQuery(id+"F0.wireOp",EDGE,"E1.10.0.0");var subQ41=sQuery(id+"F0.wireOp",EDGE,"E1.11.0.0");var subQ42=sQuery(id+"F0.wireOp",EDGE,"E1.13.0.0");var subQ43=sQuery(id+"F0.wireOp",EDGE,"E1.14.0.0");var subQ44=sQuery(id+"F0.wireOp",EDGE,"E1.15.0.0");var subQ45=sQuery(id+"F0.wireOp",EDGE,"E1.16.0.0");var subQ46=sQuery(id+"F0.wireOp",EDGE,"E1.17.0.0");var subQ47=sQuery(id+"F0.wireOp",EDGE,"E1.18.0.0");var subQ48=sQuery(id+"F0.wireOp",EDGE,"E1.19.0.0");var subQ49=sQuery(id+"F0.wireOp",EDGE,"E1.20.0.0");var subQ50=sQuery(id+"F0.wireOp",EDGE,"E1.21.0.0");var subQ51=sQuery(id+"F0.wireOp",EDGE,"E1.46.0.0");var subQ52=sQuery(id+"F0.wireOp",EDGE,"E1.47.0.0");var subQ53=sQuery(id+"F0.wireOp",EDGE,"E1.48.0.0");var subQ54=sQuery(id+"F0.wireOp",EDGE,"E1.49.0.0");var subQ55=sQuery(id+"F0.wireOp",EDGE,"E1.50.0.0");var subQ56=sQuery(id+"F0.wireOp",EDGE,"E1.51.0.0");var subQ57=sQuery(id+"F0.wireOp",EDGE,"E1.52.0.0");var subQ58=sQuery(id+"F0.wireOp",EDGE,"E1.53.0.0");var subQ59=sQuery(id+"F0.wireOp",EDGE,"E1.54.0.0");var subQ60=sQuery(id+"F0.wireOp",EDGE,"E1.55.0.0");var subQ61=sQuery(id+"F0.wireOp",EDGE,"E1.56.0.0");var subQ62=sQuery(id+"F0.wireOp",EDGE,"E1.57.0.0");var subQ63=sQuery(id+"F0.wireOp",EDGE,"E1.58.0.0");var subQ64=sQuery(id+"F0.wireOp",EDGE,"E1.59.0.0");var subQ65=sQuery(id+"F0.wireOp",EDGE,"E1.60.0.0");var subQ66=sQuery(id+"F0.wireOp",EDGE,"E1.61.0.0");var subQ67=sQuery(id+"F0.wireOp",EDGE,"E1.62.0.0");var subQ68=sQuery(id+"F0.wireOp",EDGE,"E1.63.0.0");var subQ69=sQuery(id+"F0.wireOp",EDGE,"E1.64.0.0");var subQ70=sQuery(id+"F0.wireOp",EDGE,"E1.65.0.0");var subQ71=sQuery(id+"F0.wireOp",EDGE,"E1.66.0.0");var subQ72=sQuery(id+"F0.wireOp",EDGE,"E1.67.0.0");var subQ73=sQuery(id+"F0.wireOp",EDGE,"E1.68.0.0");var subQ74=sQuery(id+"F0.wireOp",EDGE,"E1.69.0.0");var subQ75=sQuery(id+"F0.wireOp",EDGE,"E1.70.0.0");var subQ76=sQuery(id+"F0.wireOp",EDGE,"E1.71.0.0");var subQ77=sQuery(id+"F0.wireOp",EDGE,"E1.72.0.0");var subQ78=sQuery(id+"F0.wireOp",EDGE,"E1.73.0.0");var subQ79=sQuery(id+"F0.wireOp",EDGE,"E1.74.0.0");var subQ80=sQuery(id+"F0.wireOp",EDGE,"E1.75.0.0");var subQ81=sQuery(id+"F0.wireOp",EDGE,"E1.76.0.0");var subQ82=sQuery(id+"F0.wireOp",EDGE,"E3.0.86.0");var subQ83=sQuery(id+"F0.wireOp",EDGE,"E1.77.0.0");var subQ84=sQuery(id+"F0.wireOp",EDGE,"E3.0.87.0");var subQ85=sQuery(id+"F0.wireOp",EDGE,"E1.78.0.0");var subQ86=sQuery(id+"F0.wireOp",EDGE,"E3.0.88.0");var subQ87=sQuery(id+"F0.wireOp",EDGE,"E1.79.0.0");var subQ88=sQuery(id+"F0.wireOp",EDGE,"E1.80.0.0");var subQ89=sQuery(id+"F0.wireOp",EDGE,"E1.81.0.0");var subQ90=sQuery(id+"F0.wireOp",EDGE,"E1.82.0.0");var subQ91=sQuery(id+"F0.wireOp",EDGE,"E1.83.0.0");var subQ92=sQuery(id+"F0.wireOp",EDGE,"E1.84.0.0");var subQ93=sQuery(id+"F0.wireOp",EDGE,"E1.85.0.0");Q0=makeQuery(id+"F8.boolean.opBoolean","SPLIT",FACE,{"disambiguationData":[TD([subQ2])],"derivedFrom":makeQuery(id+"F6.boolean.opBoolean","SPLIT",FACE,{"disambiguationData":[TD([makeQuery(id+"F2.opExtrude","SWEPT_FACE",FACE,{"disambiguationData":[OSD([subQ32])]})])],"derivedFrom":makeQuery(id+"F2.opExtrude","CAP_FACE",FACE,{"disambiguationData":[OSD([subQ32,sQuery(id+"F0.wireOp",EDGE,"E1.0.1.0"),sQuery(id+"F0.wireOp",EDGE,"E1.0.2.0"),sQuery(id+"F0.wireOp",EDGE,"E1.0.3.0"),sQuery(id+"F0.wireOp",EDGE,"E1.0.4.0"),sQuery(id+"F0.wireOp",EDGE,"E1.0.5.0"),sQuery(id+"F0.wireOp",EDGE,"E1.0.6.0"),sQuery(id+"F0.wireOp",EDGE,"E1.0.7.0"),sQuery(id+"F0.wireOp",EDGE,"E1.0.8.0"),sQuery(id+"F0.wireOp",EDGE,"E1.0.9.0"),sQuery(id+"F0.wireOp",EDGE,"E1.0.10.0"),sQuery(id+"F0.wireOp",EDGE,"E1.0.11.0"),sQuery(id+"F0.wireOp",EDGE,"E1.0.12.0"),sQuery(id+"F0.wireOp",EDGE,"E1.0.13.0"),sQuery(id+"F0.wireOp",EDGE,"E1.0.14.0"),sQuery(id+"F0.wireOp",EDGE,"E1.0.15.0"),sQuery(id+"F0.wireOp",EDGE,"E1.0.16.0"),sQuery(id+"F0.wireOp",EDGE,"E1.0.17.0"),sQuery(id+"F0.wireOp",EDGE,"E1.0.18.0"),subQ38,sQuery(id+"F0.wireOp",EDGE,"E1.1.1.0"),sQuery(id+"F0.wireOp",EDGE,"E1.1.2.0"),sQuery(id+"F0.wireOp",EDGE,"E1.1.3.0"),sQuery(id+"F0.wireOp",EDGE,"E1.1.4.0"),sQuery(id+"F0.wireOp",EDGE,"E1.1.5.0"),sQuery(id+"F0.wireOp",EDGE,"E1.1.6.0"),sQuery(id+"F0.wireOp",EDGE,"E1.1.7.0"),sQuery(id+"F0.wireOp",EDGE,"E1.1.8.0"),sQuery(id+"F0.wireOp",EDGE,"E1.1.9.0"),sQuery(id+"F0.wireOp",EDGE,"E1.1.10.0"),sQuery(id+"F0.wireOp",EDGE,"E1.1.11.0"),sQuery(id+"F0.wireOp",EDGE,"E1.1.12.0"),sQuery(id+"F0.wireOp",EDGE,"E1.1.13.0"),sQuery(id+"F0.wireOp",EDGE,"E1.1.14.0"),sQuery(id+"F0.wireOp",EDGE,"E1.1.15.0"),sQuery(id+"F0.wireOp",EDGE,"E1.1.16.0"),sQuery(id+"F0.wireOp",EDGE,"E1.1.17.0"),sQuery(id+"F0.wireOp",EDGE,"E1.1.18.0"),subQ37,sQuery(id+"F0.wireOp",EDGE,"E1.2.1.0"),sQuery(id+"F0.wireOp",EDGE,"E1.2.2.0"),sQuery(id+"F0.wireOp",EDGE,"E1.2.3.0"),sQuery(id+"F0.wireOp",EDGE,"E1.2.4.0"),sQuery(id+"F0.wireOp",EDGE,"E1.2.5.0"),sQuery(id+"F0.wireOp",EDGE,"E1.2.6.0"),sQuery(id+"F0.wireOp",EDGE,"E1.2.7.0"),sQuery(id+"F0.wireOp",EDGE,"E1.2.8.0"),sQuery(id+"F0.wireOp",EDGE,"E1.2.9.0"),sQuery(id+"F0.wireOp",EDGE,"E1.2.10.0"),sQuery(id+"F0.wireOp",EDGE,"E1.2.11.0"),sQuery(id+"F0.wireOp",EDGE,"E1.2.12.0"),sQuery(id+"F0.wireOp",EDGE,"E1.2.13.0"),sQuery(id+"F0.wireOp",EDGE,"E1.2.14.0"),sQuery(id+"F0.wireOp",EDGE,"E1.2.15.0"),sQuery(id+"F0.wireOp",EDGE,"E1.2.16.0"),sQuery(id+"F0.wireOp",EDGE,"E1.2.17.0"),sQuery(id+"F0.wireOp",EDGE,"E1.2.18.0"),subQ39,sQuery(id+"F0.wireOp",EDGE,"E1.3.1.0"),sQuery(id+"F0.wireOp",EDGE,"E1.3.2.0"),sQuery(id+"F0.wireOp",EDGE,"E1.3.3.0"),sQuery(id+"F0.wireOp",EDGE,"E1.3.4.0"),sQuery(id+"F0.wireOp",EDGE,"E1.3.5.0"),sQuery(id+"F0.wireOp",EDGE,"E1.3.6.0"),sQuery(id+"F0.wireOp",EDGE,"E1.3.7.0"),sQuery(id+"F0.wireOp",EDGE,"E1.3.8.0"),sQuery(id+"F0.wireOp",EDGE,"E1.3.9.0"),sQuery(id+"F0.wireOp",EDGE,"E1.3.10.0"),sQuery(id+"F0.wireOp",EDGE,"E1.3.11.0"),sQuery(id+"F0.wireOp",EDGE,"E1.3.12.0"),sQuery(id+"F0.wireOp",EDGE,"E1.3.13.0"),sQuery(id+"F0.wireOp",EDGE,"E1.3.14.0"),sQuery(id+"F0.wireOp",EDGE,"E1.3.15.0"),sQuery(id+"F0.wireOp",EDGE,"E1.3.16.0"),sQuery(id+"F0.wireOp",EDGE,"E1.3.17.0"),sQuery(id+"F0.wireOp",EDGE,"E1.3.18.0"),subQ33,sQuery(id+"F0.wireOp",EDGE,"E1.4.1.0"),sQuery(id+"F0.wireOp",EDGE,"E1.4.2.0"),sQuery(id+"F0.wireOp",EDGE,"E1.4.3.0"),sQuery(id+"F0.wireOp",EDGE,"E1.4.4.0"),sQuery(id+"F0.wireOp",EDGE,"E1.4.5.0"),sQuery(id+"F0.wireOp",EDGE,"E1.4.6.0"),sQuery(id+"F0.wireOp",EDGE,"E1.4.7.0"),sQuery(id+"F0.wireOp",EDGE,"E1.4.8.0"),sQuery(id+"F0.wireOp",EDGE,"E1.4.9.0"),sQuery(id+"F0.wireOp",EDGE,"E1.4.10.0"),sQuery(id+"F0.wireOp",EDGE,"E1.4.11.0"),sQuery(id+"F0.wireOp",EDGE,"E1.4.12.0"),sQuery(id+"F0.wireOp",EDGE,"E1.4.13.0"),sQuery(id+"F0.wireOp",EDGE,"E1.4.14.0"),sQuery(id+"F0.wireOp",EDGE,"E1.4.15.0"),sQuery(id+"F0.wireOp",EDGE,"E1.4.16.0"),sQuery(id+"F0.wireOp",EDGE,"E1.4.17.0"),sQuery(id+"F0.wireOp",EDGE,"E1.4.18.0"),subQ31,sQuery(id+"F0.wireOp",EDGE,"E1.5.1.0"),sQuery(id+"F0.wireOp",EDGE,"E1.5.2.0"),sQuery(id+"F0.wireOp",EDGE,"E1.5.3.0"),sQuery(id+"F0.wireOp",EDGE,"E1.5.4.0"),sQuery(id+"F0.wireOp",EDGE,"E1.5.5.0"),sQuery(id+"F0.wireOp",EDGE,"E1.5.6.0"),sQuery(id+"F0.wireOp",EDGE,"E1.5.7.0"),sQuery(id+"F0.wireOp",EDGE,"E1.5.8.0"),sQuery(id+"F0.wireOp",EDGE,"E1.5.9.0"),sQuery(id+"F0.wireOp",EDGE,"E1.5.10.0"),sQuery(id+"F0.wireOp",EDGE,"E1.5.11.0"),sQuery(id+"F0.wireOp",EDGE,"E1.5.12.0"),sQuery(id+"F0.wireOp",EDGE,"E1.5.13.0"),sQuery(id+"F0.wireOp",EDGE,"E1.5.14.0"),sQuery(id+"F0.wireOp",EDGE,"E1.5.15.0"),sQuery(id+"F0.wireOp",EDGE,"E1.5.16.0"),sQuery(id+"F0.wireOp",EDGE,"E1.5.17.0"),sQuery(id+"F0.wireOp",EDGE,"E1.5.18.0"),subQ30,sQuery(id+"F0.wireOp",EDGE,"E1.6.1.0"),sQuery(id+"F0.wireOp",EDGE,"E1.6.2.0"),sQuery(id+"F0.wireOp",EDGE,"E1.6.3.0"),sQuery(id+"F0.wireOp",EDGE,"E1.6.4.0"),sQuery(id+"F0.wireOp",EDGE,"E1.6.5.0"),sQuery(id+"F0.wireOp",EDGE,"E1.6.6.0"),sQuery(id+"F0.wireOp",EDGE,"E1.6.7.0"),sQuery(id+"F0.wireOp",EDGE,"E1.6.8.0"),sQuery(id+"F0.wireOp",EDGE,"E1.6.9.0"),sQuery(id+"F0.wireOp",EDGE,"E1.6.10.0"),sQuery(id+"F0.wireOp",EDGE,"E1.6.11.0"),sQuery(id+"F0.wireOp",EDGE,"E1.6.12.0"),sQuery(id+"F0.wireOp",EDGE,"E1.6.13.0"),sQuery(id+"F0.wireOp",EDGE,"E1.6.14.0"),sQuery(id+"F0.wireOp",EDGE,"E1.6.15.0"),sQuery(id+"F0.wireOp",EDGE,"E1.6.16.0"),sQuery(id+"F0.wireOp",EDGE,"E1.6.17.0"),sQuery(id+"F0.wireOp",EDGE,"E1.6.18.0"),subQ29,sQuery(id+"F0.wireOp",EDGE,"E1.7.1.0"),sQuery(id+"F0.wireOp",EDGE,"E1.7.2.0"),sQuery(id+"F0.wireOp",EDGE,"E1.7.3.0"),sQuery(id+"F0.wireOp",EDGE,"E1.7.4.0"),sQuery(id+"F0.wireOp",EDGE,"E1.7.5.0"),sQuery(id+"F0.wireOp",EDGE,"E1.7.6.0"),sQuery(id+"F0.wireOp",EDGE,"E1.7.7.0"),sQuery(id+"F0.wireOp",EDGE,"E1.7.8.0"),sQuery(id+"F0.wireOp",EDGE,"E1.7.9.0"),sQuery(id+"F0.wireOp",EDGE,"E1.7.10.0"),sQuery(id+"F0.wireOp",EDGE,"E1.7.11.0"),sQuery(id+"F0.wireOp",EDGE,"E1.7.12.0"),sQuery(id+"F0.wireOp",EDGE,"E1.7.13.0"),sQuery(id+"F0.wireOp",EDGE,"E1.7.14.0"),sQuery(id+"F0.wireOp",EDGE,"E1.7.15.0"),sQuery(id+"F0.wireOp",EDGE,"E1.7.16.0"),sQuery(id+"F0.wireOp",EDGE,"E1.7.17.0"),sQuery(id+"F0.wireOp",EDGE,"E1.7.18.0"),subQ34,sQuery(id+"F0.wireOp",EDGE,"E1.8.1.0"),sQuery(id+"F0.wireOp",EDGE,"E1.8.2.0"),sQuery(id+"F0.wireOp",EDGE,"E1.8.3.0"),sQuery(id+"F0.wireOp",EDGE,"E1.8.4.0"),sQuery(id+"F0.wireOp",EDGE,"E1.8.5.0"),sQuery(id+"F0.wireOp",EDGE,"E1.8.6.0"),sQuery(id+"F0.wireOp",EDGE,"E1.8.7.0"),sQuery(id+"F0.wireOp",EDGE,"E1.8.8.0"),sQuery(id+"F0.wireOp",EDGE,"E1.8.9.0"),sQuery(id+"F0.wireOp",EDGE,"E1.8.10.0"),sQuery(id+"F0.wireOp",EDGE,"E1.8.11.0"),sQuery(id+"F0.wireOp",EDGE,"E1.8.12.0"),sQuery(id+"F0.wireOp",EDGE,"E1.8.13.0"),sQuery(id+"F0.wireOp",EDGE,"E1.8.14.0"),sQuery(id+"F0.wireOp",EDGE,"E1.8.15.0"),sQuery(id+"F0.wireOp",EDGE,"E1.8.16.0"),sQuery(id+"F0.wireOp",EDGE,"E1.8.17.0"),sQuery(id+"F0.wireOp",EDGE,"E1.8.18.0"),subQ28,sQuery(id+"F0.wireOp",EDGE,"E1.9.1.0"),sQuery(id+"F0.wireOp",EDGE,"E1.9.2.0"),sQuery(id+"F0.wireOp",EDGE,"E1.9.3.0"),sQuery(id+"F0.wireOp",EDGE,"E1.9.4.0"),sQuery(id+"F0.wireOp",EDGE,"E1.9.5.0"),sQuery(id+"F0.wireOp",EDGE,"E1.9.6.0"),sQuery(id+"F0.wireOp",EDGE,"E1.9.7.0"),sQuery(id+"F0.wireOp",EDGE,"E1.9.8.0"),sQuery(id+"F0.wireOp",EDGE,"E1.9.9.0"),sQuery(id+"F0.wireOp",EDGE,"E1.9.10.0"),sQuery(id+"F0.wireOp",EDGE,"E1.9.11.0"),sQuery(id+"F0.wireOp",EDGE,"E1.9.12.0"),sQuery(id+"F0.wireOp",EDGE,"E1.9.13.0"),sQuery(id+"F0.wireOp",EDGE,"E1.9.14.0"),sQuery(id+"F0.wireOp",EDGE,"E1.9.15.0"),sQuery(id+"F0.wireOp",EDGE,"E1.9.16.0"),sQuery(id+"F0.wireOp",EDGE,"E1.9.17.0"),sQuery(id+"F0.wireOp",EDGE,"E1.9.18.0"),subQ40,sQuery(id+"F0.wireOp",EDGE,"E1.10.1.0"),sQuery(id+"F0.wireOp",EDGE,"E1.10.2.0"),sQuery(id+"F0.wireOp",EDGE,"E1.10.3.0"),sQuery(id+"F0.wireOp",EDGE,"E1.10.4.0"),sQuery(id+"F0.wireOp",EDGE,"E1.10.5.0"),sQuery(id+"F0.wireOp",EDGE,"E1.10.6.0"),sQuery(id+"F0.wireOp",EDGE,"E1.10.7.0"),sQuery(id+"F0.wireOp",EDGE,"E1.10.8.0"),sQuery(id+"F0.wireOp",EDGE,"E1.10.9.0"),sQuery(id+"F0.wireOp",EDGE,"E1.10.10.0"),sQuery(id+"F0.wireOp",EDGE,"E1.10.11.0"),sQuery(id+"F0.wireOp",EDGE,"E1.10.12.0"),sQuery(id+"F0.wireOp",EDGE,"E1.10.13.0"),sQuery(id+"F0.wireOp",EDGE,"E1.10.14.0"),sQuery(id+"F0.wireOp",EDGE,"E1.10.15.0"),sQuery(id+"F0.wireOp",EDGE,"E1.10.16.0"),sQuery(id+"F0.wireOp",EDGE,"E1.10.17.0"),sQuery(id+"F0.wireOp",EDGE,"E1.10.18.0"),subQ41,sQuery(id+"F0.wireOp",EDGE,"E1.11.1.0"),sQuery(id+"F0.wireOp",EDGE,"E1.11.2.0"),sQuery(id+"F0.wireOp",EDGE,"E1.11.3.0"),sQuery(id+"F0.wireOp",EDGE,"E1.11.4.0"),sQuery(id+"F0.wireOp",EDGE,"E1.11.5.0"),sQuery(id+"F0.wireOp",EDGE,"E1.11.6.0"),sQuery(id+"F0.wireOp",EDGE,"E1.11.7.0"),sQuery(id+"F0.wireOp",EDGE,"E1.11.8.0"),sQuery(id+"F0.wireOp",EDGE,"E1.11.9.0"),sQuery(id+"F0.wireOp",EDGE,"E1.11.10.0"),sQuery(id+"F0.wireOp",EDGE,"E1.11.11.0"),sQuery(id+"F0.wireOp",EDGE,"E1.11.12.0"),sQuery(id+"F0.wireOp",EDGE,"E1.11.13.0"),sQuery(id+"F0.wireOp",EDGE,"E1.11.14.0"),sQuery(id+"F0.wireOp",EDGE,"E1.11.15.0"),sQuery(id+"F0.wireOp",EDGE,"E1.11.16.0"),sQuery(id+"F0.wireOp",EDGE,"E1.11.17.0"),sQuery(id+"F0.wireOp",EDGE,"E1.11.18.0"),subQ36,sQuery(id+"F0.wireOp",EDGE,"E1.12.1.0"),sQuery(id+"F0.wireOp",EDGE,"E1.12.2.0"),sQuery(id+"F0.wireOp",EDGE,"E1.12.3.0"),sQuery(id+"F0.wireOp",EDGE,"E1.12.4.0"),sQuery(id+"F0.wireOp",EDGE,"E1.12.5.0"),sQuery(id+"F0.wireOp",EDGE,"E1.12.6.0"),sQuery(id+"F0.wireOp",EDGE,"E1.12.7.0"),sQuery(id+"F0.wireOp",EDGE,"E1.12.8.0"),sQuery(id+"F0.wireOp",EDGE,"E1.12.9.0"),sQuery(id+"F0.wireOp",EDGE,"E1.12.10.0"),sQuery(id+"F0.wireOp",EDGE,"E1.12.11.0"),sQuery(id+"F0.wireOp",EDGE,"E1.12.12.0"),sQuery(id+"F0.wireOp",EDGE,"E1.12.13.0"),sQuery(id+"F0.wireOp",EDGE,"E1.12.14.0"),sQuery(id+"F0.wireOp",EDGE,"E1.12.15.0"),sQuery(id+"F0.wireOp",EDGE,"E1.12.16.0"),sQuery(id+"F0.wireOp",EDGE,"E1.12.17.0"),sQuery(id+"F0.wireOp",EDGE,"E1.12.18.0"),subQ42,sQuery(id+"F0.wireOp",EDGE,"E1.13.1.0"),sQuery(id+"F0.wireOp",EDGE,"E1.13.2.0"),sQuery(id+"F0.wireOp",EDGE,"E1.13.3.0"),sQuery(id+"F0.wireOp",EDGE,"E1.13.4.0"),sQuery(id+"F0.wireOp",EDGE,"E1.13.5.0"),sQuery(id+"F0.wireOp",EDGE,"E1.13.6.0"),sQuery(id+"F0.wireOp",EDGE,"E1.13.7.0"),sQuery(id+"F0.wireOp",EDGE,"E1.13.8.0"),sQuery(id+"F0.wireOp",EDGE,"E1.13.9.0"),sQuery(id+"F0.wireOp",EDGE,"E1.13.10.0"),sQuery(id+"F0.wireOp",EDGE,"E1.13.11.0"),sQuery(id+"F0.wireOp",EDGE,"E1.13.12.0"),sQuery(id+"F0.wireOp",EDGE,"E1.13.13.0"),sQuery(id+"F0.wireOp",EDGE,"E1.13.14.0"),sQuery(id+"F0.wireOp",EDGE,"E1.13.15.0"),sQuery(id+"F0.wireOp",EDGE,"E1.13.16.0"),sQuery(id+"F0.wireOp",EDGE,"E1.13.17.0"),sQuery(id+"F0.wireOp",EDGE,"E1.13.18.0"),subQ43,sQuery(id+"F0.wireOp",EDGE,"E1.14.1.0"),sQuery(id+"F0.wireOp",EDGE,"E1.14.2.0"),sQuery(id+"F0.wireOp",EDGE,"E1.14.3.0"),sQuery(id+"F0.wireOp",EDGE,"E1.14.4.0"),sQuery(id+"F0.wireOp",EDGE,"E1.14.5.0"),sQuery(id+"F0.wireOp",EDGE,"E1.14.6.0"),sQuery(id+"F0.wireOp",EDGE,"E1.14.7.0"),sQuery(id+"F0.wireOp",EDGE,"E1.14.8.0"),sQuery(id+"F0.wireOp",EDGE,"E1.14.9.0"),sQuery(id+"F0.wireOp",EDGE,"E1.14.10.0"),sQuery(id+"F0.wireOp",EDGE,"E1.14.11.0"),sQuery(id+"F0.wireOp",EDGE,"E1.14.12.0"),sQuery(id+"F0.wireOp",EDGE,"E1.14.13.0"),sQuery(id+"F0.wireOp",EDGE,"E1.14.14.0"),sQuery(id+"F0.wireOp",EDGE,"E1.14.15.0"),sQuery(id+"F0.wireOp",EDGE,"E1.14.16.0"),sQuery(id+"F0.wireOp",EDGE,"E1.14.17.0"),sQuery(id+"F0.wireOp",EDGE,"E1.14.18.0"),subQ44,sQuery(id+"F0.wireOp",EDGE,"E1.15.1.0"),sQuery(id+"F0.wireOp",EDGE,"E1.15.2.0"),sQuery(id+"F0.wireOp",EDGE,"E1.15.3.0"),sQuery(id+"F0.wireOp",EDGE,"E1.15.4.0"),sQuery(id+"F0.wireOp",EDGE,"E1.15.5.0"),sQuery(id+"F0.wireOp",EDGE,"E1.15.6.0"),sQuery(id+"F0.wireOp",EDGE,"E1.15.7.0"),sQuery(id+"F0.wireOp",EDGE,"E1.15.8.0"),sQuery(id+"F0.wireOp",EDGE,"E1.15.9.0"),sQuery(id+"F0.wireOp",EDGE,"E1.15.10.0"),sQuery(id+"F0.wireOp",EDGE,"E1.15.11.0"),sQuery(id+"F0.wireOp",EDGE,"E1.15.12.0"),sQuery(id+"F0.wireOp",EDGE,"E1.15.13.0"),sQuery(id+"F0.wireOp",EDGE,"E1.15.14.0"),sQuery(id+"F0.wireOp",EDGE,"E1.15.15.0"),sQuery(id+"F0.wireOp",EDGE,"E1.15.16.0"),sQuery(id+"F0.wireOp",EDGE,"E1.15.17.0"),sQuery(id+"F0.wireOp",EDGE,"E1.15.18.0"),subQ45,sQuery(id+"F0.wireOp",EDGE,"E1.16.1.0"),sQuery(id+"F0.wireOp",EDGE,"E1.16.2.0"),sQuery(id+"F0.wireOp",EDGE,"E1.16.3.0"),sQuery(id+"F0.wireOp",EDGE,"E1.16.4.0"),sQuery(id+"F0.wireOp",EDGE,"E1.16.5.0"),sQuery(id+"F0.wireOp",EDGE,"E1.16.6.0"),sQuery(id+"F0.wireOp",EDGE,"E1.16.7.0"),sQuery(id+"F0.wireOp",EDGE,"E1.16.8.0"),sQuery(id+"F0.wireOp",EDGE,"E1.16.9.0"),sQuery(id+"F0.wireOp",EDGE,"E1.16.10.0"),sQuery(id+"F0.wireOp",EDGE,"E1.16.11.0"),sQuery(id+"F0.wireOp",EDGE,"E1.16.12.0"),sQuery(id+"F0.wireOp",EDGE,"E1.16.13.0"),sQuery(id+"F0.wireOp",EDGE,"E1.16.14.0"),sQuery(id+"F0.wireOp",EDGE,"E1.16.15.0"),sQuery(id+"F0.wireOp",EDGE,"E1.16.16.0"),sQuery(id+"F0.wireOp",EDGE,"E1.16.17.0"),sQuery(id+"F0.wireOp",EDGE,"E1.16.18.0"),subQ46,sQuery(id+"F0.wireOp",EDGE,"E1.17.1.0"),sQuery(id+"F0.wireOp",EDGE,"E1.17.2.0"),sQuery(id+"F0.wireOp",EDGE,"E1.17.3.0"),sQuery(id+"F0.wireOp",EDGE,"E1.17.4.0"),sQuery(id+"F0.wireOp",EDGE,"E1.17.5.0"),sQuery(id+"F0.wireOp",EDGE,"E1.17.6.0"),sQuery(id+"F0.wireOp",EDGE,"E1.17.7.0"),sQuery(id+"F0.wireOp",EDGE,"E1.17.8.0"),sQuery(id+"F0.wireOp",EDGE,"E1.17.9.0"),sQuery(id+"F0.wireOp",EDGE,"E1.17.10.0"),sQuery(id+"F0.wireOp",EDGE,"E1.17.11.0"),sQuery(id+"F0.wireOp",EDGE,"E1.17.12.0"),sQuery(id+"F0.wireOp",EDGE,"E1.17.13.0"),sQuery(id+"F0.wireOp",EDGE,"E1.17.14.0"),sQuery(id+"F0.wireOp",EDGE,"E1.17.15.0"),sQuery(id+"F0.wireOp",EDGE,"E1.17.16.0"),sQuery(id+"F0.wireOp",EDGE,"E1.17.17.0"),sQuery(id+"F0.wireOp",EDGE,"E1.17.18.0"),subQ47,sQuery(id+"F0.wireOp",EDGE,"E1.18.1.0"),sQuery(id+"F0.wireOp",EDGE,"E1.18.2.0"),sQuery(id+"F0.wireOp",EDGE,"E1.18.3.0"),sQuery(id+"F0.wireOp",EDGE,"E1.18.4.0"),sQuery(id+"F0.wireOp",EDGE,"E1.18.5.0"),sQuery(id+"F0.wireOp",EDGE,"E1.18.6.0"),sQuery(id+"F0.wireOp",EDGE,"E1.18.7.0"),sQuery(id+"F0.wireOp",EDGE,"E1.18.8.0"),sQuery(id+"F0.wireOp",EDGE,"E1.18.9.0"),sQuery(id+"F0.wireOp",EDGE,"E1.18.10.0"),sQuery(id+"F0.wireOp",EDGE,"E1.18.11.0"),sQuery(id+"F0.wireOp",EDGE,"E1.18.12.0"),sQuery(id+"F0.wireOp",EDGE,"E1.18.13.0"),sQuery(id+"F0.wireOp",EDGE,"E1.18.14.0"),sQuery(id+"F0.wireOp",EDGE,"E1.18.15.0"),sQuery(id+"F0.wireOp",EDGE,"E1.18.16.0"),sQuery(id+"F0.wireOp",EDGE,"E1.18.17.0"),sQuery(id+"F0.wireOp",EDGE,"E1.18.18.0"),subQ48,sQuery(id+"F0.wireOp",EDGE,"E1.19.1.0"),sQuery(id+"F0.wireOp",EDGE,"E1.19.2.0"),sQuery(id+"F0.wireOp",EDGE,"E1.19.3.0"),sQuery(id+"F0.wireOp",EDGE,"E1.19.4.0"),sQuery(id+"F0.wireOp",EDGE,"E1.19.5.0"),sQuery(id+"F0.wireOp",EDGE,"E1.19.6.0"),sQuery(id+"F0.wireOp",EDGE,"E1.19.7.0"),sQuery(id+"F0.wireOp",EDGE,"E1.19.8.0"),sQuery(id+"F0.wireOp",EDGE,"E1.19.9.0"),sQuery(id+"F0.wireOp",EDGE,"E1.19.10.0"),sQuery(id+"F0.wireOp",EDGE,"E1.19.11.0"),sQuery(id+"F0.wireOp",EDGE,"E1.19.12.0"),sQuery(id+"F0.wireOp",EDGE,"E1.19.13.0"),sQuery(id+"F0.wireOp",EDGE,"E1.19.14.0"),sQuery(id+"F0.wireOp",EDGE,"E1.19.15.0"),sQuery(id+"F0.wireOp",EDGE,"E1.19.16.0"),sQuery(id+"F0.wireOp",EDGE,"E1.19.17.0"),sQuery(id+"F0.wireOp",EDGE,"E1.19.18.0"),subQ49,sQuery(id+"F0.wireOp",EDGE,"E1.20.1.0"),sQuery(id+"F0.wireOp",EDGE,"E1.20.2.0"),sQuery(id+"F0.wireOp",EDGE,"E1.20.3.0"),sQuery(id+"F0.wireOp",EDGE,"E1.20.4.0"),sQuery(id+"F0.wireOp",EDGE,"E1.20.5.0"),sQuery(id+"F0.wireOp",EDGE,"E1.20.6.0"),sQuery(id+"F0.wireOp",EDGE,"E1.20.7.0"),sQuery(id+"F0.wireOp",EDGE,"E1.20.8.0"),sQuery(id+"F0.wireOp",EDGE,"E1.20.9.0"),sQuery(id+"F0.wireOp",EDGE,"E1.20.10.0"),sQuery(id+"F0.wireOp",EDGE,"E1.20.11.0"),sQuery(id+"F0.wireOp",EDGE,"E1.20.12.0"),sQuery(id+"F0.wireOp",EDGE,"E1.20.13.0"),sQuery(id+"F0.wireOp",EDGE,"E1.20.14.0"),sQuery(id+"F0.wireOp",EDGE,"E1.20.15.0"),sQuery(id+"F0.wireOp",EDGE,"E1.20.16.0"),sQuery(id+"F0.wireOp",EDGE,"E1.20.17.0"),sQuery(id+"F0.wireOp",EDGE,"E1.20.18.0"),subQ50,sQuery(id+"F0.wireOp",EDGE,"E1.21.1.0"),sQuery(id+"F0.wireOp",EDGE,"E1.21.2.0"),sQuery(id+"F0.wireOp",EDGE,"E1.21.3.0"),sQuery(id+"F0.wireOp",EDGE,"E1.21.4.0"),sQuery(id+"F0.wireOp",EDGE,"E1.21.5.0"),sQuery(id+"F0.wireOp",EDGE,"E1.21.6.0"),sQuery(id+"F0.wireOp",EDGE,"E1.21.7.0"),sQuery(id+"F0.wireOp",EDGE,"E1.21.8.0"),sQuery(id+"F0.wireOp",EDGE,"E1.21.9.0"),sQuery(id+"F0.wireOp",EDGE,"E1.21.10.0"),sQuery(id+"F0.wireOp",EDGE,"E1.21.11.0"),sQuery(id+"F0.wireOp",EDGE,"E1.21.12.0"),sQuery(id+"F0.wireOp",EDGE,"E1.21.13.0"),sQuery(id+"F0.wireOp",EDGE,"E1.21.14.0"),sQuery(id+"F0.wireOp",EDGE,"E1.21.15.0"),sQuery(id+"F0.wireOp",EDGE,"E1.21.16.0"),sQuery(id+"F0.wireOp",EDGE,"E1.21.17.0"),sQuery(id+"F0.wireOp",EDGE,"E1.21.18.0"),subQ27,sQuery(id+"F0.wireOp",EDGE,"E1.22.1.0"),sQuery(id+"F0.wireOp",EDGE,"E1.22.2.0"),sQuery(id+"F0.wireOp",EDGE,"E1.22.3.0"),sQuery(id+"F0.wireOp",EDGE,"E1.22.4.0"),sQuery(id+"F0.wireOp",EDGE,"E1.22.5.0"),sQuery(id+"F0.wireOp",EDGE,"E1.22.6.0"),sQuery(id+"F0.wireOp",EDGE,"E1.22.7.0"),sQuery(id+"F0.wireOp",EDGE,"E1.22.8.0"),sQuery(id+"F0.wireOp",EDGE,"E1.22.9.0"),sQuery(id+"F0.wireOp",EDGE,"E1.22.10.0"),sQuery(id+"F0.wireOp",EDGE,"E1.22.11.0"),sQuery(id+"F0.wireOp",EDGE,"E1.22.12.0"),sQuery(id+"F0.wireOp",EDGE,"E1.22.13.0"),sQuery(id+"F0.wireOp",EDGE,"E1.22.14.0"),sQuery(id+"F0.wireOp",EDGE,"E1.22.15.0"),sQuery(id+"F0.wireOp",EDGE,"E1.22.16.0"),sQuery(id+"F0.wireOp",EDGE,"E1.22.17.0"),sQuery(id+"F0.wireOp",EDGE,"E1.22.18.0"),subQ26,sQuery(id+"F0.wireOp",EDGE,"E1.23.1.0"),sQuery(id+"F0.wireOp",EDGE,"E1.23.2.0"),sQuery(id+"F0.wireOp",EDGE,"E1.23.3.0"),sQuery(id+"F0.wireOp",EDGE,"E1.23.4.0"),sQuery(id+"F0.wireOp",EDGE,"E1.23.5.0"),sQuery(id+"F0.wireOp",EDGE,"E1.23.6.0"),sQuery(id+"F0.wireOp",EDGE,"E1.23.7.0"),sQuery(id+"F0.wireOp",EDGE,"E1.23.8.0"),sQuery(id+"F0.wireOp",EDGE,"E1.23.9.0"),sQuery(id+"F0.wireOp",EDGE,"E1.23.10.0"),sQuery(id+"F0.wireOp",EDGE,"E1.23.11.0"),sQuery(id+"F0.wireOp",EDGE,"E1.23.12.0"),sQuery(id+"F0.wireOp",EDGE,"E1.23.13.0"),sQuery(id+"F0.wireOp",EDGE,"E1.23.14.0"),sQuery(id+"F0.wireOp",EDGE,"E1.23.15.0"),sQuery(id+"F0.wireOp",EDGE,"E1.23.16.0"),sQuery(id+"F0.wireOp",EDGE,"E1.23.17.0"),sQuery(id+"F0.wireOp",EDGE,"E1.23.18.0"),subQ25,sQuery(id+"F0.wireOp",EDGE,"E1.24.1.0"),sQuery(id+"F0.wireOp",EDGE,"E1.24.2.0"),sQuery(id+"F0.wireOp",EDGE,"E1.24.3.0"),sQuery(id+"F0.wireOp",EDGE,"E1.24.4.0"),sQuery(id+"F0.wireOp",EDGE,"E1.24.5.0"),sQuery(id+"F0.wireOp",EDGE,"E1.24.6.0"),sQuery(id+"F0.wireOp",EDGE,"E1.24.7.0"),sQuery(id+"F0.wireOp",EDGE,"E1.24.8.0"),sQuery(id+"F0.wireOp",EDGE,"E1.24.9.0"),sQuery(id+"F0.wireOp",EDGE,"E1.24.10.0"),sQuery(id+"F0.wireOp",EDGE,"E1.24.11.0"),sQuery(id+"F0.wireOp",EDGE,"E1.24.12.0"),sQuery(id+"F0.wireOp",EDGE,"E1.24.13.0"),sQuery(id+"F0.wireOp",EDGE,"E1.24.14.0"),sQuery(id+"F0.wireOp",EDGE,"E1.24.15.0"),sQuery(id+"F0.wireOp",EDGE,"E1.24.16.0"),sQuery(id+"F0.wireOp",EDGE,"E1.24.17.0"),sQuery(id+"F0.wireOp",EDGE,"E1.24.18.0"),subQ24,sQuery(id+"F0.wireOp",EDGE,"E1.25.1.0"),sQuery(id+"F0.wireOp",EDGE,"E1.25.2.0"),sQuery(id+"F0.wireOp",EDGE,"E1.25.3.0"),sQuery(id+"F0.wireOp",EDGE,"E1.25.4.0"),sQuery(id+"F0.wireOp",EDGE,"E1.25.5.0"),sQuery(id+"F0.wireOp",EDGE,"E1.25.6.0"),sQuery(id+"F0.wireOp",EDGE,"E1.25.7.0"),sQuery(id+"F0.wireOp",EDGE,"E1.25.8.0"),sQuery(id+"F0.wireOp",EDGE,"E1.25.9.0"),sQuery(id+"F0.wireOp",EDGE,"E1.25.10.0"),sQuery(id+"F0.wireOp",EDGE,"E1.25.11.0"),sQuery(id+"F0.wireOp",EDGE,"E1.25.12.0"),sQuery(id+"F0.wireOp",EDGE,"E1.25.13.0"),sQuery(id+"F0.wireOp",EDGE,"E1.25.14.0"),sQuery(id+"F0.wireOp",EDGE,"E1.25.15.0"),sQuery(id+"F0.wireOp",EDGE,"E1.25.16.0"),sQuery(id+"F0.wireOp",EDGE,"E1.25.17.0"),sQuery(id+"F0.wireOp",EDGE,"E1.25.18.0"),subQ23,sQuery(id+"F0.wireOp",EDGE,"E1.26.1.0"),sQuery(id+"F0.wireOp",EDGE,"E1.26.2.0"),sQuery(id+"F0.wireOp",EDGE,"E1.26.3.0"),sQuery(id+"F0.wireOp",EDGE,"E1.26.4.0"),sQuery(id+"F0.wireOp",EDGE,"E1.26.5.0"),sQuery(id+"F0.wireOp",EDGE,"E1.26.6.0"),sQuery(id+"F0.wireOp",EDGE,"E1.26.7.0"),sQuery(id+"F0.wireOp",EDGE,"E1.26.8.0"),sQuery(id+"F0.wireOp",EDGE,"E1.26.9.0"),sQuery(id+"F0.wireOp",EDGE,"E1.26.10.0"),sQuery(id+"F0.wireOp",EDGE,"E1.26.11.0"),sQuery(id+"F0.wireOp",EDGE,"E1.26.12.0"),sQuery(id+"F0.wireOp",EDGE,"E1.26.13.0"),sQuery(id+"F0.wireOp",EDGE,"E1.26.14.0"),sQuery(id+"F0.wireOp",EDGE,"E1.26.15.0"),sQuery(id+"F0.wireOp",EDGE,"E1.26.16.0"),sQuery(id+"F0.wireOp",EDGE,"E1.26.17.0"),sQuery(id+"F0.wireOp",EDGE,"E1.26.18.0"),subQ22,sQuery(id+"F0.wireOp",EDGE,"E1.27.1.0"),sQuery(id+"F0.wireOp",EDGE,"E1.27.2.0"),sQuery(id+"F0.wireOp",EDGE,"E1.27.3.0"),sQuery(id+"F0.wireOp",EDGE,"E1.27.4.0"),sQuery(id+"F0.wireOp",EDGE,"E1.27.5.0"),sQuery(id+"F0.wireOp",EDGE,"E1.27.6.0"),sQuery(id+"F0.wireOp",EDGE,"E1.27.7.0"),sQuery(id+"F0.wireOp",EDGE,"E1.27.8.0"),sQuery(id+"F0.wireOp",EDGE,"E1.27.9.0"),sQuery(id+"F0.wireOp",EDGE,"E1.27.10.0"),sQuery(id+"F0.wireOp",EDGE,"E1.27.11.0"),sQuery(id+"F0.wireOp",EDGE,"E1.27.12.0"),sQuery(id+"F0.wireOp",EDGE,"E1.27.13.0"),sQuery(id+"F0.wireOp",EDGE,"E1.27.14.0"),sQuery(id+"F0.wireOp",EDGE,"E1.27.15.0"),sQuery(id+"F0.wireOp",EDGE,"E1.27.16.0"),sQuery(id+"F0.wireOp",EDGE,"E1.27.17.0"),sQuery(id+"F0.wireOp",EDGE,"E1.27.18.0"),subQ21,sQuery(id+"F0.wireOp",EDGE,"E1.28.1.0"),sQuery(id+"F0.wireOp",EDGE,"E1.28.2.0"),sQuery(id+"F0.wireOp",EDGE,"E1.28.3.0"),sQuery(id+"F0.wireOp",EDGE,"E1.28.4.0"),sQuery(id+"F0.wireOp",EDGE,"E1.28.5.0"),sQuery(id+"F0.wireOp",EDGE,"E1.28.6.0"),sQuery(id+"F0.wireOp",EDGE,"E1.28.7.0"),sQuery(id+"F0.wireOp",EDGE,"E1.28.8.0"),sQuery(id+"F0.wireOp",EDGE,"E1.28.9.0"),sQuery(id+"F0.wireOp",EDGE,"E1.28.10.0"),sQuery(id+"F0.wireOp",EDGE,"E1.28.11.0"),sQuery(id+"F0.wireOp",EDGE,"E1.28.12.0"),sQuery(id+"F0.wireOp",EDGE,"E1.28.13.0"),sQuery(id+"F0.wireOp",EDGE,"E1.28.14.0"),sQuery(id+"F0.wireOp",EDGE,"E1.28.15.0"),sQuery(id+"F0.wireOp",EDGE,"E1.28.16.0"),sQuery(id+"F0.wireOp",EDGE,"E1.28.17.0"),sQuery(id+"F0.wireOp",EDGE,"E1.28.18.0"),subQ20,sQuery(id+"F0.wireOp",EDGE,"E1.29.1.0"),sQuery(id+"F0.wireOp",EDGE,"E1.29.2.0"),sQuery(id+"F0.wireOp",EDGE,"E1.29.3.0"),sQuery(id+"F0.wireOp",EDGE,"E1.29.4.0"),sQuery(id+"F0.wireOp",EDGE,"E1.29.5.0"),sQuery(id+"F0.wireOp",EDGE,"E1.29.6.0"),sQuery(id+"F0.wireOp",EDGE,"E1.29.7.0"),sQuery(id+"F0.wireOp",EDGE,"E1.29.8.0"),sQuery(id+"F0.wireOp",EDGE,"E1.29.9.0"),sQuery(id+"F0.wireOp",EDGE,"E1.29.10.0"),sQuery(id+"F0.wireOp",EDGE,"E1.29.11.0"),sQuery(id+"F0.wireOp",EDGE,"E1.29.12.0"),sQuery(id+"F0.wireOp",EDGE,"E1.29.13.0"),sQuery(id+"F0.wireOp",EDGE,"E1.29.14.0"),sQuery(id+"F0.wireOp",EDGE,"E1.29.15.0"),sQuery(id+"F0.wireOp",EDGE,"E1.29.16.0"),sQuery(id+"F0.wireOp",EDGE,"E1.29.17.0"),sQuery(id+"F0.wireOp",EDGE,"E1.29.18.0"),subQ18,sQuery(id+"F0.wireOp",EDGE,"E1.30.1.0"),sQuery(id+"F0.wireOp",EDGE,"E1.30.2.0"),sQuery(id+"F0.wireOp",EDGE,"E1.30.3.0"),sQuery(id+"F0.wireOp",EDGE,"E1.30.4.0"),sQuery(id+"F0.wireOp",EDGE,"E1.30.5.0"),sQuery(id+"F0.wireOp",EDGE,"E1.30.6.0"),sQuery(id+"F0.wireOp",EDGE,"E1.30.7.0"),sQuery(id+"F0.wireOp",EDGE,"E1.30.8.0"),sQuery(id+"F0.wireOp",EDGE,"E1.30.9.0"),sQuery(id+"F0.wireOp",EDGE,"E1.30.10.0"),sQuery(id+"F0.wireOp",EDGE,"E1.30.11.0"),sQuery(id+"F0.wireOp",EDGE,"E1.30.12.0"),sQuery(id+"F0.wireOp",EDGE,"E1.30.13.0"),sQuery(id+"F0.wireOp",EDGE,"E1.30.14.0"),sQuery(id+"F0.wireOp",EDGE,"E1.30.15.0"),sQuery(id+"F0.wireOp",EDGE,"E1.30.16.0"),sQuery(id+"F0.wireOp",EDGE,"E1.30.17.0"),sQuery(id+"F0.wireOp",EDGE,"E1.30.18.0"),subQ17,sQuery(id+"F0.wireOp",EDGE,"E1.31.1.0"),sQuery(id+"F0.wireOp",EDGE,"E1.31.2.0"),sQuery(id+"F0.wireOp",EDGE,"E1.31.3.0"),sQuery(id+"F0.wireOp",EDGE,"E1.31.4.0"),sQuery(id+"F0.wireOp",EDGE,"E1.31.5.0"),sQuery(id+"F0.wireOp",EDGE,"E1.31.6.0"),sQuery(id+"F0.wireOp",EDGE,"E1.31.7.0"),sQuery(id+"F0.wireOp",EDGE,"E1.31.8.0"),sQuery(id+"F0.wireOp",EDGE,"E1.31.9.0"),sQuery(id+"F0.wireOp",EDGE,"E1.31.10.0"),sQuery(id+"F0.wireOp",EDGE,"E1.31.11.0"),sQuery(id+"F0.wireOp",EDGE,"E1.31.12.0"),sQuery(id+"F0.wireOp",EDGE,"E1.31.13.0"),sQuery(id+"F0.wireOp",EDGE,"E1.31.14.0"),sQuery(id+"F0.wireOp",EDGE,"E1.31.15.0"),sQuery(id+"F0.wireOp",EDGE,"E1.31.16.0"),sQuery(id+"F0.wireOp",EDGE,"E1.31.17.0"),sQuery(id+"F0.wireOp",EDGE,"E1.31.18.0"),subQ16,sQuery(id+"F0.wireOp",EDGE,"E1.32.1.0"),sQuery(id+"F0.wireOp",EDGE,"E1.32.2.0"),sQuery(id+"F0.wireOp",EDGE,"E1.32.3.0"),sQuery(id+"F0.wireOp",EDGE,"E1.32.4.0"),sQuery(id+"F0.wireOp",EDGE,"E1.32.5.0"),sQuery(id+"F0.wireOp",EDGE,"E1.32.6.0"),sQuery(id+"F0.wireOp",EDGE,"E1.32.7.0"),sQuery(id+"F0.wireOp",EDGE,"E1.32.8.0"),sQuery(id+"F0.wireOp",EDGE,"E1.32.9.0"),sQuery(id+"F0.wireOp",EDGE,"E1.32.10.0"),sQuery(id+"F0.wireOp",EDGE,"E1.32.11.0"),sQuery(id+"F0.wireOp",EDGE,"E1.32.12.0"),sQuery(id+"F0.wireOp",EDGE,"E1.32.13.0"),sQuery(id+"F0.wireOp",EDGE,"E1.32.14.0"),sQuery(id+"F0.wireOp",EDGE,"E1.32.15.0"),sQuery(id+"F0.wireOp",EDGE,"E1.32.16.0"),sQuery(id+"F0.wireOp",EDGE,"E1.32.17.0"),sQuery(id+"F0.wireOp",EDGE,"E1.32.18.0"),subQ15,sQuery(id+"F0.wireOp",EDGE,"E1.33.1.0"),sQuery(id+"F0.wireOp",EDGE,"E1.33.2.0"),sQuery(id+"F0.wireOp",EDGE,"E1.33.3.0"),sQuery(id+"F0.wireOp",EDGE,"E1.33.4.0"),sQuery(id+"F0.wireOp",EDGE,"E1.33.5.0"),sQuery(id+"F0.wireOp",EDGE,"E1.33.6.0"),sQuery(id+"F0.wireOp",EDGE,"E1.33.7.0"),sQuery(id+"F0.wireOp",EDGE,"E1.33.8.0"),sQuery(id+"F0.wireOp",EDGE,"E1.33.9.0"),sQuery(id+"F0.wireOp",EDGE,"E1.33.10.0"),sQuery(id+"F0.wireOp",EDGE,"E1.33.11.0"),sQuery(id+"F0.wireOp",EDGE,"E1.33.12.0"),sQuery(id+"F0.wireOp",EDGE,"E1.33.13.0"),sQuery(id+"F0.wireOp",EDGE,"E1.33.14.0"),sQuery(id+"F0.wireOp",EDGE,"E1.33.15.0"),sQuery(id+"F0.wireOp",EDGE,"E1.33.16.0"),sQuery(id+"F0.wireOp",EDGE,"E1.33.17.0"),sQuery(id+"F0.wireOp",EDGE,"E1.33.18.0"),subQ14,sQuery(id+"F0.wireOp",EDGE,"E1.34.1.0"),sQuery(id+"F0.wireOp",EDGE,"E1.34.2.0"),sQuery(id+"F0.wireOp",EDGE,"E1.34.3.0"),sQuery(id+"F0.wireOp",EDGE,"E1.34.4.0"),sQuery(id+"F0.wireOp",EDGE,"E1.34.5.0"),sQuery(id+"F0.wireOp",EDGE,"E1.34.6.0"),sQuery(id+"F0.wireOp",EDGE,"E1.34.7.0"),sQuery(id+"F0.wireOp",EDGE,"E1.34.8.0"),sQuery(id+"F0.wireOp",EDGE,"E1.34.9.0"),sQuery(id+"F0.wireOp",EDGE,"E1.34.10.0"),sQuery(id+"F0.wireOp",EDGE,"E1.34.11.0"),sQuery(id+"F0.wireOp",EDGE,"E1.34.12.0"),sQuery(id+"F0.wireOp",EDGE,"E1.34.13.0"),sQuery(id+"F0.wireOp",EDGE,"E1.34.14.0"),sQuery(id+"F0.wireOp",EDGE,"E1.34.15.0"),sQuery(id+"F0.wireOp",EDGE,"E1.34.16.0"),sQuery(id+"F0.wireOp",EDGE,"E1.34.17.0"),sQuery(id+"F0.wireOp",EDGE,"E1.34.18.0"),subQ13,sQuery(id+"F0.wireOp",EDGE,"E1.35.1.0"),sQuery(id+"F0.wireOp",EDGE,"E1.35.2.0"),sQuery(id+"F0.wireOp",EDGE,"E1.35.3.0"),sQuery(id+"F0.wireOp",EDGE,"E1.35.4.0"),sQuery(id+"F0.wireOp",EDGE,"E1.35.5.0"),sQuery(id+"F0.wireOp",EDGE,"E1.35.6.0"),sQuery(id+"F0.wireOp",EDGE,"E1.35.7.0"),sQuery(id+"F0.wireOp",EDGE,"E1.35.8.0"),sQuery(id+"F0.wireOp",EDGE,"E1.35.9.0"),sQuery(id+"F0.wireOp",EDGE,"E1.35.10.0"),sQuery(id+"F0.wireOp",EDGE,"E1.35.11.0"),sQuery(id+"F0.wireOp",EDGE,"E1.35.12.0"),sQuery(id+"F0.wireOp",EDGE,"E1.35.13.0"),sQuery(id+"F0.wireOp",EDGE,"E1.35.14.0"),sQuery(id+"F0.wireOp",EDGE,"E1.35.15.0"),sQuery(id+"F0.wireOp",EDGE,"E1.35.16.0"),sQuery(id+"F0.wireOp",EDGE,"E1.35.17.0"),sQuery(id+"F0.wireOp",EDGE,"E1.35.18.0"),subQ12,sQuery(id+"F0.wireOp",EDGE,"E1.36.1.0"),sQuery(id+"F0.wireOp",EDGE,"E1.36.2.0"),sQuery(id+"F0.wireOp",EDGE,"E1.36.3.0"),sQuery(id+"F0.wireOp",EDGE,"E1.36.4.0"),sQuery(id+"F0.wireOp",EDGE,"E1.36.5.0"),sQuery(id+"F0.wireOp",EDGE,"E1.36.6.0"),sQuery(id+"F0.wireOp",EDGE,"E1.36.7.0"),sQuery(id+"F0.wireOp",EDGE,"E1.36.8.0"),sQuery(id+"F0.wireOp",EDGE,"E1.36.9.0"),sQuery(id+"F0.wireOp",EDGE,"E1.36.10.0"),sQuery(id+"F0.wireOp",EDGE,"E1.36.11.0"),sQuery(id+"F0.wireOp",EDGE,"E1.36.12.0"),sQuery(id+"F0.wireOp",EDGE,"E1.36.13.0"),sQuery(id+"F0.wireOp",EDGE,"E1.36.14.0"),sQuery(id+"F0.wireOp",EDGE,"E1.36.15.0"),sQuery(id+"F0.wireOp",EDGE,"E1.36.16.0"),sQuery(id+"F0.wireOp",EDGE,"E1.36.17.0"),sQuery(id+"F0.wireOp",EDGE,"E1.36.18.0"),subQ35,sQuery(id+"F0.wireOp",EDGE,"E1.37.1.0"),sQuery(id+"F0.wireOp",EDGE,"E1.37.2.0"),sQuery(id+"F0.wireOp",EDGE,"E1.37.3.0"),sQuery(id+"F0.wireOp",EDGE,"E1.37.4.0"),sQuery(id+"F0.wireOp",EDGE,"E1.37.5.0"),sQuery(id+"F0.wireOp",EDGE,"E1.37.6.0"),sQuery(id+"F0.wireOp",EDGE,"E1.37.7.0"),sQuery(id+"F0.wireOp",EDGE,"E1.37.8.0"),sQuery(id+"F0.wireOp",EDGE,"E1.37.9.0"),sQuery(id+"F0.wireOp",EDGE,"E1.37.10.0"),sQuery(id+"F0.wireOp",EDGE,"E1.37.11.0"),sQuery(id+"F0.wireOp",EDGE,"E1.37.12.0"),sQuery(id+"F0.wireOp",EDGE,"E1.37.13.0"),sQuery(id+"F0.wireOp",EDGE,"E1.37.14.0"),sQuery(id+"F0.wireOp",EDGE,"E1.37.15.0"),sQuery(id+"F0.wireOp",EDGE,"E1.37.16.0"),sQuery(id+"F0.wireOp",EDGE,"E1.37.17.0"),sQuery(id+"F0.wireOp",EDGE,"E1.37.18.0"),subQ11,sQuery(id+"F0.wireOp",EDGE,"E1.38.1.0"),sQuery(id+"F0.wireOp",EDGE,"E1.38.2.0"),sQuery(id+"F0.wireOp",EDGE,"E1.38.3.0"),sQuery(id+"F0.wireOp",EDGE,"E1.38.4.0"),sQuery(id+"F0.wireOp",EDGE,"E1.38.5.0"),sQuery(id+"F0.wireOp",EDGE,"E1.38.6.0"),sQuery(id+"F0.wireOp",EDGE,"E1.38.7.0"),sQuery(id+"F0.wireOp",EDGE,"E1.38.8.0"),sQuery(id+"F0.wireOp",EDGE,"E1.38.9.0"),sQuery(id+"F0.wireOp",EDGE,"E1.38.10.0"),sQuery(id+"F0.wireOp",EDGE,"E1.38.11.0"),sQuery(id+"F0.wireOp",EDGE,"E1.38.12.0"),sQuery(id+"F0.wireOp",EDGE,"E1.38.13.0"),sQuery(id+"F0.wireOp",EDGE,"E1.38.14.0"),sQuery(id+"F0.wireOp",EDGE,"E1.38.15.0"),sQuery(id+"F0.wireOp",EDGE,"E1.38.16.0"),sQuery(id+"F0.wireOp",EDGE,"E1.38.17.0"),sQuery(id+"F0.wireOp",EDGE,"E1.38.18.0"),subQ10,sQuery(id+"F0.wireOp",EDGE,"E1.39.1.0"),sQuery(id+"F0.wireOp",EDGE,"E1.39.2.0"),sQuery(id+"F0.wireOp",EDGE,"E1.39.3.0"),sQuery(id+"F0.wireOp",EDGE,"E1.39.4.0"),sQuery(id+"F0.wireOp",EDGE,"E1.39.5.0"),sQuery(id+"F0.wireOp",EDGE,"E1.39.6.0"),sQuery(id+"F0.wireOp",EDGE,"E1.39.7.0"),sQuery(id+"F0.wireOp",EDGE,"E1.39.8.0"),sQuery(id+"F0.wireOp",EDGE,"E1.39.9.0"),sQuery(id+"F0.wireOp",EDGE,"E1.39.10.0"),sQuery(id+"F0.wireOp",EDGE,"E1.39.11.0"),sQuery(id+"F0.wireOp",EDGE,"E1.39.12.0"),sQuery(id+"F0.wireOp",EDGE,"E1.39.13.0"),sQuery(id+"F0.wireOp",EDGE,"E1.39.14.0"),sQuery(id+"F0.wireOp",EDGE,"E1.39.15.0"),sQuery(id+"F0.wireOp",EDGE,"E1.39.16.0"),sQuery(id+"F0.wireOp",EDGE,"E1.39.17.0"),sQuery(id+"F0.wireOp",EDGE,"E1.39.18.0"),subQ9,sQuery(id+"F0.wireOp",EDGE,"E1.40.1.0"),sQuery(id+"F0.wireOp",EDGE,"E1.40.2.0"),sQuery(id+"F0.wireOp",EDGE,"E1.40.3.0"),sQuery(id+"F0.wireOp",EDGE,"E1.40.4.0"),sQuery(id+"F0.wireOp",EDGE,"E1.40.5.0"),sQuery(id+"F0.wireOp",EDGE,"E1.40.6.0"),sQuery(id+"F0.wireOp",EDGE,"E1.40.7.0"),sQuery(id+"F0.wireOp",EDGE,"E1.40.8.0"),sQuery(id+"F0.wireOp",EDGE,"E1.40.9.0"),sQuery(id+"F0.wireOp",EDGE,"E1.40.10.0"),sQuery(id+"F0.wireOp",EDGE,"E1.40.11.0"),sQuery(id+"F0.wireOp",EDGE,"E1.40.12.0"),sQuery(id+"F0.wireOp",EDGE,"E1.40.13.0"),sQuery(id+"F0.wireOp",EDGE,"E1.40.14.0"),sQuery(id+"F0.wireOp",EDGE,"E1.40.15.0"),sQuery(id+"F0.wireOp",EDGE,"E1.40.16.0"),sQuery(id+"F0.wireOp",EDGE,"E1.40.17.0"),sQuery(id+"F0.wireOp",EDGE,"E1.40.18.0"),subQ8,sQuery(id+"F0.wireOp",EDGE,"E1.41.1.0"),sQuery(id+"F0.wireOp",EDGE,"E1.41.2.0"),sQuery(id+"F0.wireOp",EDGE,"E1.41.3.0"),sQuery(id+"F0.wireOp",EDGE,"E1.41.4.0"),sQuery(id+"F0.wireOp",EDGE,"E1.41.5.0"),sQuery(id+"F0.wireOp",EDGE,"E1.41.6.0"),sQuery(id+"F0.wireOp",EDGE,"E1.41.7.0"),sQuery(id+"F0.wireOp",EDGE,"E1.41.8.0"),sQuery(id+"F0.wireOp",EDGE,"E1.41.9.0"),sQuery(id+"F0.wireOp",EDGE,"E1.41.10.0"),sQuery(id+"F0.wireOp",EDGE,"E1.41.11.0"),sQuery(id+"F0.wireOp",EDGE,"E1.41.12.0"),sQuery(id+"F0.wireOp",EDGE,"E1.41.13.0"),sQuery(id+"F0.wireOp",EDGE,"E1.41.14.0"),sQuery(id+"F0.wireOp",EDGE,"E1.41.15.0"),sQuery(id+"F0.wireOp",EDGE,"E1.41.16.0"),sQuery(id+"F0.wireOp",EDGE,"E1.41.17.0"),sQuery(id+"F0.wireOp",EDGE,"E1.41.18.0"),subQ7,sQuery(id+"F0.wireOp",EDGE,"E1.42.1.0"),sQuery(id+"F0.wireOp",EDGE,"E1.42.2.0"),sQuery(id+"F0.wireOp",EDGE,"E1.42.3.0"),sQuery(id+"F0.wireOp",EDGE,"E1.42.4.0"),sQuery(id+"F0.wireOp",EDGE,"E1.42.5.0"),sQuery(id+"F0.wireOp",EDGE,"E1.42.6.0"),sQuery(id+"F0.wireOp",EDGE,"E1.42.7.0"),sQuery(id+"F0.wireOp",EDGE,"E1.42.8.0"),sQuery(id+"F0.wireOp",EDGE,"E1.42.9.0"),sQuery(id+"F0.wireOp",EDGE,"E1.42.10.0"),sQuery(id+"F0.wireOp",EDGE,"E1.42.11.0"),sQuery(id+"F0.wireOp",EDGE,"E1.42.12.0"),sQuery(id+"F0.wireOp",EDGE,"E1.42.13.0"),sQuery(id+"F0.wireOp",EDGE,"E1.42.14.0"),sQuery(id+"F0.wireOp",EDGE,"E1.42.15.0"),sQuery(id+"F0.wireOp",EDGE,"E1.42.16.0"),sQuery(id+"F0.wireOp",EDGE,"E1.42.17.0"),sQuery(id+"F0.wireOp",EDGE,"E1.42.18.0"),subQ6,sQuery(id+"F0.wireOp",EDGE,"E1.43.1.0"),sQuery(id+"F0.wireOp",EDGE,"E1.43.2.0"),sQuery(id+"F0.wireOp",EDGE,"E1.43.3.0"),sQuery(id+"F0.wireOp",EDGE,"E1.43.4.0"),sQuery(id+"F0.wireOp",EDGE,"E1.43.5.0"),sQuery(id+"F0.wireOp",EDGE,"E1.43.6.0"),sQuery(id+"F0.wireOp",EDGE,"E1.43.7.0"),sQuery(id+"F0.wireOp",EDGE,"E1.43.8.0"),sQuery(id+"F0.wireOp",EDGE,"E1.43.9.0"),sQuery(id+"F0.wireOp",EDGE,"E1.43.10.0"),sQuery(id+"F0.wireOp",EDGE,"E1.43.11.0"),sQuery(id+"F0.wireOp",EDGE,"E1.43.12.0"),sQuery(id+"F0.wireOp",EDGE,"E1.43.13.0"),sQuery(id+"F0.wireOp",EDGE,"E1.43.14.0"),sQuery(id+"F0.wireOp",EDGE,"E1.43.15.0"),sQuery(id+"F0.wireOp",EDGE,"E1.43.16.0"),sQuery(id+"F0.wireOp",EDGE,"E1.43.17.0"),sQuery(id+"F0.wireOp",EDGE,"E1.43.18.0"),subQ5,sQuery(id+"F0.wireOp",EDGE,"E1.44.1.0"),sQuery(id+"F0.wireOp",EDGE,"E1.44.2.0"),sQuery(id+"F0.wireOp",EDGE,"E1.44.3.0"),sQuery(id+"F0.wireOp",EDGE,"E1.44.4.0"),sQuery(id+"F0.wireOp",EDGE,"E1.44.5.0"),sQuery(id+"F0.wireOp",EDGE,"E1.44.6.0"),sQuery(id+"F0.wireOp",EDGE,"E1.44.7.0"),sQuery(id+"F0.wireOp",EDGE,"E1.44.8.0"),sQuery(id+"F0.wireOp",EDGE,"E1.44.9.0"),sQuery(id+"F0.wireOp",EDGE,"E1.44.10.0"),sQuery(id+"F0.wireOp",EDGE,"E1.44.11.0"),sQuery(id+"F0.wireOp",EDGE,"E1.44.12.0"),sQuery(id+"F0.wireOp",EDGE,"E1.44.13.0"),sQuery(id+"F0.wireOp",EDGE,"E1.44.14.0"),sQuery(id+"F0.wireOp",EDGE,"E1.44.15.0"),sQuery(id+"F0.wireOp",EDGE,"E1.44.16.0"),sQuery(id+"F0.wireOp",EDGE,"E1.44.17.0"),sQuery(id+"F0.wireOp",EDGE,"E1.44.18.0"),subQ4,sQuery(id+"F0.wireOp",EDGE,"E1.45.1.0"),sQuery(id+"F0.wireOp",EDGE,"E1.45.2.0"),sQuery(id+"F0.wireOp",EDGE,"E1.45.3.0"),sQuery(id+"F0.wireOp",EDGE,"E1.45.4.0"),sQuery(id+"F0.wireOp",EDGE,"E1.45.5.0"),sQuery(id+"F0.wireOp",EDGE,"E1.45.6.0"),sQuery(id+"F0.wireOp",EDGE,"E1.45.7.0"),sQuery(id+"F0.wireOp",EDGE,"E1.45.8.0"),sQuery(id+"F0.wireOp",EDGE,"E1.45.9.0"),sQuery(id+"F0.wireOp",EDGE,"E1.45.10.0"),sQuery(id+"F0.wireOp",EDGE,"E1.45.11.0"),sQuery(id+"F0.wireOp",EDGE,"E1.45.12.0"),sQuery(id+"F0.wireOp",EDGE,"E1.45.13.0"),sQuery(id+"F0.wireOp",EDGE,"E1.45.14.0"),sQuery(id+"F0.wireOp",EDGE,"E1.45.15.0"),sQuery(id+"F0.wireOp",EDGE,"E1.45.16.0"),sQuery(id+"F0.wireOp",EDGE,"E1.45.17.0"),sQuery(id+"F0.wireOp",EDGE,"E1.45.18.0"),subQ51,sQuery(id+"F0.wireOp",EDGE,"E1.46.1.0"),sQuery(id+"F0.wireOp",EDGE,"E1.46.2.0"),sQuery(id+"F0.wireOp",EDGE,"E1.46.3.0"),sQuery(id+"F0.wireOp",EDGE,"E1.46.4.0"),sQuery(id+"F0.wireOp",EDGE,"E1.46.5.0"),sQuery(id+"F0.wireOp",EDGE,"E1.46.6.0"),sQuery(id+"F0.wireOp",EDGE,"E1.46.7.0"),sQuery(id+"F0.wireOp",EDGE,"E1.46.8.0"),sQuery(id+"F0.wireOp",EDGE,"E1.46.9.0"),sQuery(id+"F0.wireOp",EDGE,"E1.46.10.0"),sQuery(id+"F0.wireOp",EDGE,"E1.46.11.0"),sQuery(id+"F0.wireOp",EDGE,"E1.46.12.0"),sQuery(id+"F0.wireOp",EDGE,"E1.46.13.0"),sQuery(id+"F0.wireOp",EDGE,"E1.46.14.0"),sQuery(id+"F0.wireOp",EDGE,"E1.46.15.0"),sQuery(id+"F0.wireOp",EDGE,"E1.46.16.0"),sQuery(id+"F0.wireOp",EDGE,"E1.46.17.0"),sQuery(id+"F0.wireOp",EDGE,"E1.46.18.0"),subQ52,sQuery(id+"F0.wireOp",EDGE,"E1.47.1.0"),sQuery(id+"F0.wireOp",EDGE,"E1.47.2.0"),sQuery(id+"F0.wireOp",EDGE,"E1.47.3.0"),sQuery(id+"F0.wireOp",EDGE,"E1.47.4.0"),sQuery(id+"F0.wireOp",EDGE,"E1.47.5.0"),sQuery(id+"F0.wireOp",EDGE,"E1.47.6.0"),sQuery(id+"F0.wireOp",EDGE,"E1.47.7.0"),sQuery(id+"F0.wireOp",EDGE,"E1.47.8.0"),sQuery(id+"F0.wireOp",EDGE,"E1.47.9.0"),sQuery(id+"F0.wireOp",EDGE,"E1.47.10.0"),sQuery(id+"F0.wireOp",EDGE,"E1.47.11.0"),sQuery(id+"F0.wireOp",EDGE,"E1.47.12.0"),sQuery(id+"F0.wireOp",EDGE,"E1.47.13.0"),sQuery(id+"F0.wireOp",EDGE,"E1.47.14.0"),sQuery(id+"F0.wireOp",EDGE,"E1.47.15.0"),sQuery(id+"F0.wireOp",EDGE,"E1.47.16.0"),sQuery(id+"F0.wireOp",EDGE,"E1.47.17.0"),sQuery(id+"F0.wireOp",EDGE,"E1.47.18.0"),subQ53,sQuery(id+"F0.wireOp",EDGE,"E1.48.1.0"),sQuery(id+"F0.wireOp",EDGE,"E1.48.2.0"),sQuery(id+"F0.wireOp",EDGE,"E1.48.3.0"),sQuery(id+"F0.wireOp",EDGE,"E1.48.4.0"),sQuery(id+"F0.wireOp",EDGE,"E1.48.5.0"),sQuery(id+"F0.wireOp",EDGE,"E1.48.6.0"),sQuery(id+"F0.wireOp",EDGE,"E1.48.7.0"),sQuery(id+"F0.wireOp",EDGE,"E1.48.8.0"),sQuery(id+"F0.wireOp",EDGE,"E1.48.9.0"),sQuery(id+"F0.wireOp",EDGE,"E1.48.10.0"),sQuery(id+"F0.wireOp",EDGE,"E1.48.11.0"),sQuery(id+"F0.wireOp",EDGE,"E1.48.12.0"),sQuery(id+"F0.wireOp",EDGE,"E1.48.13.0"),sQuery(id+"F0.wireOp",EDGE,"E1.48.14.0"),sQuery(id+"F0.wireOp",EDGE,"E1.48.15.0"),sQuery(id+"F0.wireOp",EDGE,"E1.48.16.0"),sQuery(id+"F0.wireOp",EDGE,"E1.48.17.0"),sQuery(id+"F0.wireOp",EDGE,"E1.48.18.0"),subQ54,sQuery(id+"F0.wireOp",EDGE,"E1.49.1.0"),sQuery(id+"F0.wireOp",EDGE,"E1.49.2.0"),sQuery(id+"F0.wireOp",EDGE,"E1.49.3.0"),sQuery(id+"F0.wireOp",EDGE,"E1.49.4.0"),sQuery(id+"F0.wireOp",EDGE,"E1.49.5.0"),sQuery(id+"F0.wireOp",EDGE,"E1.49.6.0"),sQuery(id+"F0.wireOp",EDGE,"E1.49.7.0"),sQuery(id+"F0.wireOp",EDGE,"E1.49.8.0"),sQuery(id+"F0.wireOp",EDGE,"E1.49.9.0"),sQuery(id+"F0.wireOp",EDGE,"E1.49.10.0"),sQuery(id+"F0.wireOp",EDGE,"E1.49.11.0"),sQuery(id+"F0.wireOp",EDGE,"E1.49.12.0"),sQuery(id+"F0.wireOp",EDGE,"E1.49.13.0"),sQuery(id+"F0.wireOp",EDGE,"E1.49.14.0"),sQuery(id+"F0.wireOp",EDGE,"E1.49.15.0"),sQuery(id+"F0.wireOp",EDGE,"E1.49.16.0"),sQuery(id+"F0.wireOp",EDGE,"E1.49.17.0"),sQuery(id+"F0.wireOp",EDGE,"E1.49.18.0"),subQ55,sQuery(id+"F0.wireOp",EDGE,"E1.50.1.0"),sQuery(id+"F0.wireOp",EDGE,"E1.50.2.0"),sQuery(id+"F0.wireOp",EDGE,"E1.50.3.0"),sQuery(id+"F0.wireOp",EDGE,"E1.50.4.0"),sQuery(id+"F0.wireOp",EDGE,"E1.50.5.0"),sQuery(id+"F0.wireOp",EDGE,"E1.50.6.0"),sQuery(id+"F0.wireOp",EDGE,"E1.50.7.0"),sQuery(id+"F0.wireOp",EDGE,"E1.50.8.0"),sQuery(id+"F0.wireOp",EDGE,"E1.50.9.0"),sQuery(id+"F0.wireOp",EDGE,"E1.50.10.0"),sQuery(id+"F0.wireOp",EDGE,"E1.50.11.0"),sQuery(id+"F0.wireOp",EDGE,"E1.50.12.0"),sQuery(id+"F0.wireOp",EDGE,"E1.50.13.0"),sQuery(id+"F0.wireOp",EDGE,"E1.50.14.0"),sQuery(id+"F0.wireOp",EDGE,"E1.50.15.0"),sQuery(id+"F0.wireOp",EDGE,"E1.50.16.0"),sQuery(id+"F0.wireOp",EDGE,"E1.50.17.0"),sQuery(id+"F0.wireOp",EDGE,"E1.50.18.0"),subQ56,sQuery(id+"F0.wireOp",EDGE,"E1.51.1.0"),sQuery(id+"F0.wireOp",EDGE,"E1.51.2.0"),sQuery(id+"F0.wireOp",EDGE,"E1.51.3.0"),sQuery(id+"F0.wireOp",EDGE,"E1.51.4.0"),sQuery(id+"F0.wireOp",EDGE,"E1.51.5.0"),sQuery(id+"F0.wireOp",EDGE,"E1.51.6.0"),sQuery(id+"F0.wireOp",EDGE,"E1.51.7.0"),sQuery(id+"F0.wireOp",EDGE,"E1.51.8.0"),sQuery(id+"F0.wireOp",EDGE,"E1.51.9.0"),sQuery(id+"F0.wireOp",EDGE,"E1.51.10.0"),sQuery(id+"F0.wireOp",EDGE,"E1.51.11.0"),sQuery(id+"F0.wireOp",EDGE,"E1.51.12.0"),sQuery(id+"F0.wireOp",EDGE,"E1.51.13.0"),sQuery(id+"F0.wireOp",EDGE,"E1.51.14.0"),sQuery(id+"F0.wireOp",EDGE,"E1.51.15.0"),sQuery(id+"F0.wireOp",EDGE,"E1.51.16.0"),sQuery(id+"F0.wireOp",EDGE,"E1.51.17.0"),sQuery(id+"F0.wireOp",EDGE,"E1.51.18.0"),subQ57,sQuery(id+"F0.wireOp",EDGE,"E1.52.1.0"),sQuery(id+"F0.wireOp",EDGE,"E1.52.2.0"),sQuery(id+"F0.wireOp",EDGE,"E1.52.3.0"),sQuery(id+"F0.wireOp",EDGE,"E1.52.4.0"),sQuery(id+"F0.wireOp",EDGE,"E1.52.5.0"),sQuery(id+"F0.wireOp",EDGE,"E1.52.6.0"),sQuery(id+"F0.wireOp",EDGE,"E1.52.7.0"),sQuery(id+"F0.wireOp",EDGE,"E1.52.8.0"),sQuery(id+"F0.wireOp",EDGE,"E1.52.9.0"),sQuery(id+"F0.wireOp",EDGE,"E1.52.10.0"),sQuery(id+"F0.wireOp",EDGE,"E1.52.11.0"),sQuery(id+"F0.wireOp",EDGE,"E1.52.12.0"),sQuery(id+"F0.wireOp",EDGE,"E1.52.13.0"),sQuery(id+"F0.wireOp",EDGE,"E1.52.14.0"),sQuery(id+"F0.wireOp",EDGE,"E1.52.15.0"),sQuery(id+"F0.wireOp",EDGE,"E1.52.16.0"),sQuery(id+"F0.wireOp",EDGE,"E1.52.17.0"),sQuery(id+"F0.wireOp",EDGE,"E1.52.18.0"),subQ58,sQuery(id+"F0.wireOp",EDGE,"E1.53.1.0"),sQuery(id+"F0.wireOp",EDGE,"E1.53.2.0"),sQuery(id+"F0.wireOp",EDGE,"E1.53.3.0"),sQuery(id+"F0.wireOp",EDGE,"E1.53.4.0"),sQuery(id+"F0.wireOp",EDGE,"E1.53.5.0"),sQuery(id+"F0.wireOp",EDGE,"E1.53.6.0"),sQuery(id+"F0.wireOp",EDGE,"E1.53.7.0"),sQuery(id+"F0.wireOp",EDGE,"E1.53.8.0"),sQuery(id+"F0.wireOp",EDGE,"E1.53.9.0"),sQuery(id+"F0.wireOp",EDGE,"E1.53.10.0"),sQuery(id+"F0.wireOp",EDGE,"E1.53.11.0"),sQuery(id+"F0.wireOp",EDGE,"E1.53.12.0"),sQuery(id+"F0.wireOp",EDGE,"E1.53.13.0"),sQuery(id+"F0.wireOp",EDGE,"E1.53.14.0"),sQuery(id+"F0.wireOp",EDGE,"E1.53.15.0"),sQuery(id+"F0.wireOp",EDGE,"E1.53.16.0"),sQuery(id+"F0.wireOp",EDGE,"E1.53.17.0"),sQuery(id+"F0.wireOp",EDGE,"E1.53.18.0"),subQ59,sQuery(id+"F0.wireOp",EDGE,"E1.54.1.0"),sQuery(id+"F0.wireOp",EDGE,"E1.54.2.0"),sQuery(id+"F0.wireOp",EDGE,"E1.54.3.0"),sQuery(id+"F0.wireOp",EDGE,"E1.54.4.0"),sQuery(id+"F0.wireOp",EDGE,"E1.54.5.0"),sQuery(id+"F0.wireOp",EDGE,"E1.54.6.0"),sQuery(id+"F0.wireOp",EDGE,"E1.54.7.0"),sQuery(id+"F0.wireOp",EDGE,"E1.54.8.0"),sQuery(id+"F0.wireOp",EDGE,"E1.54.9.0"),sQuery(id+"F0.wireOp",EDGE,"E1.54.10.0"),sQuery(id+"F0.wireOp",EDGE,"E1.54.11.0"),sQuery(id+"F0.wireOp",EDGE,"E1.54.12.0"),sQuery(id+"F0.wireOp",EDGE,"E1.54.13.0"),sQuery(id+"F0.wireOp",EDGE,"E1.54.14.0"),sQuery(id+"F0.wireOp",EDGE,"E1.54.15.0"),sQuery(id+"F0.wireOp",EDGE,"E1.54.16.0"),sQuery(id+"F0.wireOp",EDGE,"E1.54.17.0"),sQuery(id+"F0.wireOp",EDGE,"E1.54.18.0"),subQ60,sQuery(id+"F0.wireOp",EDGE,"E1.55.1.0"),sQuery(id+"F0.wireOp",EDGE,"E1.55.2.0"),sQuery(id+"F0.wireOp",EDGE,"E1.55.3.0"),sQuery(id+"F0.wireOp",EDGE,"E1.55.4.0"),sQuery(id+"F0.wireOp",EDGE,"E1.55.5.0"),sQuery(id+"F0.wireOp",EDGE,"E1.55.6.0"),sQuery(id+"F0.wireOp",EDGE,"E1.55.7.0"),sQuery(id+"F0.wireOp",EDGE,"E1.55.8.0"),sQuery(id+"F0.wireOp",EDGE,"E1.55.9.0"),sQuery(id+"F0.wireOp",EDGE,"E1.55.10.0"),sQuery(id+"F0.wireOp",EDGE,"E1.55.11.0"),sQuery(id+"F0.wireOp",EDGE,"E1.55.12.0"),sQuery(id+"F0.wireOp",EDGE,"E1.55.13.0"),sQuery(id+"F0.wireOp",EDGE,"E1.55.14.0"),sQuery(id+"F0.wireOp",EDGE,"E1.55.15.0"),sQuery(id+"F0.wireOp",EDGE,"E1.55.16.0"),sQuery(id+"F0.wireOp",EDGE,"E1.55.17.0"),sQuery(id+"F0.wireOp",EDGE,"E1.55.18.0"),subQ61,sQuery(id+"F0.wireOp",EDGE,"E1.56.1.0"),sQuery(id+"F0.wireOp",EDGE,"E1.56.2.0"),sQuery(id+"F0.wireOp",EDGE,"E1.56.3.0"),sQuery(id+"F0.wireOp",EDGE,"E1.56.4.0"),sQuery(id+"F0.wireOp",EDGE,"E1.56.5.0"),sQuery(id+"F0.wireOp",EDGE,"E1.56.6.0"),sQuery(id+"F0.wireOp",EDGE,"E1.56.7.0"),sQuery(id+"F0.wireOp",EDGE,"E1.56.8.0"),sQuery(id+"F0.wireOp",EDGE,"E1.56.9.0"),sQuery(id+"F0.wireOp",EDGE,"E1.56.10.0"),sQuery(id+"F0.wireOp",EDGE,"E1.56.11.0"),sQuery(id+"F0.wireOp",EDGE,"E1.56.12.0"),sQuery(id+"F0.wireOp",EDGE,"E1.56.13.0"),sQuery(id+"F0.wireOp",EDGE,"E1.56.14.0"),sQuery(id+"F0.wireOp",EDGE,"E1.56.15.0"),sQuery(id+"F0.wireOp",EDGE,"E1.56.16.0"),sQuery(id+"F0.wireOp",EDGE,"E1.56.17.0"),sQuery(id+"F0.wireOp",EDGE,"E1.56.18.0"),subQ62,sQuery(id+"F0.wireOp",EDGE,"E1.57.1.0"),sQuery(id+"F0.wireOp",EDGE,"E1.57.2.0"),sQuery(id+"F0.wireOp",EDGE,"E1.57.3.0"),sQuery(id+"F0.wireOp",EDGE,"E1.57.4.0"),sQuery(id+"F0.wireOp",EDGE,"E1.57.5.0"),sQuery(id+"F0.wireOp",EDGE,"E1.57.6.0"),sQuery(id+"F0.wireOp",EDGE,"E1.57.7.0"),sQuery(id+"F0.wireOp",EDGE,"E1.57.8.0"),sQuery(id+"F0.wireOp",EDGE,"E1.57.9.0"),sQuery(id+"F0.wireOp",EDGE,"E1.57.10.0"),sQuery(id+"F0.wireOp",EDGE,"E1.57.11.0"),sQuery(id+"F0.wireOp",EDGE,"E1.57.12.0"),sQuery(id+"F0.wireOp",EDGE,"E1.57.13.0"),sQuery(id+"F0.wireOp",EDGE,"E1.57.14.0"),sQuery(id+"F0.wireOp",EDGE,"E1.57.15.0"),sQuery(id+"F0.wireOp",EDGE,"E1.57.16.0"),sQuery(id+"F0.wireOp",EDGE,"E1.57.17.0"),sQuery(id+"F0.wireOp",EDGE,"E1.57.18.0"),subQ63,sQuery(id+"F0.wireOp",EDGE,"E1.58.1.0"),sQuery(id+"F0.wireOp",EDGE,"E1.58.2.0"),sQuery(id+"F0.wireOp",EDGE,"E1.58.3.0"),sQuery(id+"F0.wireOp",EDGE,"E1.58.4.0"),sQuery(id+"F0.wireOp",EDGE,"E1.58.5.0"),sQuery(id+"F0.wireOp",EDGE,"E1.58.6.0"),sQuery(id+"F0.wireOp",EDGE,"E1.58.7.0"),sQuery(id+"F0.wireOp",EDGE,"E1.58.8.0"),sQuery(id+"F0.wireOp",EDGE,"E1.58.9.0"),sQuery(id+"F0.wireOp",EDGE,"E1.58.10.0"),sQuery(id+"F0.wireOp",EDGE,"E1.58.11.0"),sQuery(id+"F0.wireOp",EDGE,"E1.58.12.0"),sQuery(id+"F0.wireOp",EDGE,"E1.58.13.0"),sQuery(id+"F0.wireOp",EDGE,"E1.58.14.0"),sQuery(id+"F0.wireOp",EDGE,"E1.58.15.0"),sQuery(id+"F0.wireOp",EDGE,"E1.58.16.0"),sQuery(id+"F0.wireOp",EDGE,"E1.58.17.0"),sQuery(id+"F0.wireOp",EDGE,"E1.58.18.0"),subQ64,sQuery(id+"F0.wireOp",EDGE,"E1.59.1.0"),sQuery(id+"F0.wireOp",EDGE,"E1.59.2.0"),sQuery(id+"F0.wireOp",EDGE,"E1.59.3.0"),sQuery(id+"F0.wireOp",EDGE,"E1.59.4.0"),sQuery(id+"F0.wireOp",EDGE,"E1.59.5.0"),sQuery(id+"F0.wireOp",EDGE,"E1.59.6.0"),sQuery(id+"F0.wireOp",EDGE,"E1.59.7.0"),sQuery(id+"F0.wireOp",EDGE,"E1.59.8.0"),sQuery(id+"F0.wireOp",EDGE,"E1.59.9.0"),sQuery(id+"F0.wireOp",EDGE,"E1.59.10.0"),sQuery(id+"F0.wireOp",EDGE,"E1.59.11.0"),sQuery(id+"F0.wireOp",EDGE,"E1.59.12.0"),sQuery(id+"F0.wireOp",EDGE,"E1.59.13.0"),sQuery(id+"F0.wireOp",EDGE,"E1.59.14.0"),sQuery(id+"F0.wireOp",EDGE,"E1.59.15.0"),sQuery(id+"F0.wireOp",EDGE,"E1.59.16.0"),sQuery(id+"F0.wireOp",EDGE,"E1.59.17.0"),sQuery(id+"F0.wireOp",EDGE,"E1.59.18.0"),subQ65,sQuery(id+"F0.wireOp",EDGE,"E1.60.1.0"),sQuery(id+"F0.wireOp",EDGE,"E1.60.2.0"),sQuery(id+"F0.wireOp",EDGE,"E1.60.3.0"),sQuery(id+"F0.wireOp",EDGE,"E1.60.4.0"),sQuery(id+"F0.wireOp",EDGE,"E1.60.5.0"),sQuery(id+"F0.wireOp",EDGE,"E1.60.6.0"),sQuery(id+"F0.wireOp",EDGE,"E1.60.7.0"),sQuery(id+"F0.wireOp",EDGE,"E1.60.8.0"),sQuery(id+"F0.wireOp",EDGE,"E1.60.9.0"),sQuery(id+"F0.wireOp",EDGE,"E1.60.10.0"),sQuery(id+"F0.wireOp",EDGE,"E1.60.11.0"),sQuery(id+"F0.wireOp",EDGE,"E1.60.12.0"),sQuery(id+"F0.wireOp",EDGE,"E1.60.13.0"),sQuery(id+"F0.wireOp",EDGE,"E1.60.14.0"),sQuery(id+"F0.wireOp",EDGE,"E1.60.15.0"),sQuery(id+"F0.wireOp",EDGE,"E1.60.16.0"),sQuery(id+"F0.wireOp",EDGE,"E1.60.17.0"),sQuery(id+"F0.wireOp",EDGE,"E1.60.18.0"),subQ66,sQuery(id+"F0.wireOp",EDGE,"E1.61.1.0"),sQuery(id+"F0.wireOp",EDGE,"E1.61.2.0"),sQuery(id+"F0.wireOp",EDGE,"E1.61.3.0"),sQuery(id+"F0.wireOp",EDGE,"E1.61.4.0"),sQuery(id+"F0.wireOp",EDGE,"E1.61.5.0"),sQuery(id+"F0.wireOp",EDGE,"E1.61.6.0"),sQuery(id+"F0.wireOp",EDGE,"E1.61.7.0"),sQuery(id+"F0.wireOp",EDGE,"E1.61.8.0"),sQuery(id+"F0.wireOp",EDGE,"E1.61.9.0"),sQuery(id+"F0.wireOp",EDGE,"E1.61.10.0"),sQuery(id+"F0.wireOp",EDGE,"E1.61.11.0"),sQuery(id+"F0.wireOp",EDGE,"E1.61.12.0"),sQuery(id+"F0.wireOp",EDGE,"E1.61.13.0"),sQuery(id+"F0.wireOp",EDGE,"E1.61.14.0"),sQuery(id+"F0.wireOp",EDGE,"E1.61.15.0"),sQuery(id+"F0.wireOp",EDGE,"E1.61.16.0"),sQuery(id+"F0.wireOp",EDGE,"E1.61.17.0"),sQuery(id+"F0.wireOp",EDGE,"E1.61.18.0"),subQ67,sQuery(id+"F0.wireOp",EDGE,"E1.62.1.0"),sQuery(id+"F0.wireOp",EDGE,"E1.62.2.0"),sQuery(id+"F0.wireOp",EDGE,"E1.62.3.0"),sQuery(id+"F0.wireOp",EDGE,"E1.62.4.0"),sQuery(id+"F0.wireOp",EDGE,"E1.62.5.0"),sQuery(id+"F0.wireOp",EDGE,"E1.62.6.0"),sQuery(id+"F0.wireOp",EDGE,"E1.62.7.0"),sQuery(id+"F0.wireOp",EDGE,"E1.62.8.0"),sQuery(id+"F0.wireOp",EDGE,"E1.62.9.0"),sQuery(id+"F0.wireOp",EDGE,"E1.62.10.0"),sQuery(id+"F0.wireOp",EDGE,"E1.62.11.0"),sQuery(id+"F0.wireOp",EDGE,"E1.62.12.0"),sQuery(id+"F0.wireOp",EDGE,"E1.62.13.0"),sQuery(id+"F0.wireOp",EDGE,"E1.62.14.0"),sQuery(id+"F0.wireOp",EDGE,"E1.62.15.0"),sQuery(id+"F0.wireOp",EDGE,"E1.62.16.0"),sQuery(id+"F0.wireOp",EDGE,"E1.62.17.0"),sQuery(id+"F0.wireOp",EDGE,"E1.62.18.0"),subQ68,sQuery(id+"F0.wireOp",EDGE,"E1.63.1.0"),sQuery(id+"F0.wireOp",EDGE,"E1.63.2.0"),sQuery(id+"F0.wireOp",EDGE,"E1.63.3.0"),sQuery(id+"F0.wireOp",EDGE,"E1.63.4.0"),sQuery(id+"F0.wireOp",EDGE,"E1.63.5.0"),sQuery(id+"F0.wireOp",EDGE,"E1.63.6.0"),sQuery(id+"F0.wireOp",EDGE,"E1.63.7.0"),sQuery(id+"F0.wireOp",EDGE,"E1.63.8.0"),sQuery(id+"F0.wireOp",EDGE,"E1.63.9.0"),sQuery(id+"F0.wireOp",EDGE,"E1.63.10.0"),sQuery(id+"F0.wireOp",EDGE,"E1.63.11.0"),sQuery(id+"F0.wireOp",EDGE,"E1.63.12.0"),sQuery(id+"F0.wireOp",EDGE,"E1.63.13.0"),sQuery(id+"F0.wireOp",EDGE,"E1.63.14.0"),sQuery(id+"F0.wireOp",EDGE,"E1.63.15.0"),sQuery(id+"F0.wireOp",EDGE,"E1.63.16.0"),sQuery(id+"F0.wireOp",EDGE,"E1.63.17.0"),sQuery(id+"F0.wireOp",EDGE,"E1.63.18.0"),subQ69,sQuery(id+"F0.wireOp",EDGE,"E1.64.1.0"),sQuery(id+"F0.wireOp",EDGE,"E1.64.2.0"),sQuery(id+"F0.wireOp",EDGE,"E1.64.3.0"),sQuery(id+"F0.wireOp",EDGE,"E1.64.4.0"),sQuery(id+"F0.wireOp",EDGE,"E1.64.5.0"),sQuery(id+"F0.wireOp",EDGE,"E1.64.6.0"),sQuery(id+"F0.wireOp",EDGE,"E1.64.7.0"),sQuery(id+"F0.wireOp",EDGE,"E1.64.8.0"),sQuery(id+"F0.wireOp",EDGE,"E1.64.9.0"),sQuery(id+"F0.wireOp",EDGE,"E1.64.10.0"),sQuery(id+"F0.wireOp",EDGE,"E1.64.11.0"),sQuery(id+"F0.wireOp",EDGE,"E1.64.12.0"),sQuery(id+"F0.wireOp",EDGE,"E1.64.13.0"),sQuery(id+"F0.wireOp",EDGE,"E1.64.14.0"),sQuery(id+"F0.wireOp",EDGE,"E1.64.15.0"),sQuery(id+"F0.wireOp",EDGE,"E1.64.16.0"),sQuery(id+"F0.wireOp",EDGE,"E1.64.17.0"),sQuery(id+"F0.wireOp",EDGE,"E1.64.18.0"),subQ70,sQuery(id+"F0.wireOp",EDGE,"E1.65.1.0"),sQuery(id+"F0.wireOp",EDGE,"E1.65.2.0"),sQuery(id+"F0.wireOp",EDGE,"E1.65.3.0"),sQuery(id+"F0.wireOp",EDGE,"E1.65.4.0"),sQuery(id+"F0.wireOp",EDGE,"E1.65.5.0"),sQuery(id+"F0.wireOp",EDGE,"E1.65.6.0"),sQuery(id+"F0.wireOp",EDGE,"E1.65.7.0"),sQuery(id+"F0.wireOp",EDGE,"E1.65.8.0"),sQuery(id+"F0.wireOp",EDGE,"E1.65.9.0"),sQuery(id+"F0.wireOp",EDGE,"E1.65.10.0"),sQuery(id+"F0.wireOp",EDGE,"E1.65.11.0"),sQuery(id+"F0.wireOp",EDGE,"E1.65.12.0"),sQuery(id+"F0.wireOp",EDGE,"E1.65.13.0"),sQuery(id+"F0.wireOp",EDGE,"E1.65.14.0"),sQuery(id+"F0.wireOp",EDGE,"E1.65.15.0"),sQuery(id+"F0.wireOp",EDGE,"E1.65.16.0"),sQuery(id+"F0.wireOp",EDGE,"E1.65.17.0"),sQuery(id+"F0.wireOp",EDGE,"E1.65.18.0"),subQ71,sQuery(id+"F0.wireOp",EDGE,"E1.66.1.0"),sQuery(id+"F0.wireOp",EDGE,"E1.66.2.0"),sQuery(id+"F0.wireOp",EDGE,"E1.66.3.0"),sQuery(id+"F0.wireOp",EDGE,"E1.66.4.0"),sQuery(id+"F0.wireOp",EDGE,"E1.66.5.0"),sQuery(id+"F0.wireOp",EDGE,"E1.66.6.0"),sQuery(id+"F0.wireOp",EDGE,"E1.66.7.0"),sQuery(id+"F0.wireOp",EDGE,"E1.66.8.0"),sQuery(id+"F0.wireOp",EDGE,"E1.66.9.0"),sQuery(id+"F0.wireOp",EDGE,"E1.66.10.0"),sQuery(id+"F0.wireOp",EDGE,"E1.66.11.0"),sQuery(id+"F0.wireOp",EDGE,"E1.66.12.0"),sQuery(id+"F0.wireOp",EDGE,"E1.66.13.0"),sQuery(id+"F0.wireOp",EDGE,"E1.66.14.0"),sQuery(id+"F0.wireOp",EDGE,"E1.66.15.0"),sQuery(id+"F0.wireOp",EDGE,"E1.66.16.0"),sQuery(id+"F0.wireOp",EDGE,"E1.66.17.0"),sQuery(id+"F0.wireOp",EDGE,"E1.66.18.0"),subQ72,sQuery(id+"F0.wireOp",EDGE,"E1.67.1.0"),sQuery(id+"F0.wireOp",EDGE,"E1.67.2.0"),sQuery(id+"F0.wireOp",EDGE,"E1.67.3.0"),sQuery(id+"F0.wireOp",EDGE,"E1.67.4.0"),sQuery(id+"F0.wireOp",EDGE,"E1.67.5.0"),sQuery(id+"F0.wireOp",EDGE,"E1.67.6.0"),sQuery(id+"F0.wireOp",EDGE,"E1.67.7.0"),sQuery(id+"F0.wireOp",EDGE,"E1.67.8.0"),sQuery(id+"F0.wireOp",EDGE,"E1.67.9.0"),sQuery(id+"F0.wireOp",EDGE,"E1.67.10.0"),sQuery(id+"F0.wireOp",EDGE,"E1.67.11.0"),sQuery(id+"F0.wireOp",EDGE,"E1.67.12.0"),sQuery(id+"F0.wireOp",EDGE,"E1.67.13.0"),sQuery(id+"F0.wireOp",EDGE,"E1.67.14.0"),sQuery(id+"F0.wireOp",EDGE,"E1.67.15.0"),sQuery(id+"F0.wireOp",EDGE,"E1.67.16.0"),sQuery(id+"F0.wireOp",EDGE,"E1.67.17.0"),sQuery(id+"F0.wireOp",EDGE,"E1.67.18.0"),subQ73,sQuery(id+"F0.wireOp",EDGE,"E1.68.1.0"),sQuery(id+"F0.wireOp",EDGE,"E1.68.2.0"),sQuery(id+"F0.wireOp",EDGE,"E1.68.3.0"),sQuery(id+"F0.wireOp",EDGE,"E1.68.4.0"),sQuery(id+"F0.wireOp",EDGE,"E1.68.5.0"),sQuery(id+"F0.wireOp",EDGE,"E1.68.6.0"),sQuery(id+"F0.wireOp",EDGE,"E1.68.7.0"),sQuery(id+"F0.wireOp",EDGE,"E1.68.8.0"),sQuery(id+"F0.wireOp",EDGE,"E1.68.9.0"),sQuery(id+"F0.wireOp",EDGE,"E1.68.10.0"),sQuery(id+"F0.wireOp",EDGE,"E1.68.11.0"),sQuery(id+"F0.wireOp",EDGE,"E1.68.12.0"),sQuery(id+"F0.wireOp",EDGE,"E1.68.13.0"),sQuery(id+"F0.wireOp",EDGE,"E1.68.14.0"),sQuery(id+"F0.wireOp",EDGE,"E1.68.15.0"),sQuery(id+"F0.wireOp",EDGE,"E1.68.16.0"),sQuery(id+"F0.wireOp",EDGE,"E1.68.17.0"),sQuery(id+"F0.wireOp",EDGE,"E1.68.18.0"),subQ74,sQuery(id+"F0.wireOp",EDGE,"E1.69.1.0"),sQuery(id+"F0.wireOp",EDGE,"E1.69.2.0"),sQuery(id+"F0.wireOp",EDGE,"E1.69.3.0"),sQuery(id+"F0.wireOp",EDGE,"E1.69.4.0"),sQuery(id+"F0.wireOp",EDGE,"E1.69.5.0"),sQuery(id+"F0.wireOp",EDGE,"E1.69.6.0"),sQuery(id+"F0.wireOp",EDGE,"E1.69.7.0"),sQuery(id+"F0.wireOp",EDGE,"E1.69.8.0"),sQuery(id+"F0.wireOp",EDGE,"E1.69.9.0"),sQuery(id+"F0.wireOp",EDGE,"E1.69.10.0"),sQuery(id+"F0.wireOp",EDGE,"E1.69.11.0"),sQuery(id+"F0.wireOp",EDGE,"E1.69.12.0"),sQuery(id+"F0.wireOp",EDGE,"E1.69.13.0"),sQuery(id+"F0.wireOp",EDGE,"E1.69.14.0"),sQuery(id+"F0.wireOp",EDGE,"E1.69.15.0"),sQuery(id+"F0.wireOp",EDGE,"E1.69.16.0"),sQuery(id+"F0.wireOp",EDGE,"E1.69.17.0"),sQuery(id+"F0.wireOp",EDGE,"E1.69.18.0"),subQ75,sQuery(id+"F0.wireOp",EDGE,"E1.70.1.0"),sQuery(id+"F0.wireOp",EDGE,"E1.70.2.0"),sQuery(id+"F0.wireOp",EDGE,"E1.70.3.0"),sQuery(id+"F0.wireOp",EDGE,"E1.70.4.0"),sQuery(id+"F0.wireOp",EDGE,"E1.70.5.0"),sQuery(id+"F0.wireOp",EDGE,"E1.70.6.0"),sQuery(id+"F0.wireOp",EDGE,"E1.70.7.0"),sQuery(id+"F0.wireOp",EDGE,"E1.70.8.0"),sQuery(id+"F0.wireOp",EDGE,"E1.70.9.0"),sQuery(id+"F0.wireOp",EDGE,"E1.70.10.0"),sQuery(id+"F0.wireOp",EDGE,"E1.70.11.0"),sQuery(id+"F0.wireOp",EDGE,"E1.70.12.0"),sQuery(id+"F0.wireOp",EDGE,"E1.70.13.0"),sQuery(id+"F0.wireOp",EDGE,"E1.70.14.0"),sQuery(id+"F0.wireOp",EDGE,"E1.70.15.0"),sQuery(id+"F0.wireOp",EDGE,"E1.70.16.0"),sQuery(id+"F0.wireOp",EDGE,"E1.70.17.0"),sQuery(id+"F0.wireOp",EDGE,"E1.70.18.0"),subQ76,sQuery(id+"F0.wireOp",EDGE,"E1.71.1.0"),sQuery(id+"F0.wireOp",EDGE,"E1.71.2.0"),sQuery(id+"F0.wireOp",EDGE,"E1.71.3.0"),sQuery(id+"F0.wireOp",EDGE,"E1.71.4.0"),sQuery(id+"F0.wireOp",EDGE,"E1.71.5.0"),sQuery(id+"F0.wireOp",EDGE,"E1.71.6.0"),sQuery(id+"F0.wireOp",EDGE,"E1.71.7.0"),sQuery(id+"F0.wireOp",EDGE,"E1.71.8.0"),sQuery(id+"F0.wireOp",EDGE,"E1.71.9.0"),sQuery(id+"F0.wireOp",EDGE,"E1.71.10.0"),sQuery(id+"F0.wireOp",EDGE,"E1.71.11.0"),sQuery(id+"F0.wireOp",EDGE,"E1.71.12.0"),sQuery(id+"F0.wireOp",EDGE,"E1.71.13.0"),sQuery(id+"F0.wireOp",EDGE,"E1.71.14.0"),sQuery(id+"F0.wireOp",EDGE,"E1.71.15.0"),sQuery(id+"F0.wireOp",EDGE,"E1.71.16.0"),sQuery(id+"F0.wireOp",EDGE,"E1.71.17.0"),sQuery(id+"F0.wireOp",EDGE,"E1.71.18.0"),subQ77,sQuery(id+"F0.wireOp",EDGE,"E1.72.1.0"),sQuery(id+"F0.wireOp",EDGE,"E1.72.2.0"),sQuery(id+"F0.wireOp",EDGE,"E1.72.3.0"),sQuery(id+"F0.wireOp",EDGE,"E1.72.4.0"),sQuery(id+"F0.wireOp",EDGE,"E1.72.5.0"),sQuery(id+"F0.wireOp",EDGE,"E1.72.6.0"),sQuery(id+"F0.wireOp",EDGE,"E1.72.7.0"),sQuery(id+"F0.wireOp",EDGE,"E1.72.8.0"),sQuery(id+"F0.wireOp",EDGE,"E1.72.9.0"),sQuery(id+"F0.wireOp",EDGE,"E1.72.10.0"),sQuery(id+"F0.wireOp",EDGE,"E1.72.11.0"),sQuery(id+"F0.wireOp",EDGE,"E1.72.12.0"),sQuery(id+"F0.wireOp",EDGE,"E1.72.13.0"),sQuery(id+"F0.wireOp",EDGE,"E1.72.14.0"),sQuery(id+"F0.wireOp",EDGE,"E1.72.15.0"),sQuery(id+"F0.wireOp",EDGE,"E1.72.16.0"),sQuery(id+"F0.wireOp",EDGE,"E1.72.17.0"),sQuery(id+"F0.wireOp",EDGE,"E1.72.18.0"),subQ78,sQuery(id+"F0.wireOp",EDGE,"E1.73.1.0"),sQuery(id+"F0.wireOp",EDGE,"E1.73.2.0"),sQuery(id+"F0.wireOp",EDGE,"E1.73.3.0"),sQuery(id+"F0.wireOp",EDGE,"E1.73.4.0"),sQuery(id+"F0.wireOp",EDGE,"E1.73.5.0"),sQuery(id+"F0.wireOp",EDGE,"E1.73.6.0"),sQuery(id+"F0.wireOp",EDGE,"E1.73.7.0"),sQuery(id+"F0.wireOp",EDGE,"E1.73.8.0"),sQuery(id+"F0.wireOp",EDGE,"E1.73.9.0"),sQuery(id+"F0.wireOp",EDGE,"E1.73.10.0"),sQuery(id+"F0.wireOp",EDGE,"E1.73.11.0"),sQuery(id+"F0.wireOp",EDGE,"E1.73.12.0"),sQuery(id+"F0.wireOp",EDGE,"E1.73.13.0"),sQuery(id+"F0.wireOp",EDGE,"E1.73.14.0"),sQuery(id+"F0.wireOp",EDGE,"E1.73.15.0"),sQuery(id+"F0.wireOp",EDGE,"E1.73.16.0"),sQuery(id+"F0.wireOp",EDGE,"E1.73.17.0"),sQuery(id+"F0.wireOp",EDGE,"E1.73.18.0"),subQ79,sQuery(id+"F0.wireOp",EDGE,"E1.74.1.0"),sQuery(id+"F0.wireOp",EDGE,"E1.74.2.0"),sQuery(id+"F0.wireOp",EDGE,"E1.74.3.0"),sQuery(id+"F0.wireOp",EDGE,"E1.74.4.0"),sQuery(id+"F0.wireOp",EDGE,"E1.74.5.0"),sQuery(id+"F0.wireOp",EDGE,"E1.74.6.0"),sQuery(id+"F0.wireOp",EDGE,"E1.74.7.0"),sQuery(id+"F0.wireOp",EDGE,"E1.74.8.0"),sQuery(id+"F0.wireOp",EDGE,"E1.74.9.0"),sQuery(id+"F0.wireOp",EDGE,"E1.74.10.0"),sQuery(id+"F0.wireOp",EDGE,"E1.74.11.0"),sQuery(id+"F0.wireOp",EDGE,"E1.74.12.0"),sQuery(id+"F0.wireOp",EDGE,"E1.74.13.0"),sQuery(id+"F0.wireOp",EDGE,"E1.74.14.0"),sQuery(id+"F0.wireOp",EDGE,"E1.74.15.0"),sQuery(id+"F0.wireOp",EDGE,"E1.74.16.0"),sQuery(id+"F0.wireOp",EDGE,"E1.74.17.0"),sQuery(id+"F0.wireOp",EDGE,"E1.74.18.0"),subQ80,sQuery(id+"F0.wireOp",EDGE,"E1.75.1.0"),sQuery(id+"F0.wireOp",EDGE,"E1.75.2.0"),sQuery(id+"F0.wireOp",EDGE,"E1.75.3.0"),sQuery(id+"F0.wireOp",EDGE,"E1.75.4.0"),sQuery(id+"F0.wireOp",EDGE,"E1.75.5.0"),sQuery(id+"F0.wireOp",EDGE,"E1.75.6.0"),sQuery(id+"F0.wireOp",EDGE,"E1.75.7.0"),sQuery(id+"F0.wireOp",EDGE,"E1.75.8.0"),sQuery(id+"F0.wireOp",EDGE,"E1.75.9.0"),sQuery(id+"F0.wireOp",EDGE,"E1.75.10.0"),sQuery(id+"F0.wireOp",EDGE,"E1.75.11.0"),sQuery(id+"F0.wireOp",EDGE,"E1.75.12.0"),sQuery(id+"F0.wireOp",EDGE,"E1.75.13.0"),sQuery(id+"F0.wireOp",EDGE,"E1.75.14.0"),sQuery(id+"F0.wireOp",EDGE,"E1.75.15.0"),sQuery(id+"F0.wireOp",EDGE,"E1.75.16.0"),sQuery(id+"F0.wireOp",EDGE,"E1.75.17.0"),sQuery(id+"F0.wireOp",EDGE,"E1.75.18.0"),subQ81,sQuery(id+"F0.wireOp",EDGE,"E1.76.1.0"),sQuery(id+"F0.wireOp",EDGE,"E1.76.2.0"),sQuery(id+"F0.wireOp",EDGE,"E1.76.3.0"),sQuery(id+"F0.wireOp",EDGE,"E1.76.4.0"),sQuery(id+"F0.wireOp",EDGE,"E1.76.5.0"),sQuery(id+"F0.wireOp",EDGE,"E1.76.6.0"),sQuery(id+"F0.wireOp",EDGE,"E1.76.7.0"),sQuery(id+"F0.wireOp",EDGE,"E1.76.8.0"),sQuery(id+"F0.wireOp",EDGE,"E1.76.9.0"),sQuery(id+"F0.wireOp",EDGE,"E1.76.10.0"),sQuery(id+"F0.wireOp",EDGE,"E1.76.11.0"),sQuery(id+"F0.wireOp",EDGE,"E1.76.12.0"),sQuery(id+"F0.wireOp",EDGE,"E1.76.13.0"),sQuery(id+"F0.wireOp",EDGE,"E1.76.14.0"),sQuery(id+"F0.wireOp",EDGE,"E1.76.15.0"),sQuery(id+"F0.wireOp",EDGE,"E1.76.16.0"),sQuery(id+"F0.wireOp",EDGE,"E1.76.17.0"),sQuery(id+"F0.wireOp",EDGE,"E1.76.18.0"),subQ83,sQuery(id+"F0.wireOp",EDGE,"E1.77.1.0"),sQuery(id+"F0.wireOp",EDGE,"E1.77.2.0"),sQuery(id+"F0.wireOp",EDGE,"E1.77.3.0"),sQuery(id+"F0.wireOp",EDGE,"E1.77.4.0"),sQuery(id+"F0.wireOp",EDGE,"E1.77.5.0"),sQuery(id+"F0.wireOp",EDGE,"E1.77.6.0"),sQuery(id+"F0.wireOp",EDGE,"E1.77.7.0"),sQuery(id+"F0.wireOp",EDGE,"E1.77.8.0"),sQuery(id+"F0.wireOp",EDGE,"E1.77.9.0"),sQuery(id+"F0.wireOp",EDGE,"E1.77.10.0"),sQuery(id+"F0.wireOp",EDGE,"E1.77.11.0"),sQuery(id+"F0.wireOp",EDGE,"E1.77.12.0"),sQuery(id+"F0.wireOp",EDGE,"E1.77.13.0"),sQuery(id+"F0.wireOp",EDGE,"E1.77.14.0"),sQuery(id+"F0.wireOp",EDGE,"E1.77.15.0"),sQuery(id+"F0.wireOp",EDGE,"E1.77.16.0"),sQuery(id+"F0.wireOp",EDGE,"E1.77.17.0"),sQuery(id+"F0.wireOp",EDGE,"E1.77.18.0"),subQ85,sQuery(id+"F0.wireOp",EDGE,"E1.78.1.0"),sQuery(id+"F0.wireOp",EDGE,"E1.78.2.0"),sQuery(id+"F0.wireOp",EDGE,"E1.78.3.0"),sQuery(id+"F0.wireOp",EDGE,"E1.78.4.0"),sQuery(id+"F0.wireOp",EDGE,"E1.78.5.0"),sQuery(id+"F0.wireOp",EDGE,"E1.78.6.0"),sQuery(id+"F0.wireOp",EDGE,"E1.78.7.0"),sQuery(id+"F0.wireOp",EDGE,"E1.78.8.0"),sQuery(id+"F0.wireOp",EDGE,"E1.78.9.0"),sQuery(id+"F0.wireOp",EDGE,"E1.78.10.0"),sQuery(id+"F0.wireOp",EDGE,"E1.78.11.0"),sQuery(id+"F0.wireOp",EDGE,"E1.78.12.0"),sQuery(id+"F0.wireOp",EDGE,"E1.78.13.0"),sQuery(id+"F0.wireOp",EDGE,"E1.78.14.0"),sQuery(id+"F0.wireOp",EDGE,"E1.78.15.0"),sQuery(id+"F0.wireOp",EDGE,"E1.78.16.0"),sQuery(id+"F0.wireOp",EDGE,"E1.78.17.0"),sQuery(id+"F0.wireOp",EDGE,"E1.78.18.0"),subQ87,sQuery(id+"F0.wireOp",EDGE,"E1.79.1.0"),sQuery(id+"F0.wireOp",EDGE,"E1.79.2.0"),sQuery(id+"F0.wireOp",EDGE,"E1.79.3.0"),sQuery(id+"F0.wireOp",EDGE,"E1.79.4.0"),sQuery(id+"F0.wireOp",EDGE,"E1.79.5.0"),sQuery(id+"F0.wireOp",EDGE,"E1.79.6.0"),sQuery(id+"F0.wireOp",EDGE,"E1.79.7.0"),sQuery(id+"F0.wireOp",EDGE,"E1.79.8.0"),sQuery(id+"F0.wireOp",EDGE,"E1.79.9.0"),sQuery(id+"F0.wireOp",EDGE,"E1.79.10.0"),sQuery(id+"F0.wireOp",EDGE,"E1.79.11.0"),sQuery(id+"F0.wireOp",EDGE,"E1.79.12.0"),sQuery(id+"F0.wireOp",EDGE,"E1.79.13.0"),sQuery(id+"F0.wireOp",EDGE,"E1.79.14.0"),sQuery(id+"F0.wireOp",EDGE,"E1.79.15.0"),sQuery(id+"F0.wireOp",EDGE,"E1.79.16.0"),sQuery(id+"F0.wireOp",EDGE,"E1.79.17.0"),sQuery(id+"F0.wireOp",EDGE,"E1.79.18.0"),subQ88,sQuery(id+"F0.wireOp",EDGE,"E1.80.1.0"),sQuery(id+"F0.wireOp",EDGE,"E1.80.2.0"),sQuery(id+"F0.wireOp",EDGE,"E1.80.3.0"),sQuery(id+"F0.wireOp",EDGE,"E1.80.4.0"),sQuery(id+"F0.wireOp",EDGE,"E1.80.5.0"),sQuery(id+"F0.wireOp",EDGE,"E1.80.6.0"),sQuery(id+"F0.wireOp",EDGE,"E1.80.7.0"),sQuery(id+"F0.wireOp",EDGE,"E1.80.8.0"),sQuery(id+"F0.wireOp",EDGE,"E1.80.9.0"),sQuery(id+"F0.wireOp",EDGE,"E1.80.10.0"),sQuery(id+"F0.wireOp",EDGE,"E1.80.11.0"),sQuery(id+"F0.wireOp",EDGE,"E1.80.12.0"),sQuery(id+"F0.wireOp",EDGE,"E1.80.13.0"),sQuery(id+"F0.wireOp",EDGE,"E1.80.14.0"),sQuery(id+"F0.wireOp",EDGE,"E1.80.15.0"),sQuery(id+"F0.wireOp",EDGE,"E1.80.16.0"),sQuery(id+"F0.wireOp",EDGE,"E1.80.17.0"),sQuery(id+"F0.wireOp",EDGE,"E1.80.18.0"),subQ89,sQuery(id+"F0.wireOp",EDGE,"E1.81.1.0"),sQuery(id+"F0.wireOp",EDGE,"E1.81.2.0"),sQuery(id+"F0.wireOp",EDGE,"E1.81.3.0"),sQuery(id+"F0.wireOp",EDGE,"E1.81.4.0"),sQuery(id+"F0.wireOp",EDGE,"E1.81.5.0"),sQuery(id+"F0.wireOp",EDGE,"E1.81.6.0"),sQuery(id+"F0.wireOp",EDGE,"E1.81.7.0"),sQuery(id+"F0.wireOp",EDGE,"E1.81.8.0"),sQuery(id+"F0.wireOp",EDGE,"E1.81.9.0"),sQuery(id+"F0.wireOp",EDGE,"E1.81.10.0"),sQuery(id+"F0.wireOp",EDGE,"E1.81.11.0"),sQuery(id+"F0.wireOp",EDGE,"E1.81.12.0"),sQuery(id+"F0.wireOp",EDGE,"E1.81.13.0"),sQuery(id+"F0.wireOp",EDGE,"E1.81.14.0"),sQuery(id+"F0.wireOp",EDGE,"E1.81.15.0"),sQuery(id+"F0.wireOp",EDGE,"E1.81.16.0"),sQuery(id+"F0.wireOp",EDGE,"E1.81.17.0"),sQuery(id+"F0.wireOp",EDGE,"E1.81.18.0"),subQ90,sQuery(id+"F0.wireOp",EDGE,"E1.82.1.0"),sQuery(id+"F0.wireOp",EDGE,"E1.82.2.0"),sQuery(id+"F0.wireOp",EDGE,"E1.82.3.0"),sQuery(id+"F0.wireOp",EDGE,"E1.82.4.0"),sQuery(id+"F0.wireOp",EDGE,"E1.82.5.0"),sQuery(id+"F0.wireOp",EDGE,"E1.82.6.0"),sQuery(id+"F0.wireOp",EDGE,"E1.82.7.0"),sQuery(id+"F0.wireOp",EDGE,"E1.82.8.0"),sQuery(id+"F0.wireOp",EDGE,"E1.82.9.0"),sQuery(id+"F0.wireOp",EDGE,"E1.82.10.0"),sQuery(id+"F0.wireOp",EDGE,"E1.82.11.0"),sQuery(id+"F0.wireOp",EDGE,"E1.82.12.0"),sQuery(id+"F0.wireOp",EDGE,"E1.82.13.0"),sQuery(id+"F0.wireOp",EDGE,"E1.82.14.0"),sQuery(id+"F0.wireOp",EDGE,"E1.82.15.0"),sQuery(id+"F0.wireOp",EDGE,"E1.82.16.0"),sQuery(id+"F0.wireOp",EDGE,"E1.82.17.0"),sQuery(id+"F0.wireOp",EDGE,"E1.82.18.0"),subQ91,sQuery(id+"F0.wireOp",EDGE,"E1.83.1.0"),sQuery(id+"F0.wireOp",EDGE,"E1.83.2.0"),sQuery(id+"F0.wireOp",EDGE,"E1.83.3.0"),sQuery(id+"F0.wireOp",EDGE,"E1.83.4.0"),sQuery(id+"F0.wireOp",EDGE,"E1.83.5.0"),sQuery(id+"F0.wireOp",EDGE,"E1.83.6.0"),sQuery(id+"F0.wireOp",EDGE,"E1.83.7.0"),sQuery(id+"F0.wireOp",EDGE,"E1.83.8.0"),sQuery(id+"F0.wireOp",EDGE,"E1.83.9.0"),sQuery(id+"F0.wireOp",EDGE,"E1.83.10.0"),sQuery(id+"F0.wireOp",EDGE,"E1.83.11.0"),sQuery(id+"F0.wireOp",EDGE,"E1.83.12.0"),sQuery(id+"F0.wireOp",EDGE,"E1.83.13.0"),sQuery(id+"F0.wireOp",EDGE,"E1.83.14.0"),sQuery(id+"F0.wireOp",EDGE,"E1.83.15.0"),sQuery(id+"F0.wireOp",EDGE,"E1.83.16.0"),sQuery(id+"F0.wireOp",EDGE,"E1.83.17.0"),sQuery(id+"F0.wireOp",EDGE,"E1.83.18.0"),subQ92,sQuery(id+"F0.wireOp",EDGE,"E1.84.1.0"),sQuery(id+"F0.wireOp",EDGE,"E1.84.2.0"),sQuery(id+"F0.wireOp",EDGE,"E1.84.3.0"),sQuery(id+"F0.wireOp",EDGE,"E1.84.4.0"),sQuery(id+"F0.wireOp",EDGE,"E1.84.5.0"),sQuery(id+"F0.wireOp",EDGE,"E1.84.6.0"),sQuery(id+"F0.wireOp",EDGE,"E1.84.7.0"),sQuery(id+"F0.wireOp",EDGE,"E1.84.8.0"),sQuery(id+"F0.wireOp",EDGE,"E1.84.9.0"),sQuery(id+"F0.wireOp",EDGE,"E1.84.10.0"),sQuery(id+"F0.wireOp",EDGE,"E1.84.11.0"),sQuery(id+"F0.wireOp",EDGE,"E1.84.12.0"),sQuery(id+"F0.wireOp",EDGE,"E1.84.13.0"),sQuery(id+"F0.wireOp",EDGE,"E1.84.14.0"),sQuery(id+"F0.wireOp",EDGE,"E1.84.15.0"),sQuery(id+"F0.wireOp",EDGE,"E1.84.16.0"),sQuery(id+"F0.wireOp",EDGE,"E1.84.17.0"),sQuery(id+"F0.wireOp",EDGE,"E1.84.18.0"),subQ93,sQuery(id+"F0.wireOp",EDGE,"E1.85.1.0"),sQuery(id+"F0.wireOp",EDGE,"E1.85.2.0"),sQuery(id+"F0.wireOp",EDGE,"E1.85.3.0"),sQuery(id+"F0.wireOp",EDGE,"E1.85.4.0"),sQuery(id+"F0.wireOp",EDGE,"E1.85.5.0"),sQuery(id+"F0.wireOp",EDGE,"E1.85.6.0"),sQuery(id+"F0.wireOp",EDGE,"E1.85.7.0"),sQuery(id+"F0.wireOp",EDGE,"E1.85.8.0"),sQuery(id+"F0.wireOp",EDGE,"E1.85.9.0"),sQuery(id+"F0.wireOp",EDGE,"E1.85.10.0"),sQuery(id+"F0.wireOp",EDGE,"E1.85.11.0"),sQuery(id+"F0.wireOp",EDGE,"E1.85.12.0"),sQuery(id+"F0.wireOp",EDGE,"E1.85.13.0"),sQuery(id+"F0.wireOp",EDGE,"E1.85.14.0"),sQuery(id+"F0.wireOp",EDGE,"E1.85.15.0"),sQuery(id+"F0.wireOp",EDGE,"E1.85.16.0"),sQuery(id+"F0.wireOp",EDGE,"E1.85.17.0"),sQuery(id+"F0.wireOp",EDGE,"E1.85.18.0"),sQuery(id+"F0.wireOp",EDGE,"E2.bottom"),subQ0,sQuery(id+"F0.wireOp",EDGE,"E2.left"),subQ19,subQ82,sQuery(id+"F0.wireOp",EDGE,"E3.0.86.1"),sQuery(id+"F0.wireOp",EDGE,"E3.0.86.2"),sQuery(id+"F0.wireOp",EDGE,"E3.0.86.3"),sQuery(id+"F0.wireOp",EDGE,"E3.0.86.4"),sQuery(id+"F0.wireOp",EDGE,"E3.0.86.5"),sQuery(id+"F0.wireOp",EDGE,"E3.0.86.6"),sQuery(id+"F0.wireOp",EDGE,"E3.0.86.7"),sQuery(id+"F0.wireOp",EDGE,"E3.0.86.8"),sQuery(id+"F0.wireOp",EDGE,"E3.0.86.9"),sQuery(id+"F0.wireOp",EDGE,"E3.0.86.10"),sQuery(id+"F0.wireOp",EDGE,"E3.0.86.11"),sQuery(id+"F0.wireOp",EDGE,"E3.0.86.12"),sQuery(id+"F0.wireOp",EDGE,"E3.0.86.13"),sQuery(id+"F0.wireOp",EDGE,"E3.0.86.14"),sQuery(id+"F0.wireOp",EDGE,"E3.0.86.15"),sQuery(id+"F0.wireOp",EDGE,"E3.0.86.16"),sQuery(id+"F0.wireOp",EDGE,"E3.0.86.17"),sQuery(id+"F0.wireOp",EDGE,"E3.0.86.18"),subQ84,sQuery(id+"F0.wireOp",EDGE,"E3.0.87.1"),sQuery(id+"F0.wireOp",EDGE,"E3.0.87.2"),sQuery(id+"F0.wireOp",EDGE,"E3.0.87.3"),sQuery(id+"F0.wireOp",EDGE,"E3.0.87.4"),sQuery(id+"F0.wireOp",EDGE,"E3.0.87.5"),sQuery(id+"F0.wireOp",EDGE,"E3.0.87.6"),sQuery(id+"F0.wireOp",EDGE,"E3.0.87.7"),sQuery(id+"F0.wireOp",EDGE,"E3.0.87.8"),sQuery(id+"F0.wireOp",EDGE,"E3.0.87.9"),sQuery(id+"F0.wireOp",EDGE,"E3.0.87.10"),sQuery(id+"F0.wireOp",EDGE,"E3.0.87.11"),sQuery(id+"F0.wireOp",EDGE,"E3.0.87.12"),sQuery(id+"F0.wireOp",EDGE,"E3.0.87.13"),sQuery(id+"F0.wireOp",EDGE,"E3.0.87.14"),sQuery(id+"F0.wireOp",EDGE,"E3.0.87.15"),sQuery(id+"F0.wireOp",EDGE,"E3.0.87.16"),sQuery(id+"F0.wireOp",EDGE,"E3.0.87.17"),sQuery(id+"F0.wireOp",EDGE,"E3.0.87.18"),subQ86,sQuery(id+"F0.wireOp",EDGE,"E3.0.88.1"),sQuery(id+"F0.wireOp",EDGE,"E3.0.88.2"),sQuery(id+"F0.wireOp",EDGE,"E3.0.88.3"),sQuery(id+"F0.wireOp",EDGE,"E3.0.88.4"),sQuery(id+"F0.wireOp",EDGE,"E3.0.88.5"),sQuery(id+"F0.wireOp",EDGE,"E3.0.88.6"),sQuery(id+"F0.wireOp",EDGE,"E3.0.88.7"),sQuery(id+"F0.wireOp",EDGE,"E3.0.88.8"),sQuery(id+"F0.wireOp",EDGE,"E3.0.88.9"),sQuery(id+"F0.wireOp",EDGE,"E3.0.88.10"),sQuery(id+"F0.wireOp",EDGE,"E3.0.88.11"),sQuery(id+"F0.wireOp",EDGE,"E3.0.88.12"),sQuery(id+"F0.wireOp",EDGE,"E3.0.88.13"),sQuery(id+"F0.wireOp",EDGE,"E3.0.88.14"),sQuery(id+"F0.wireOp",EDGE,"E3.0.88.15"),sQuery(id+"F0.wireOp",EDGE,"E3.0.88.16"),sQuery(id+"F0.wireOp",EDGE,"E3.0.88.17"),sQuery(id+"F0.wireOp",EDGE,"E3.0.88.18")])],"isStart":false})})});}
            var sketch = newSketch(context, id + "F9", { "sketchPlane" : qUnion([Q0])});
            skLineSegment(sketch, "E12.bottom", {"start": v(-10, 30) * mm, "end": v(233.44, 30) * mm});
            skLineSegment(sketch, "E12.top", {"start": v(-10, -282) * mm, "end": v(233.44, -282) * mm});
            skLineSegment(sketch, "E12.left", {"start": v(-10, 30) * mm, "end": v(-10, -282) * mm});
            skLineSegment(sketch, "E12.right", {"start": v(233.44, 30) * mm, "end": v(233.44, -282) * mm});
            skSolve(sketch);
        }
        {
            var Q0;
            Q0 = qSketchRegion(id + "F9", true);
            extrude(context, id + "F10", {"entities" : qUnion([Q0]), "depth" : 12.5 * mm, "offsetDistance" : 25 * mm});
        }
        {
            var Q0;
            Q0=makeQuery(id+"F10.opExtrude","SWEPT_FACE",FACE,{"disambiguationData":[OSD([sQuery(id+"F9.wireOp",EDGE,"E12.right")])]});
            var sketch = newSketch(context, id + "F11", { "sketchPlane" : qUnion([Q0])});
            skLineSegment(sketch, "E13.bottom", {"start": v(-263.5, 12.5) * mm, "end": v(-254.5, 12.5) * mm});
            skLineSegment(sketch, "E13.top", {"start": v(-263.5, 17.5) * mm, "end": v(-254.5, 17.5) * mm});
            skLineSegment(sketch, "E13.left", {"start": v(-263.5, 12.5) * mm, "end": v(-263.5, 17.5) * mm});
            skLineSegment(sketch, "E13.right", {"start": v(-254.5, 12.5) * mm, "end": v(-254.5, 17.5) * mm});
            skLineSegment(sketch, "E14.1.0.0", {"start": v(-249.5, 17.5) * mm, "end": v(-240.5, 17.5) * mm});
            skLineSegment(sketch, "E14.1.0.1", {"start": v(-249.5, 12.5) * mm, "end": v(-249.5, 17.5) * mm});
            skLineSegment(sketch, "E14.1.0.2", {"start": v(-249.5, 12.5) * mm, "end": v(-240.5, 12.5) * mm});
            skLineSegment(sketch, "E14.1.0.3", {"start": v(-240.5, 12.5) * mm, "end": v(-240.5, 17.5) * mm});
            skLineSegment(sketch, "E14.2.0.0", {"start": v(-235.5, 17.5) * mm, "end": v(-226.5, 17.5) * mm});
            skLineSegment(sketch, "E14.2.0.1", {"start": v(-235.5, 12.5) * mm, "end": v(-235.5, 17.5) * mm});
            skLineSegment(sketch, "E14.2.0.2", {"start": v(-235.5, 12.5) * mm, "end": v(-226.5, 12.5) * mm});
            skLineSegment(sketch, "E14.2.0.3", {"start": v(-226.5, 12.5) * mm, "end": v(-226.5, 17.5) * mm});
            skLineSegment(sketch, "E14.3.0.0", {"start": v(-221.5, 17.5) * mm, "end": v(-212.5, 17.5) * mm});
            skLineSegment(sketch, "E14.3.0.1", {"start": v(-221.5, 12.5) * mm, "end": v(-221.5, 17.5) * mm});
            skLineSegment(sketch, "E14.3.0.2", {"start": v(-221.5, 12.5) * mm, "end": v(-212.5, 12.5) * mm});
            skLineSegment(sketch, "E14.3.0.3", {"start": v(-212.5, 12.5) * mm, "end": v(-212.5, 17.5) * mm});
            skLineSegment(sketch, "E14.4.0.0", {"start": v(-207.5, 17.5) * mm, "end": v(-198.5, 17.5) * mm});
            skLineSegment(sketch, "E14.4.0.1", {"start": v(-207.5, 12.5) * mm, "end": v(-207.5, 17.5) * mm});
            skLineSegment(sketch, "E14.4.0.2", {"start": v(-207.5, 12.5) * mm, "end": v(-198.5, 12.5) * mm});
            skLineSegment(sketch, "E14.4.0.3", {"start": v(-198.5, 12.5) * mm, "end": v(-198.5, 17.5) * mm});
            skLineSegment(sketch, "E14.5.0.0", {"start": v(-193.5, 17.5) * mm, "end": v(-184.5, 17.5) * mm});
            skLineSegment(sketch, "E14.5.0.1", {"start": v(-193.5, 12.5) * mm, "end": v(-193.5, 17.5) * mm});
            skLineSegment(sketch, "E14.5.0.2", {"start": v(-193.5, 12.5) * mm, "end": v(-184.5, 12.5) * mm});
            skLineSegment(sketch, "E14.5.0.3", {"start": v(-184.5, 12.5) * mm, "end": v(-184.5, 17.5) * mm});
            skLineSegment(sketch, "E14.6.0.0", {"start": v(-179.5, 17.5) * mm, "end": v(-170.5, 17.5) * mm});
            skLineSegment(sketch, "E14.6.0.1", {"start": v(-179.5, 12.5) * mm, "end": v(-179.5, 17.5) * mm});
            skLineSegment(sketch, "E14.6.0.2", {"start": v(-179.5, 12.5) * mm, "end": v(-170.5, 12.5) * mm});
            skLineSegment(sketch, "E14.6.0.3", {"start": v(-170.5, 12.5) * mm, "end": v(-170.5, 17.5) * mm});
            skLineSegment(sketch, "E14.7.0.0", {"start": v(-165.5, 17.5) * mm, "end": v(-156.5, 17.5) * mm});
            skLineSegment(sketch, "E14.7.0.1", {"start": v(-165.5, 12.5) * mm, "end": v(-165.5, 17.5) * mm});
            skLineSegment(sketch, "E14.7.0.2", {"start": v(-165.5, 12.5) * mm, "end": v(-156.5, 12.5) * mm});
            skLineSegment(sketch, "E14.7.0.3", {"start": v(-156.5, 12.5) * mm, "end": v(-156.5, 17.5) * mm});
            skLineSegment(sketch, "E14.8.0.0", {"start": v(-151.5, 17.5) * mm, "end": v(-142.5, 17.5) * mm});
            skLineSegment(sketch, "E14.8.0.1", {"start": v(-151.5, 12.5) * mm, "end": v(-151.5, 17.5) * mm});
            skLineSegment(sketch, "E14.8.0.2", {"start": v(-151.5, 12.5) * mm, "end": v(-142.5, 12.5) * mm});
            skLineSegment(sketch, "E14.8.0.3", {"start": v(-142.5, 12.5) * mm, "end": v(-142.5, 17.5) * mm});
            skLineSegment(sketch, "E14.9.0.0", {"start": v(-137.5, 17.5) * mm, "end": v(-128.5, 17.5) * mm});
            skLineSegment(sketch, "E14.9.0.1", {"start": v(-137.5, 12.5) * mm, "end": v(-137.5, 17.5) * mm});
            skLineSegment(sketch, "E14.9.0.2", {"start": v(-137.5, 12.5) * mm, "end": v(-128.5, 12.5) * mm});
            skLineSegment(sketch, "E14.9.0.3", {"start": v(-128.5, 12.5) * mm, "end": v(-128.5, 17.5) * mm});
            skLineSegment(sketch, "E14.10.0.0", {"start": v(-123.5, 17.5) * mm, "end": v(-114.5, 17.5) * mm});
            skLineSegment(sketch, "E14.10.0.1", {"start": v(-123.5, 12.5) * mm, "end": v(-123.5, 17.5) * mm});
            skLineSegment(sketch, "E14.10.0.2", {"start": v(-123.5, 12.5) * mm, "end": v(-114.5, 12.5) * mm});
            skLineSegment(sketch, "E14.10.0.3", {"start": v(-114.5, 12.5) * mm, "end": v(-114.5, 17.5) * mm});
            skLineSegment(sketch, "E14.11.0.0", {"start": v(-109.5, 17.5) * mm, "end": v(-100.5, 17.5) * mm});
            skLineSegment(sketch, "E14.11.0.1", {"start": v(-109.5, 12.5) * mm, "end": v(-109.5, 17.5) * mm});
            skLineSegment(sketch, "E14.11.0.2", {"start": v(-109.5, 12.5) * mm, "end": v(-100.5, 12.5) * mm});
            skLineSegment(sketch, "E14.11.0.3", {"start": v(-100.5, 12.5) * mm, "end": v(-100.5, 17.5) * mm});
            skLineSegment(sketch, "E14.12.0.0", {"start": v(-95.5, 17.5) * mm, "end": v(-86.5, 17.5) * mm});
            skLineSegment(sketch, "E14.12.0.1", {"start": v(-95.5, 12.5) * mm, "end": v(-95.5, 17.5) * mm});
            skLineSegment(sketch, "E14.12.0.2", {"start": v(-95.5, 12.5) * mm, "end": v(-86.5, 12.5) * mm});
            skLineSegment(sketch, "E14.12.0.3", {"start": v(-86.5, 12.5) * mm, "end": v(-86.5, 17.5) * mm});
            skLineSegment(sketch, "E14.13.0.0", {"start": v(-81.5, 17.5) * mm, "end": v(-72.5, 17.5) * mm});
            skLineSegment(sketch, "E14.13.0.1", {"start": v(-81.5, 12.5) * mm, "end": v(-81.5, 17.5) * mm});
            skLineSegment(sketch, "E14.13.0.2", {"start": v(-81.5, 12.5) * mm, "end": v(-72.5, 12.5) * mm});
            skLineSegment(sketch, "E14.13.0.3", {"start": v(-72.5, 12.5) * mm, "end": v(-72.5, 17.5) * mm});
            skLineSegment(sketch, "E14.14.0.0", {"start": v(-67.5, 17.5) * mm, "end": v(-58.5, 17.5) * mm});
            skLineSegment(sketch, "E14.14.0.1", {"start": v(-67.5, 12.5) * mm, "end": v(-67.5, 17.5) * mm});
            skLineSegment(sketch, "E14.14.0.2", {"start": v(-67.5, 12.5) * mm, "end": v(-58.5, 12.5) * mm});
            skLineSegment(sketch, "E14.14.0.3", {"start": v(-58.5, 12.5) * mm, "end": v(-58.5, 17.5) * mm});
            skLineSegment(sketch, "E14.15.0.0", {"start": v(-53.5, 17.5) * mm, "end": v(-44.5, 17.5) * mm});
            skLineSegment(sketch, "E14.15.0.1", {"start": v(-53.5, 12.5) * mm, "end": v(-53.5, 17.5) * mm});
            skLineSegment(sketch, "E14.15.0.2", {"start": v(-53.5, 12.5) * mm, "end": v(-44.5, 12.5) * mm});
            skLineSegment(sketch, "E14.15.0.3", {"start": v(-44.5, 12.5) * mm, "end": v(-44.5, 17.5) * mm});
            skLineSegment(sketch, "E14.16.0.0", {"start": v(-39.5, 17.5) * mm, "end": v(-30.5, 17.5) * mm});
            skLineSegment(sketch, "E14.16.0.1", {"start": v(-39.5, 12.5) * mm, "end": v(-39.5, 17.5) * mm});
            skLineSegment(sketch, "E14.16.0.2", {"start": v(-39.5, 12.5) * mm, "end": v(-30.5, 12.5) * mm});
            skLineSegment(sketch, "E14.16.0.3", {"start": v(-30.5, 12.5) * mm, "end": v(-30.5, 17.5) * mm});
            skLineSegment(sketch, "E14.17.0.0", {"start": v(-25.5, 17.5) * mm, "end": v(-16.5, 17.5) * mm});
            skLineSegment(sketch, "E14.17.0.1", {"start": v(-25.5, 12.5) * mm, "end": v(-25.5, 17.5) * mm});
            skLineSegment(sketch, "E14.17.0.2", {"start": v(-25.5, 12.5) * mm, "end": v(-16.5, 12.5) * mm});
            skLineSegment(sketch, "E14.17.0.3", {"start": v(-16.5, 12.5) * mm, "end": v(-16.5, 17.5) * mm});
            skLineSegment(sketch, "E14.18.0.0", {"start": v(-11.5, 17.5) * mm, "end": v(-2.5, 17.5) * mm});
            skLineSegment(sketch, "E14.18.0.1", {"start": v(-11.5, 12.5) * mm, "end": v(-11.5, 17.5) * mm});
            skLineSegment(sketch, "E14.18.0.2", {"start": v(-11.5, 12.5) * mm, "end": v(-2.5, 12.5) * mm});
            skLineSegment(sketch, "E14.18.0.3", {"start": v(-2.5, 12.5) * mm, "end": v(-2.5, 17.5) * mm});
            skLineSegment(sketch, "E14.direction1", {"start": v(-263.5, 17.5) * mm, "end": v(-249.5, 17.5) * mm, "construction": true});
            skSolve(sketch);
        }
        {
            var Q0;
            Q0 = qSketchRegion(id + "F11", true);
            extrude(context, id + "F12", {"entities" : qUnion([Q0]), "operationType" : NewBodyOperationType.REMOVE, "endBound" : BoundingType.THROUGH_ALL, "oppositeDirection" : true, "depth" : 25 * mm, "offsetDistance" : 25 * mm});
        }
        {
            var Q0;
            Q0=makeQuery(id+"F10.opExtrude","CAP_FACE",FACE,{"disambiguationData":[OSD([sQuery(id+"F9.wireOp",EDGE,"E12.bottom"),sQuery(id+"F9.wireOp",EDGE,"E12.top"),sQuery(id+"F9.wireOp",EDGE,"E12.left"),sQuery(id+"F9.wireOp",EDGE,"E12.right")])],"isStart":false});
            var sketch = newSketch(context, id + "F13", { "sketchPlane" : qUnion([Q0])});
            skCircle(sketch, "E15", {"center": v(5.08, 20) * mm, "radius": 5 * mm});
            skLineSegment(sketch, "E16", {"start": v(-1.27, 30) * mm, "end": v(11.43, 30) * mm, "construction": true});
            skLineSegment(sketch, "E17", {"start": v(5.08, 30) * mm, "end": v(5.08, 11.14) * mm, "construction": true});
            skLineSegment(sketch, "E18", {"start": v(111.72, 30) * mm, "end": v(111.72, 51.45) * mm, "construction": true});
            skCircle(sketch, "E19.MirrorC", {"center": v(218.36, 20) * mm, "radius": 5 * mm});
            skLineSegment(sketch, "E20", {"start": v(-10, -126) * mm, "end": v(-58.43, -126) * mm, "construction": true});
            skCircle(sketch, "E21.MirrorC", {"center": v(5.08, -272) * mm, "radius": 5 * mm});
            skCircle(sketch, "E22.MirrorC", {"center": v(218.36, -272) * mm, "radius": 5 * mm});
            skLineSegment(sketch, "E23", {"start": v(5.08, 20) * mm, "end": v(218.36, 20) * mm, "construction": true});
            skLineSegment(sketch, "E24", {"start": v(5.08, -272) * mm, "end": v(218.36, -272) * mm, "construction": true});
            skCircle(sketch, "E25", {"center": v(111.72, 20) * mm, "radius": 5 * mm});
            skCircle(sketch, "E26", {"center": v(111.72, -272) * mm, "radius": 5 * mm});
            skSolve(sketch);
        }
        {
            var Q0;
            Q0 = qSketchRegion(id + "F13", true);
            extrude(context, id + "F14", {"entities" : qUnion([Q0]), "operationType" : NewBodyOperationType.REMOVE, "endBound" : BoundingType.THROUGH_ALL, "oppositeDirection" : true, "depth" : 25 * mm, "offsetDistance" : 25 * mm});
        }
    });
